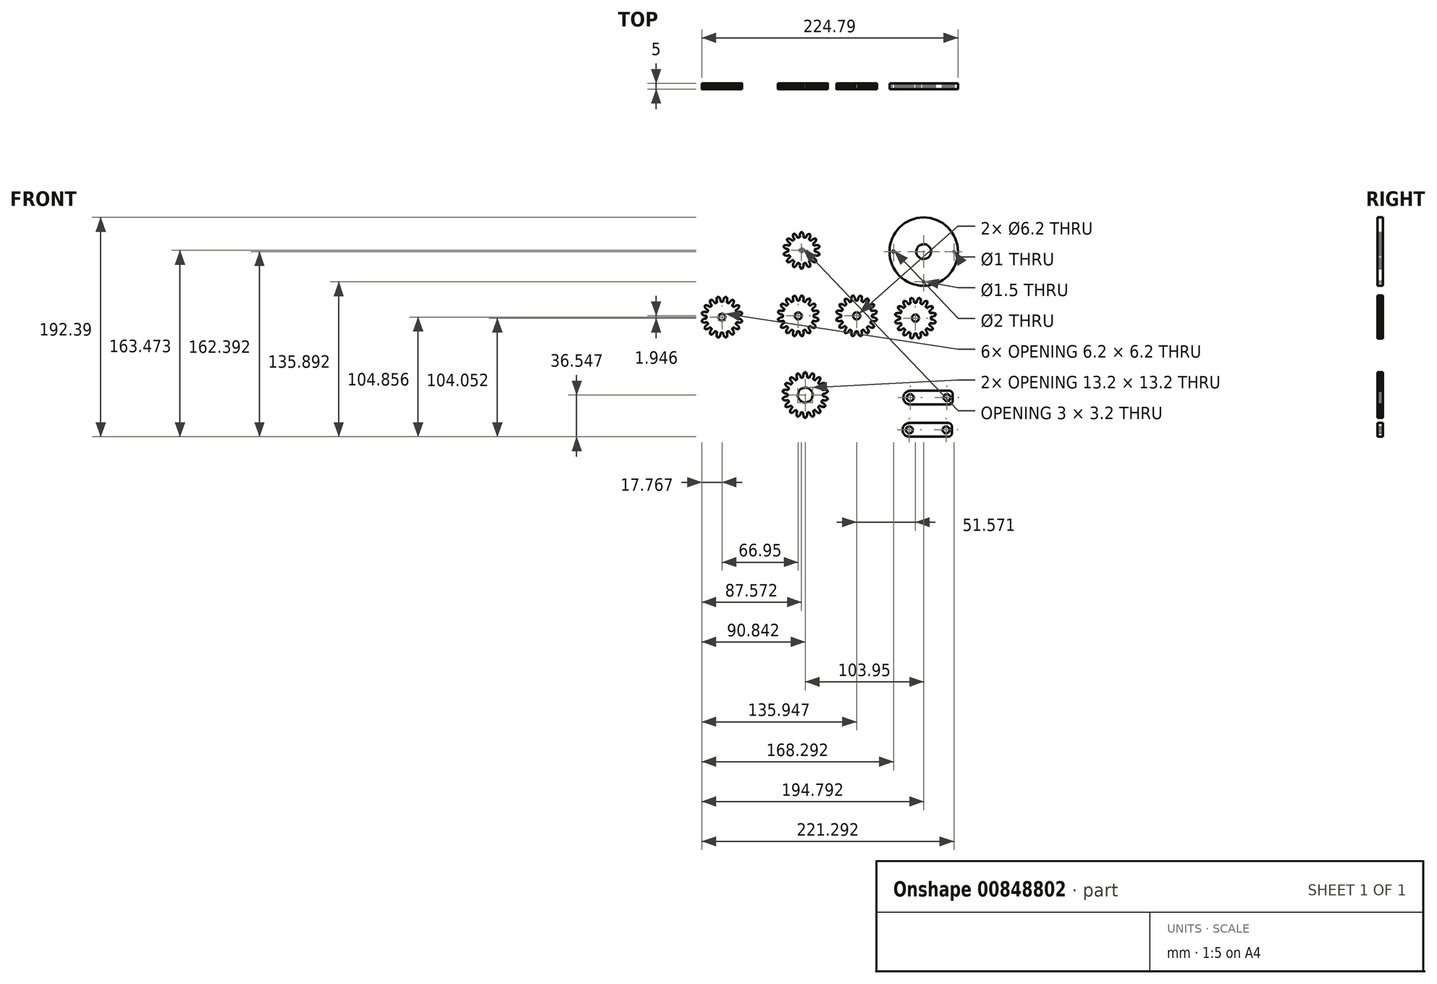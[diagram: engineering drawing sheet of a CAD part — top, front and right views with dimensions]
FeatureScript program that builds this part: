
annotation { "Feature Type Name" : "Feature", "Feature Type Description" : "" }
export const myFeature = defineFeature(function(context is Context, id is Id, definition is map)
    precondition{}
    {
        {
            var Q0;
            Q0=qCreatedBy(makeId("Front.planeOp"),FACE);
            var sketch = newSketch(context, id + "F0", { "sketchPlane" : qUnion([Q0])});
            skArc(sketch, "E0", {"start": v(-65.12, 71.31) * mm, "mid": v(-65.39, 71.53) * mm, "end": v(-65.66, 71.75) * mm});
            skArc(sketch, "E1", {"start": v(-65.12, 71.31) * mm, "mid": v(-64.55, 71.12) * mm, "end": v(-64, 71.37) * mm});
            skLineSegment(sketch, "E2", {"start": v(-61.43, 72.85) * mm, "end": v(-60.46, 73.02) * mm});
            skLineSegment(sketch, "E3", {"start": v(-62.28, 72.6) * mm, "end": v(-61.43, 72.85) * mm});
            skLineSegment(sketch, "E4", {"start": v(-63.02, 72.25) * mm, "end": v(-62.28, 72.6) * mm});
            skLineSegment(sketch, "E5", {"start": v(-63.17, 72.16) * mm, "end": v(-63.02, 72.25) * mm});
            skLineSegment(sketch, "E6", {"start": v(-63.29, 72.07) * mm, "end": v(-63.17, 72.16) * mm});
            skLineSegment(sketch, "E7", {"start": v(-63.37, 72) * mm, "end": v(-63.29, 72.07) * mm});
            skLineSegment(sketch, "E8", {"start": v(-63.59, 71.8) * mm, "end": v(-63.37, 72) * mm});
            skLineSegment(sketch, "E9", {"start": v(-64, 71.37) * mm, "end": v(-63.59, 71.8) * mm});
            skArc(sketch, "E10", {"start": v(-59.66, 72) * mm, "mid": v(-60.05, 72.52) * mm, "end": v(-60.46, 73.02) * mm});
            skLineSegment(sketch, "E11", {"start": v(-60.03, 71.1) * mm, "end": v(-59.66, 72) * mm});
            skLineSegment(sketch, "E12", {"start": v(-60.46, 70.33) * mm, "end": v(-60.03, 71.1) * mm});
            skLineSegment(sketch, "E13", {"start": v(-60.97, 69.68) * mm, "end": v(-60.46, 70.33) * mm});
            skLineSegment(sketch, "E14", {"start": v(-61.1, 69.56) * mm, "end": v(-60.97, 69.68) * mm});
            skLineSegment(sketch, "E15", {"start": v(-61.2, 69.46) * mm, "end": v(-61.1, 69.56) * mm});
            skLineSegment(sketch, "E16", {"start": v(-61.3, 69.4) * mm, "end": v(-61.2, 69.46) * mm});
            skLineSegment(sketch, "E17", {"start": v(-62.05, 68.93) * mm, "end": v(-61.55, 69.23) * mm});
            skArc(sketch, "E18", {"start": v(-62.05, 68.93) * mm, "mid": v(-62.41, 68.45) * mm, "end": v(-62.35, 67.84) * mm});
            skArc(sketch, "E19", {"start": v(-62.05, 67.22) * mm, "mid": v(-62.2, 67.53) * mm, "end": v(-62.35, 67.84) * mm});
            skArc(sketch, "E20", {"start": v(-62.05, 67.22) * mm, "mid": v(-61.62, 66.8) * mm, "end": v(-61.01, 66.78) * mm});
            skLineSegment(sketch, "E21", {"start": v(-58.06, 67) * mm, "end": v(-57.12, 66.73) * mm});
            skLineSegment(sketch, "E22", {"start": v(-58.93, 67.15) * mm, "end": v(-58.06, 67) * mm});
            skLineSegment(sketch, "E23", {"start": v(-59.76, 67.15) * mm, "end": v(-58.93, 67.15) * mm});
            skLineSegment(sketch, "E24", {"start": v(-60.07, 67.1) * mm, "end": v(-59.93, 67.13) * mm});
            skLineSegment(sketch, "E25", {"start": v(-60.18, 67.08) * mm, "end": v(-60.07, 67.1) * mm});
            skLineSegment(sketch, "E26", {"start": v(-60.46, 66.98) * mm, "end": v(-60.18, 67.08) * mm});
            skLineSegment(sketch, "E27", {"start": v(-61.01, 66.78) * mm, "end": v(-60.46, 66.98) * mm});
            skArc(sketch, "E28", {"start": v(-56.83, 65.47) * mm, "mid": v(-56.96, 66.1) * mm, "end": v(-57.12, 66.73) * mm});
            skLineSegment(sketch, "E29", {"start": v(-57.56, 64.81) * mm, "end": v(-56.83, 65.47) * mm});
            skLineSegment(sketch, "E30", {"start": v(-58.28, 64.3) * mm, "end": v(-57.56, 64.81) * mm});
            skLineSegment(sketch, "E31", {"start": v(-59.02, 63.94) * mm, "end": v(-58.28, 64.3) * mm});
            skLineSegment(sketch, "E32", {"start": v(-59.19, 63.89) * mm, "end": v(-59.02, 63.94) * mm});
            skLineSegment(sketch, "E33", {"start": v(-59.33, 63.85) * mm, "end": v(-59.19, 63.89) * mm});
            skLineSegment(sketch, "E34", {"start": v(-59.43, 63.83) * mm, "end": v(-59.33, 63.85) * mm});
            skLineSegment(sketch, "E35", {"start": v(-59.73, 63.8) * mm, "end": v(-59.43, 63.83) * mm});
            skLineSegment(sketch, "E36", {"start": v(-60.32, 63.74) * mm, "end": v(-59.73, 63.8) * mm});
            skArc(sketch, "E37", {"start": v(-60.32, 63.74) * mm, "mid": v(-60.86, 63.46) * mm, "end": v(-61.06, 62.9) * mm});
            skArc(sketch, "E38", {"start": v(-61.06, 62.2) * mm, "mid": v(-61.06, 62.54) * mm, "end": v(-61.06, 62.9) * mm});
            skArc(sketch, "E39", {"start": v(-61.06, 62.2) * mm, "mid": v(-60.86, 61.63) * mm, "end": v(-60.32, 61.35) * mm});
            skLineSegment(sketch, "E40", {"start": v(-57.56, 60.27) * mm, "end": v(-56.83, 59.61) * mm});
            skLineSegment(sketch, "E41", {"start": v(-58.28, 60.78) * mm, "end": v(-57.56, 60.27) * mm});
            skLineSegment(sketch, "E42", {"start": v(-59.02, 61.14) * mm, "end": v(-58.28, 60.78) * mm});
            skLineSegment(sketch, "E43", {"start": v(-59.19, 61.2) * mm, "end": v(-59.02, 61.14) * mm});
            skLineSegment(sketch, "E44", {"start": v(-59.33, 61.24) * mm, "end": v(-59.19, 61.2) * mm});
            skLineSegment(sketch, "E45", {"start": v(-59.43, 61.26) * mm, "end": v(-59.33, 61.24) * mm});
            skLineSegment(sketch, "E46", {"start": v(-59.73, 61.3) * mm, "end": v(-59.43, 61.26) * mm});
            skLineSegment(sketch, "E47", {"start": v(-60.32, 61.35) * mm, "end": v(-59.73, 61.3) * mm});
            skArc(sketch, "E48", {"start": v(-57.12, 58.36) * mm, "mid": v(-56.96, 58.98) * mm, "end": v(-56.83, 59.61) * mm});
            skLineSegment(sketch, "E49", {"start": v(-58.06, 58.08) * mm, "end": v(-57.12, 58.36) * mm});
            skLineSegment(sketch, "E50", {"start": v(-58.93, 57.94) * mm, "end": v(-58.06, 58.08) * mm});
            skLineSegment(sketch, "E51", {"start": v(-59.76, 57.93) * mm, "end": v(-58.93, 57.94) * mm});
            skLineSegment(sketch, "E52", {"start": v(-59.93, 57.95) * mm, "end": v(-59.76, 57.93) * mm});
            skLineSegment(sketch, "E53", {"start": v(-60.07, 57.98) * mm, "end": v(-59.93, 57.95) * mm});
            skLineSegment(sketch, "E54", {"start": v(-60.18, 58) * mm, "end": v(-60.07, 57.98) * mm});
            skLineSegment(sketch, "E55", {"start": v(-60.46, 58.1) * mm, "end": v(-60.18, 58) * mm});
            skLineSegment(sketch, "E56", {"start": v(-61.01, 58.3) * mm, "end": v(-60.46, 58.1) * mm});
            skArc(sketch, "E57", {"start": v(-61.01, 58.3) * mm, "mid": v(-61.62, 58.3) * mm, "end": v(-62.05, 57.87) * mm});
            skArc(sketch, "E58", {"start": v(-62.35, 57.24) * mm, "mid": v(-62.2, 57.55) * mm, "end": v(-62.05, 57.87) * mm});
            skArc(sketch, "E59", {"start": v(-62.35, 57.24) * mm, "mid": v(-62.41, 56.64) * mm, "end": v(-62.05, 56.16) * mm});
            skLineSegment(sketch, "E60", {"start": v(-60.03, 54) * mm, "end": v(-59.66, 53.08) * mm});
            skLineSegment(sketch, "E61", {"start": v(-60.46, 54.76) * mm, "end": v(-60.03, 54) * mm});
            skLineSegment(sketch, "E62", {"start": v(-60.97, 55.4) * mm, "end": v(-60.46, 54.76) * mm});
            skLineSegment(sketch, "E63", {"start": v(-61.1, 55.53) * mm, "end": v(-60.97, 55.4) * mm});
            skLineSegment(sketch, "E64", {"start": v(-61.2, 55.63) * mm, "end": v(-61.1, 55.53) * mm});
            skLineSegment(sketch, "E65", {"start": v(-61.3, 55.7) * mm, "end": v(-61.2, 55.63) * mm});
            skLineSegment(sketch, "E66", {"start": v(-61.55, 55.85) * mm, "end": v(-61.3, 55.7) * mm});
            skLineSegment(sketch, "E67", {"start": v(-62.05, 56.16) * mm, "end": v(-61.55, 55.85) * mm});
            skArc(sketch, "E68", {"start": v(-60.46, 52.07) * mm, "mid": v(-60.05, 52.57) * mm, "end": v(-59.66, 53.08) * mm});
            skLineSegment(sketch, "E69", {"start": v(-61.43, 52.23) * mm, "end": v(-60.46, 52.07) * mm});
            skLineSegment(sketch, "E70", {"start": v(-62.28, 52.48) * mm, "end": v(-61.43, 52.23) * mm});
            skLineSegment(sketch, "E71", {"start": v(-63.02, 52.84) * mm, "end": v(-62.28, 52.48) * mm});
            skLineSegment(sketch, "E72", {"start": v(-63.17, 52.93) * mm, "end": v(-63.02, 52.84) * mm});
            skLineSegment(sketch, "E73", {"start": v(-63.29, 53.01) * mm, "end": v(-63.17, 52.93) * mm});
            skLineSegment(sketch, "E74", {"start": v(-63.37, 53.08) * mm, "end": v(-63.29, 53.01) * mm});
            skLineSegment(sketch, "E75", {"start": v(-63.59, 53.3) * mm, "end": v(-63.37, 53.08) * mm});
            skLineSegment(sketch, "E76", {"start": v(-64, 53.72) * mm, "end": v(-63.59, 53.3) * mm});
            skArc(sketch, "E77", {"start": v(-64, 53.72) * mm, "mid": v(-64.55, 53.97) * mm, "end": v(-65.12, 53.77) * mm});
            skArc(sketch, "E78", {"start": v(-65.66, 53.34) * mm, "mid": v(-65.39, 53.55) * mm, "end": v(-65.12, 53.77) * mm});
            skArc(sketch, "E79", {"start": v(-65.66, 53.34) * mm, "mid": v(-65.98, 52.82) * mm, "end": v(-65.86, 52.23) * mm});
            skLineSegment(sketch, "E80", {"start": v(-64.98, 49.4) * mm, "end": v(-65.04, 48.42) * mm});
            skLineSegment(sketch, "E81", {"start": v(-65.04, 50.28) * mm, "end": v(-64.98, 49.4) * mm});
            skLineSegment(sketch, "E82", {"start": v(-65.22, 51.09) * mm, "end": v(-65.04, 50.28) * mm});
            skLineSegment(sketch, "E83", {"start": v(-65.27, 51.25) * mm, "end": v(-65.22, 51.09) * mm});
            skLineSegment(sketch, "E84", {"start": v(-65.33, 51.39) * mm, "end": v(-65.27, 51.25) * mm});
            skLineSegment(sketch, "E85", {"start": v(-65.38, 51.48) * mm, "end": v(-65.33, 51.39) * mm});
            skLineSegment(sketch, "E86", {"start": v(-65.54, 51.74) * mm, "end": v(-65.38, 51.48) * mm});
            skLineSegment(sketch, "E87", {"start": v(-65.86, 52.23) * mm, "end": v(-65.54, 51.74) * mm});
            skArc(sketch, "E88", {"start": v(-66.2, 47.86) * mm, "mid": v(-65.62, 48.13) * mm, "end": v(-65.04, 48.42) * mm});
            skLineSegment(sketch, "E89", {"start": v(-67, 48.43) * mm, "end": v(-66.2, 47.86) * mm});
            skLineSegment(sketch, "E90", {"start": v(-67.66, 49.02) * mm, "end": v(-67, 48.43) * mm});
            skLineSegment(sketch, "E91", {"start": v(-68.18, 49.66) * mm, "end": v(-67.66, 49.02) * mm});
            skLineSegment(sketch, "E92", {"start": v(-87.56, 64.81) * mm, "end": v(-88.29, 65.47) * mm});
            skLineSegment(sketch, "E93", {"start": v(-86.83, 64.3) * mm, "end": v(-87.56, 64.81) * mm});
            skLineSegment(sketch, "E94", {"start": v(-86.1, 63.94) * mm, "end": v(-86.83, 64.3) * mm});
            skLineSegment(sketch, "E95", {"start": v(-85.93, 63.89) * mm, "end": v(-86.1, 63.94) * mm});
            skLineSegment(sketch, "E96", {"start": v(-85.79, 63.85) * mm, "end": v(-85.93, 63.89) * mm});
            skLineSegment(sketch, "E97", {"start": v(-85.68, 63.83) * mm, "end": v(-85.79, 63.85) * mm});
            skLineSegment(sketch, "E98", {"start": v(-85.38, 63.8) * mm, "end": v(-85.68, 63.83) * mm});
            skLineSegment(sketch, "E99", {"start": v(-84.8, 63.74) * mm, "end": v(-85.38, 63.8) * mm});
            skArc(sketch, "E100", {"start": v(-88, 66.73) * mm, "mid": v(-88.16, 66.1) * mm, "end": v(-88.29, 65.47) * mm});
            skLineSegment(sketch, "E101", {"start": v(-87.06, 67) * mm, "end": v(-88, 66.73) * mm});
            skLineSegment(sketch, "E102", {"start": v(-86.19, 67.15) * mm, "end": v(-87.06, 67) * mm});
            skLineSegment(sketch, "E103", {"start": v(-85.36, 67.15) * mm, "end": v(-86.19, 67.15) * mm});
            skLineSegment(sketch, "E104", {"start": v(-85.2, 67.13) * mm, "end": v(-85.36, 67.15) * mm});
            skLineSegment(sketch, "E105", {"start": v(-85.04, 67.1) * mm, "end": v(-85.2, 67.13) * mm});
            skLineSegment(sketch, "E106", {"start": v(-84.94, 67.08) * mm, "end": v(-85.04, 67.1) * mm});
            skLineSegment(sketch, "E107", {"start": v(-84.66, 66.98) * mm, "end": v(-84.94, 67.08) * mm});
            skLineSegment(sketch, "E108", {"start": v(-84.1, 66.78) * mm, "end": v(-84.66, 66.98) * mm});
            skArc(sketch, "E109", {"start": v(-84.1, 66.78) * mm, "mid": v(-83.5, 66.8) * mm, "end": v(-83.07, 67.22) * mm});
            skArc(sketch, "E110", {"start": v(-82.76, 67.84) * mm, "mid": v(-82.92, 67.53) * mm, "end": v(-83.07, 67.22) * mm});
            skArc(sketch, "E111", {"start": v(-82.76, 67.84) * mm, "mid": v(-82.7, 68.45) * mm, "end": v(-83.07, 68.93) * mm});
            skLineSegment(sketch, "E112", {"start": v(-85.09, 71.1) * mm, "end": v(-85.46, 72) * mm});
            skLineSegment(sketch, "E113", {"start": v(-84.65, 70.33) * mm, "end": v(-85.09, 71.1) * mm});
            skLineSegment(sketch, "E114", {"start": v(-84.14, 69.68) * mm, "end": v(-84.65, 70.33) * mm});
            skLineSegment(sketch, "E115", {"start": v(-84.02, 69.56) * mm, "end": v(-84.14, 69.68) * mm});
            skLineSegment(sketch, "E116", {"start": v(-83.91, 69.46) * mm, "end": v(-84.02, 69.56) * mm});
            skLineSegment(sketch, "E117", {"start": v(-83.83, 69.4) * mm, "end": v(-83.91, 69.46) * mm});
            skLineSegment(sketch, "E118", {"start": v(-83.57, 69.23) * mm, "end": v(-83.83, 69.4) * mm});
            skLineSegment(sketch, "E119", {"start": v(-83.07, 68.93) * mm, "end": v(-83.57, 69.23) * mm});
            skArc(sketch, "E120", {"start": v(-84.66, 73.02) * mm, "mid": v(-85.07, 72.52) * mm, "end": v(-85.46, 72) * mm});
            skLineSegment(sketch, "E121", {"start": v(-83.68, 72.85) * mm, "end": v(-84.66, 73.02) * mm});
            skLineSegment(sketch, "E122", {"start": v(-82.84, 72.6) * mm, "end": v(-83.68, 72.85) * mm});
            skLineSegment(sketch, "E123", {"start": v(-82.1, 72.25) * mm, "end": v(-82.84, 72.6) * mm});
            skLineSegment(sketch, "E124", {"start": v(-81.95, 72.16) * mm, "end": v(-82.1, 72.25) * mm});
            skLineSegment(sketch, "E125", {"start": v(-81.83, 72.07) * mm, "end": v(-81.95, 72.16) * mm});
            skLineSegment(sketch, "E126", {"start": v(-81.74, 72) * mm, "end": v(-81.83, 72.07) * mm});
            skLineSegment(sketch, "E127", {"start": v(-81.53, 71.8) * mm, "end": v(-81.74, 72) * mm});
            skLineSegment(sketch, "E128", {"start": v(-81.12, 71.37) * mm, "end": v(-81.53, 71.8) * mm});
            skArc(sketch, "E129", {"start": v(-81.12, 71.37) * mm, "mid": v(-80.57, 71.12) * mm, "end": v(-80, 71.31) * mm});
            skArc(sketch, "E130", {"start": v(-79.45, 71.75) * mm, "mid": v(-79.73, 71.53) * mm, "end": v(-80, 71.31) * mm});
            skArc(sketch, "E131", {"start": v(-79.45, 71.75) * mm, "mid": v(-79.14, 72.26) * mm, "end": v(-79.26, 72.86) * mm});
            skLineSegment(sketch, "E132", {"start": v(-80.13, 75.68) * mm, "end": v(-80.08, 76.67) * mm});
            skLineSegment(sketch, "E133", {"start": v(-80.08, 74.8) * mm, "end": v(-80.13, 75.68) * mm});
            skLineSegment(sketch, "E134", {"start": v(-79.9, 74) * mm, "end": v(-80.08, 74.8) * mm});
            skLineSegment(sketch, "E135", {"start": v(-79.84, 73.84) * mm, "end": v(-79.9, 74) * mm});
            skLineSegment(sketch, "E136", {"start": v(-79.79, 73.7) * mm, "end": v(-79.84, 73.84) * mm});
            skLineSegment(sketch, "E137", {"start": v(-79.74, 73.6) * mm, "end": v(-79.79, 73.7) * mm});
            skLineSegment(sketch, "E138", {"start": v(-79.58, 73.35) * mm, "end": v(-79.74, 73.6) * mm});
            skLineSegment(sketch, "E139", {"start": v(-79.26, 72.86) * mm, "end": v(-79.58, 73.35) * mm});
            skArc(sketch, "E140", {"start": v(-78.91, 77.23) * mm, "mid": v(-79.5, 76.96) * mm, "end": v(-80.08, 76.67) * mm});
            skLineSegment(sketch, "E141", {"start": v(-78.1, 76.66) * mm, "end": v(-78.91, 77.23) * mm});
            skLineSegment(sketch, "E142", {"start": v(-77.46, 76.07) * mm, "end": v(-78.1, 76.66) * mm});
            skLineSegment(sketch, "E143", {"start": v(-76.94, 75.43) * mm, "end": v(-77.46, 76.07) * mm});
            skLineSegment(sketch, "E144", {"start": v(-76.85, 75.28) * mm, "end": v(-76.94, 75.43) * mm});
            skLineSegment(sketch, "E145", {"start": v(-76.77, 75.15) * mm, "end": v(-76.85, 75.28) * mm});
            skLineSegment(sketch, "E146", {"start": v(-76.73, 75.05) * mm, "end": v(-76.77, 75.15) * mm});
            skLineSegment(sketch, "E147", {"start": v(-76.63, 74.77) * mm, "end": v(-76.73, 75.05) * mm});
            skLineSegment(sketch, "E148", {"start": v(-76.44, 74.2) * mm, "end": v(-76.63, 74.77) * mm});
            skArc(sketch, "E149", {"start": v(-76.44, 74.2) * mm, "mid": v(-76.06, 73.75) * mm, "end": v(-75.46, 73.67) * mm});
            skArc(sketch, "E150", {"start": v(-74.78, 73.83) * mm, "mid": v(-75.12, 73.75) * mm, "end": v(-75.46, 73.67) * mm});
            skArc(sketch, "E151", {"start": v(-74.78, 73.83) * mm, "mid": v(-74.27, 74.15) * mm, "end": v(-74.12, 74.74) * mm});
            skLineSegment(sketch, "E152", {"start": v(-73.68, 77.67) * mm, "end": v(-73.2, 78.53) * mm});
            skLineSegment(sketch, "E153", {"start": v(-74.01, 76.85) * mm, "end": v(-73.68, 77.67) * mm});
            skLineSegment(sketch, "E154", {"start": v(-74.2, 76.05) * mm, "end": v(-74.01, 76.85) * mm});
            skLineSegment(sketch, "E155", {"start": v(-74.22, 75.88) * mm, "end": v(-74.2, 76.05) * mm});
            skLineSegment(sketch, "E156", {"start": v(-74.23, 75.73) * mm, "end": v(-74.22, 75.88) * mm});
            skLineSegment(sketch, "E157", {"start": v(-74.23, 75.62) * mm, "end": v(-74.23, 75.73) * mm});
            skLineSegment(sketch, "E158", {"start": v(-74.2, 75.32) * mm, "end": v(-74.23, 75.62) * mm});
            skLineSegment(sketch, "E159", {"start": v(-74.12, 74.74) * mm, "end": v(-74.2, 75.32) * mm});
            skArc(sketch, "E160", {"start": v(-71.91, 78.53) * mm, "mid": v(-72.56, 78.54) * mm, "end": v(-73.2, 78.53) * mm});
            skLineSegment(sketch, "E161", {"start": v(-71.43, 77.67) * mm, "end": v(-71.91, 78.53) * mm});
            skLineSegment(sketch, "E162", {"start": v(-71.1, 76.85) * mm, "end": v(-71.43, 77.67) * mm});
            skLineSegment(sketch, "E163", {"start": v(-70.91, 76.05) * mm, "end": v(-71.1, 76.85) * mm});
            skArc(sketch, "E164", {"start": v(-84.05, 62.9) * mm, "mid": v(-84.26, 63.46) * mm, "end": v(-84.8, 63.74) * mm});
            skArc(sketch, "E165", {"start": v(-84.05, 62.9) * mm, "mid": v(-84.06, 62.54) * mm, "end": v(-84.05, 62.2) * mm});
            skArc(sketch, "E166", {"start": v(-84.8, 61.35) * mm, "mid": v(-84.26, 61.63) * mm, "end": v(-84.05, 62.2) * mm});
            skLineSegment(sketch, "E167", {"start": v(-84.8, 61.35) * mm, "end": v(-85.38, 61.3) * mm});
            skLineSegment(sketch, "E168", {"start": v(-85.38, 61.3) * mm, "end": v(-85.68, 61.26) * mm});
            skLineSegment(sketch, "E169", {"start": v(-85.68, 61.26) * mm, "end": v(-85.79, 61.24) * mm});
            skLineSegment(sketch, "E170", {"start": v(-85.79, 61.24) * mm, "end": v(-85.93, 61.2) * mm});
            skLineSegment(sketch, "E171", {"start": v(-85.93, 61.2) * mm, "end": v(-86.1, 61.14) * mm});
            skLineSegment(sketch, "E172", {"start": v(-86.83, 60.78) * mm, "end": v(-87.56, 60.27) * mm});
            skLineSegment(sketch, "E173", {"start": v(-87.56, 60.27) * mm, "end": v(-88.29, 59.61) * mm});
            skArc(sketch, "E174", {"start": v(-88.29, 59.61) * mm, "mid": v(-88.16, 58.98) * mm, "end": v(-88, 58.36) * mm});
            skLineSegment(sketch, "E175", {"start": v(-84.1, 58.3) * mm, "end": v(-84.66, 58.1) * mm});
            skLineSegment(sketch, "E176", {"start": v(-84.66, 58.1) * mm, "end": v(-84.94, 58) * mm});
            skLineSegment(sketch, "E177", {"start": v(-84.94, 58) * mm, "end": v(-85.04, 57.98) * mm});
            skLineSegment(sketch, "E178", {"start": v(-85.04, 57.98) * mm, "end": v(-85.2, 57.95) * mm});
            skLineSegment(sketch, "E179", {"start": v(-85.2, 57.95) * mm, "end": v(-85.36, 57.93) * mm});
            skLineSegment(sketch, "E180", {"start": v(-85.36, 57.93) * mm, "end": v(-86.19, 57.94) * mm});
            skLineSegment(sketch, "E181", {"start": v(-86.19, 57.94) * mm, "end": v(-87.06, 58.08) * mm});
            skLineSegment(sketch, "E182", {"start": v(-87.06, 58.08) * mm, "end": v(-88, 58.36) * mm});
            skArc(sketch, "E183", {"start": v(-83.07, 57.87) * mm, "mid": v(-83.5, 58.3) * mm, "end": v(-84.1, 58.3) * mm});
            skArc(sketch, "E184", {"start": v(-83.07, 57.87) * mm, "mid": v(-82.92, 57.55) * mm, "end": v(-82.76, 57.24) * mm});
            skArc(sketch, "E185", {"start": v(-83.07, 56.16) * mm, "mid": v(-82.7, 56.64) * mm, "end": v(-82.76, 57.24) * mm});
            skLineSegment(sketch, "E186", {"start": v(-83.07, 56.16) * mm, "end": v(-83.57, 55.85) * mm});
            skLineSegment(sketch, "E187", {"start": v(-83.57, 55.85) * mm, "end": v(-83.83, 55.7) * mm});
            skLineSegment(sketch, "E188", {"start": v(-83.83, 55.7) * mm, "end": v(-83.91, 55.63) * mm});
            skLineSegment(sketch, "E189", {"start": v(-83.91, 55.63) * mm, "end": v(-84.02, 55.53) * mm});
            skLineSegment(sketch, "E190", {"start": v(-84.02, 55.53) * mm, "end": v(-84.14, 55.4) * mm});
            skLineSegment(sketch, "E191", {"start": v(-84.14, 55.4) * mm, "end": v(-84.65, 54.76) * mm});
            skLineSegment(sketch, "E192", {"start": v(-84.65, 54.76) * mm, "end": v(-85.09, 54) * mm});
            skLineSegment(sketch, "E193", {"start": v(-85.09, 54) * mm, "end": v(-85.46, 53.08) * mm});
            skArc(sketch, "E194", {"start": v(-85.46, 53.08) * mm, "mid": v(-85.07, 52.57) * mm, "end": v(-84.66, 52.07) * mm});
            skLineSegment(sketch, "E195", {"start": v(-81.12, 53.72) * mm, "end": v(-81.53, 53.3) * mm});
            skLineSegment(sketch, "E196", {"start": v(-81.53, 53.3) * mm, "end": v(-81.74, 53.08) * mm});
            skLineSegment(sketch, "E197", {"start": v(-81.74, 53.08) * mm, "end": v(-81.83, 53.01) * mm});
            skLineSegment(sketch, "E198", {"start": v(-81.83, 53.01) * mm, "end": v(-81.95, 52.93) * mm});
            skLineSegment(sketch, "E199", {"start": v(-81.95, 52.93) * mm, "end": v(-82.1, 52.84) * mm});
            skLineSegment(sketch, "E200", {"start": v(-82.1, 52.84) * mm, "end": v(-82.84, 52.48) * mm});
            skLineSegment(sketch, "E201", {"start": v(-82.84, 52.48) * mm, "end": v(-83.68, 52.23) * mm});
            skLineSegment(sketch, "E202", {"start": v(-83.68, 52.23) * mm, "end": v(-84.66, 52.07) * mm});
            skArc(sketch, "E203", {"start": v(-80, 53.77) * mm, "mid": v(-80.57, 53.97) * mm, "end": v(-81.12, 53.72) * mm});
            skArc(sketch, "E204", {"start": v(-80, 53.77) * mm, "mid": v(-79.73, 53.55) * mm, "end": v(-79.45, 53.34) * mm});
            skArc(sketch, "E205", {"start": v(-79.26, 52.23) * mm, "mid": v(-79.14, 52.82) * mm, "end": v(-79.45, 53.34) * mm});
            skLineSegment(sketch, "E206", {"start": v(-79.26, 52.23) * mm, "end": v(-79.58, 51.74) * mm});
            skLineSegment(sketch, "E207", {"start": v(-79.58, 51.74) * mm, "end": v(-79.74, 51.48) * mm});
            skLineSegment(sketch, "E208", {"start": v(-79.74, 51.48) * mm, "end": v(-79.79, 51.39) * mm});
            skLineSegment(sketch, "E209", {"start": v(-79.79, 51.39) * mm, "end": v(-79.84, 51.25) * mm});
            skLineSegment(sketch, "E210", {"start": v(-79.84, 51.25) * mm, "end": v(-79.9, 51.09) * mm});
            skLineSegment(sketch, "E211", {"start": v(-79.9, 51.09) * mm, "end": v(-80.08, 50.28) * mm});
            skLineSegment(sketch, "E212", {"start": v(-80.08, 50.28) * mm, "end": v(-80.13, 49.4) * mm});
            skLineSegment(sketch, "E213", {"start": v(-80.13, 49.4) * mm, "end": v(-80.08, 48.42) * mm});
            skArc(sketch, "E214", {"start": v(-80.08, 48.42) * mm, "mid": v(-79.5, 48.13) * mm, "end": v(-78.91, 47.86) * mm});
            skLineSegment(sketch, "E215", {"start": v(-76.44, 50.88) * mm, "end": v(-76.63, 50.32) * mm});
            skLineSegment(sketch, "E216", {"start": v(-76.63, 50.32) * mm, "end": v(-76.73, 50.03) * mm});
            skLineSegment(sketch, "E217", {"start": v(-76.73, 50.03) * mm, "end": v(-76.77, 49.94) * mm});
            skLineSegment(sketch, "E218", {"start": v(-76.77, 49.94) * mm, "end": v(-76.85, 49.8) * mm});
            skLineSegment(sketch, "E219", {"start": v(-76.85, 49.8) * mm, "end": v(-76.94, 49.66) * mm});
            skLineSegment(sketch, "E220", {"start": v(-76.94, 49.66) * mm, "end": v(-77.46, 49.02) * mm});
            skLineSegment(sketch, "E221", {"start": v(-77.46, 49.02) * mm, "end": v(-78.1, 48.43) * mm});
            skLineSegment(sketch, "E222", {"start": v(-78.1, 48.43) * mm, "end": v(-78.91, 47.86) * mm});
            skArc(sketch, "E223", {"start": v(-75.46, 51.41) * mm, "mid": v(-76.06, 51.34) * mm, "end": v(-76.44, 50.88) * mm});
            skArc(sketch, "E224", {"start": v(-75.46, 51.41) * mm, "mid": v(-75.12, 51.33) * mm, "end": v(-74.78, 51.26) * mm});
            skArc(sketch, "E225", {"start": v(-74.12, 50.35) * mm, "mid": v(-74.27, 50.93) * mm, "end": v(-74.78, 51.26) * mm});
            skLineSegment(sketch, "E226", {"start": v(-74.12, 50.35) * mm, "end": v(-74.2, 49.76) * mm});
            skLineSegment(sketch, "E227", {"start": v(-74.2, 49.76) * mm, "end": v(-74.23, 49.46) * mm});
            skLineSegment(sketch, "E228", {"start": v(-74.23, 49.46) * mm, "end": v(-74.23, 49.36) * mm});
            skLineSegment(sketch, "E229", {"start": v(-74.23, 49.36) * mm, "end": v(-74.22, 49.2) * mm});
            skLineSegment(sketch, "E230", {"start": v(-74.22, 49.2) * mm, "end": v(-74.2, 49.04) * mm});
            skLineSegment(sketch, "E231", {"start": v(-74.2, 49.04) * mm, "end": v(-74.01, 48.23) * mm});
            skLineSegment(sketch, "E232", {"start": v(-74.01, 48.23) * mm, "end": v(-73.68, 47.42) * mm});
            skLineSegment(sketch, "E233", {"start": v(-73.68, 47.42) * mm, "end": v(-73.2, 46.56) * mm});
            skArc(sketch, "E234", {"start": v(-73.2, 46.56) * mm, "mid": v(-72.56, 46.54) * mm, "end": v(-71.91, 46.56) * mm});
            skLineSegment(sketch, "E235", {"start": v(-71, 50.35) * mm, "end": v(-70.92, 49.76) * mm});
            skLineSegment(sketch, "E236", {"start": v(-70.92, 49.76) * mm, "end": v(-70.89, 49.46) * mm});
            skLineSegment(sketch, "E237", {"start": v(-70.89, 49.46) * mm, "end": v(-70.89, 49.36) * mm});
            skLineSegment(sketch, "E238", {"start": v(-70.89, 49.36) * mm, "end": v(-70.9, 49.2) * mm});
            skLineSegment(sketch, "E239", {"start": v(-70.9, 49.2) * mm, "end": v(-70.91, 49.04) * mm});
            skLineSegment(sketch, "E240", {"start": v(-70.91, 49.04) * mm, "end": v(-71.1, 48.23) * mm});
            skLineSegment(sketch, "E241", {"start": v(-71.1, 48.23) * mm, "end": v(-71.43, 47.42) * mm});
            skLineSegment(sketch, "E242", {"start": v(-71.43, 47.42) * mm, "end": v(-71.91, 46.56) * mm});
            skArc(sketch, "E243", {"start": v(-70.34, 51.26) * mm, "mid": v(-70.85, 50.93) * mm, "end": v(-71, 50.35) * mm});
            skArc(sketch, "E244", {"start": v(-70.34, 51.26) * mm, "mid": v(-70, 51.33) * mm, "end": v(-69.66, 51.41) * mm});
            skArc(sketch, "E245", {"start": v(-68.67, 50.88) * mm, "mid": v(-69.06, 51.34) * mm, "end": v(-69.66, 51.41) * mm});
            skLineSegment(sketch, "E246", {"start": v(-68.67, 50.88) * mm, "end": v(-68.49, 50.32) * mm});
            skLineSegment(sketch, "E247", {"start": v(-68.49, 50.32) * mm, "end": v(-68.39, 50.03) * mm});
            skLineSegment(sketch, "E248", {"start": v(-68.39, 50.03) * mm, "end": v(-68.34, 49.94) * mm});
            skLineSegment(sketch, "E249", {"start": v(-68.34, 49.94) * mm, "end": v(-68.27, 49.8) * mm});
            skLineSegment(sketch, "E250", {"start": v(-68.27, 49.8) * mm, "end": v(-68.18, 49.66) * mm});
            skLineSegment(sketch, "E251", {"start": v(-70.88, -82.6) * mm, "end": v(-70.54, -83.46) * mm});
            skLineSegment(sketch, "E252", {"start": v(-70.54, -83.46) * mm, "end": v(-70.07, -84.37) * mm});
            skArc(sketch, "E253", {"start": v(-70.07, -84.37) * mm, "mid": v(-69.39, -84.38) * mm, "end": v(-68.7, -84.37) * mm});
            skLineSegment(sketch, "E254", {"start": v(-67.72, -80.58) * mm, "end": v(-67.67, -81.15) * mm});
            skLineSegment(sketch, "E255", {"start": v(-67.67, -81.15) * mm, "end": v(-67.66, -81.33) * mm});
            skLineSegment(sketch, "E256", {"start": v(-67.66, -81.33) * mm, "end": v(-67.67, -81.53) * mm});
            skLineSegment(sketch, "E257", {"start": v(-67.67, -81.53) * mm, "end": v(-67.7, -81.76) * mm});
            skLineSegment(sketch, "E258", {"start": v(-67.7, -81.76) * mm, "end": v(-67.75, -82.02) * mm});
            skLineSegment(sketch, "E259", {"start": v(-67.75, -82.02) * mm, "end": v(-67.81, -82.3) * mm});
            skLineSegment(sketch, "E260", {"start": v(-67.81, -82.3) * mm, "end": v(-67.9, -82.6) * mm});
            skLineSegment(sketch, "E261", {"start": v(-67.9, -82.6) * mm, "end": v(-68.23, -83.46) * mm});
            skLineSegment(sketch, "E262", {"start": v(-68.23, -83.46) * mm, "end": v(-68.7, -84.37) * mm});
            skArc(sketch, "E263", {"start": v(-67.05, -79.7) * mm, "mid": v(-67.56, -80) * mm, "end": v(-67.72, -80.58) * mm});
            skArc(sketch, "E264", {"start": v(-67.05, -79.7) * mm, "mid": v(-66.7, -79.65) * mm, "end": v(-66.35, -79.58) * mm});
            skArc(sketch, "E265", {"start": v(-65.41, -80.18) * mm, "mid": v(-65.76, -79.7) * mm, "end": v(-66.35, -79.58) * mm});
            skLineSegment(sketch, "E266", {"start": v(-65.41, -80.18) * mm, "end": v(-65.27, -80.73) * mm});
            skLineSegment(sketch, "E267", {"start": v(-65.27, -80.73) * mm, "end": v(-65.21, -80.9) * mm});
            skLineSegment(sketch, "E268", {"start": v(-65.21, -80.9) * mm, "end": v(-65.14, -81.08) * mm});
            skLineSegment(sketch, "E269", {"start": v(-65.14, -81.08) * mm, "end": v(-65.03, -81.3) * mm});
            skLineSegment(sketch, "E270", {"start": v(-65.03, -81.3) * mm, "end": v(-64.9, -81.52) * mm});
            skLineSegment(sketch, "E271", {"start": v(-64.9, -81.52) * mm, "end": v(-64.74, -81.76) * mm});
            skLineSegment(sketch, "E272", {"start": v(-64.74, -81.76) * mm, "end": v(-64.56, -82) * mm});
            skLineSegment(sketch, "E273", {"start": v(-64.56, -82) * mm, "end": v(-63.95, -82.7) * mm});
            skLineSegment(sketch, "E274", {"start": v(-63.95, -82.7) * mm, "end": v(-63.2, -83.4) * mm});
            skArc(sketch, "E275", {"start": v(-63.2, -83.4) * mm, "mid": v(-62.55, -83.18) * mm, "end": v(-61.91, -82.93) * mm});
            skLineSegment(sketch, "E276", {"start": v(-62.28, -79.04) * mm, "end": v(-62.04, -79.55) * mm});
            skLineSegment(sketch, "E277", {"start": v(-62.04, -79.55) * mm, "end": v(-61.97, -79.72) * mm});
            skLineSegment(sketch, "E278", {"start": v(-61.97, -79.72) * mm, "end": v(-61.91, -79.91) * mm});
            skLineSegment(sketch, "E279", {"start": v(-61.91, -79.91) * mm, "end": v(-61.86, -80.14) * mm});
            skLineSegment(sketch, "E280", {"start": v(-61.86, -80.14) * mm, "end": v(-61.81, -80.4) * mm});
            skLineSegment(sketch, "E281", {"start": v(-61.81, -80.4) * mm, "end": v(-61.78, -80.68) * mm});
            skLineSegment(sketch, "E282", {"start": v(-61.78, -80.68) * mm, "end": v(-61.76, -80.99) * mm});
            skLineSegment(sketch, "E283", {"start": v(-61.76, -80.99) * mm, "end": v(-61.78, -81.91) * mm});
            skLineSegment(sketch, "E284", {"start": v(-61.78, -81.91) * mm, "end": v(-61.91, -82.93) * mm});
            skArc(sketch, "E285", {"start": v(-61.95, -77.98) * mm, "mid": v(-62.33, -78.44) * mm, "end": v(-62.28, -79.04) * mm});
            skArc(sketch, "E286", {"start": v(-61.95, -77.98) * mm, "mid": v(-61.64, -77.8) * mm, "end": v(-61.33, -77.63) * mm});
            skArc(sketch, "E287", {"start": v(-60.25, -77.86) * mm, "mid": v(-60.74, -77.53) * mm, "end": v(-61.33, -77.63) * mm});
            skLineSegment(sketch, "E288", {"start": v(-60.25, -77.86) * mm, "end": v(-59.93, -78.33) * mm});
            skLineSegment(sketch, "E289", {"start": v(-59.93, -78.33) * mm, "end": v(-59.82, -78.48) * mm});
            skLineSegment(sketch, "E290", {"start": v(-59.82, -78.48) * mm, "end": v(-59.68, -78.62) * mm});
            skLineSegment(sketch, "E291", {"start": v(-59.68, -78.62) * mm, "end": v(-59.5, -78.78) * mm});
            skLineSegment(sketch, "E292", {"start": v(-59.5, -78.78) * mm, "end": v(-59.3, -78.95) * mm});
            skLineSegment(sketch, "E293", {"start": v(-59.3, -78.95) * mm, "end": v(-59.08, -79.12) * mm});
            skLineSegment(sketch, "E294", {"start": v(-59.08, -79.12) * mm, "end": v(-58.82, -79.29) * mm});
            skLineSegment(sketch, "E295", {"start": v(-58.82, -79.29) * mm, "end": v(-58.01, -79.74) * mm});
            skLineSegment(sketch, "E296", {"start": v(-58.01, -79.74) * mm, "end": v(-57.06, -80.13) * mm});
            skArc(sketch, "E297", {"start": v(18, 12.91) * mm, "mid": v(17.74, 12.67) * mm, "end": v(17.5, 12.41) * mm});
            skLineSegment(sketch, "E298", {"start": v(25.94, 18.5) * mm, "end": v(25.87, 18.69) * mm});
            skLineSegment(sketch, "E299", {"start": v(12.9, -1.47) * mm, "end": v(12.76, -1.5) * mm});
            skArc(sketch, "E300", {"start": v(-78.53, -50.9) * mm, "mid": v(-78.03, -51.24) * mm, "end": v(-77.44, -51.14) * mm});
            skLineSegment(sketch, "E301", {"start": v(-51.73, -65.83) * mm, "end": v(-51.47, -65.95) * mm});
            skLineSegment(sketch, "E302", {"start": v(28.52, -11.7) * mm, "end": v(28.55, -11.93) * mm});
            skLineSegment(sketch, "E303", {"start": v(42.34, 1.86) * mm, "end": v(42.48, 1.83) * mm});
            skLineSegment(sketch, "E304", {"start": v(-65.27, -48.04) * mm, "end": v(-65.21, -47.87) * mm});
            skArc(sketch, "E305", {"start": v(16.38, 12.35) * mm, "mid": v(16.95, 12.16) * mm, "end": v(17.5, 12.41) * mm});
            skLineSegment(sketch, "E306", {"start": v(25.87, 18.69) * mm, "end": v(25.79, 18.9) * mm});
            skLineSegment(sketch, "E307", {"start": v(12.76, -1.5) * mm, "end": v(12.57, -1.52) * mm});
            skLineSegment(sketch, "E308", {"start": v(-78.53, -50.9) * mm, "end": v(-78.85, -50.43) * mm});
            skLineSegment(sketch, "E309", {"start": v(-51.47, -65.95) * mm, "end": v(-51.2, -66.08) * mm});
            skLineSegment(sketch, "E310", {"start": v(28.55, -11.93) * mm, "end": v(28.58, -12.07) * mm});
            skLineSegment(sketch, "E311", {"start": v(42.48, 1.83) * mm, "end": v(42.66, 1.78) * mm});
            skLineSegment(sketch, "E312", {"start": v(-65.21, -47.87) * mm, "end": v(-65.14, -47.68) * mm});
            skLineSegment(sketch, "E313", {"start": v(16.38, 12.35) * mm, "end": v(15.93, 12.73) * mm});
            skLineSegment(sketch, "E314", {"start": v(25.79, 18.9) * mm, "end": v(25.68, 19.12) * mm});
            skLineSegment(sketch, "E315", {"start": v(12.57, -1.52) * mm, "end": v(12.36, -1.53) * mm});
            skLineSegment(sketch, "E316", {"start": v(-78.85, -50.43) * mm, "end": v(-78.96, -50.29) * mm});
            skLineSegment(sketch, "E317", {"start": v(-51.2, -66.08) * mm, "end": v(-50.4, -66.56) * mm});
            skLineSegment(sketch, "E318", {"start": v(28.58, -12.07) * mm, "end": v(28.63, -12.25) * mm});
            skLineSegment(sketch, "E319", {"start": v(42.66, 1.78) * mm, "end": v(42.85, 1.7) * mm});
            skLineSegment(sketch, "E320", {"start": v(-65.14, -47.68) * mm, "end": v(-65.03, -47.47) * mm});
            skLineSegment(sketch, "E321", {"start": v(15.93, 12.73) * mm, "end": v(15.76, 12.87) * mm});
            skLineSegment(sketch, "E322", {"start": v(25.68, 19.12) * mm, "end": v(25.56, 19.35) * mm});
            skLineSegment(sketch, "E323", {"start": v(12.36, -1.53) * mm, "end": v(12.14, -1.53) * mm});
            skLineSegment(sketch, "E324", {"start": v(-78.96, -50.29) * mm, "end": v(-79.1, -50.14) * mm});
            skLineSegment(sketch, "E325", {"start": v(-50.4, -66.56) * mm, "end": v(-49.58, -67.18) * mm});
            skLineSegment(sketch, "E326", {"start": v(28.63, -12.25) * mm, "end": v(28.7, -12.45) * mm});
            skLineSegment(sketch, "E327", {"start": v(42.85, 1.7) * mm, "end": v(43.07, 1.62) * mm});
            skLineSegment(sketch, "E328", {"start": v(-65.03, -47.47) * mm, "end": v(-64.9, -47.25) * mm});
            skLineSegment(sketch, "E329", {"start": v(15.76, 12.87) * mm, "end": v(15.63, 12.95) * mm});
            skLineSegment(sketch, "E330", {"start": v(25.56, 19.35) * mm, "end": v(25.07, 20.12) * mm});
            skLineSegment(sketch, "E331", {"start": v(12.14, -1.53) * mm, "end": v(11.89, -1.52) * mm});
            skLineSegment(sketch, "E332", {"start": v(-79.1, -50.14) * mm, "end": v(-79.27, -49.98) * mm});
            skArc(sketch, "E333", {"start": v(-53.9, -64.74) * mm, "mid": v(-53.68, -65.3) * mm, "end": v(-53.15, -65.56) * mm});
            skLineSegment(sketch, "E334", {"start": v(28.7, -12.45) * mm, "end": v(28.79, -12.66) * mm});
            skLineSegment(sketch, "E335", {"start": v(43.07, 1.62) * mm, "end": v(43.29, 1.51) * mm});
            skLineSegment(sketch, "E336", {"start": v(-64.9, -47.25) * mm, "end": v(-64.74, -47) * mm});
            skLineSegment(sketch, "E337", {"start": v(15.63, 12.95) * mm, "end": v(15.47, 13.04) * mm});
            skLineSegment(sketch, "E338", {"start": v(25.07, 20.12) * mm, "end": v(24.43, 20.9) * mm});
            skLineSegment(sketch, "E339", {"start": v(11.89, -1.52) * mm, "end": v(11.63, -1.5) * mm});
            skLineSegment(sketch, "E340", {"start": v(-79.27, -49.98) * mm, "end": v(-79.47, -49.82) * mm});
            skArc(sketch, "E341", {"start": v(-53.9, -64.74) * mm, "mid": v(-53.89, -64.38) * mm, "end": v(-53.9, -64.03) * mm});
            skLineSegment(sketch, "E342", {"start": v(28.79, -12.66) * mm, "end": v(28.9, -12.88) * mm});
            skLineSegment(sketch, "E343", {"start": v(43.29, 1.51) * mm, "end": v(43.52, 1.4) * mm});
            skLineSegment(sketch, "E344", {"start": v(15.47, 13.04) * mm, "end": v(15.28, 13.13) * mm});
            skArc(sketch, "E345", {"start": v(24.43, 20.9) * mm, "mid": v(23.78, 20.78) * mm, "end": v(23.13, 20.63) * mm});
            skLineSegment(sketch, "E346", {"start": v(11.63, -1.5) * mm, "end": v(10.74, -1.33) * mm});
            skLineSegment(sketch, "E347", {"start": v(-79.47, -49.82) * mm, "end": v(-79.7, -49.65) * mm});
            skArc(sketch, "E348", {"start": v(-53.15, -63.2) * mm, "mid": v(-53.68, -63.47) * mm, "end": v(-53.9, -64.03) * mm});
            skLineSegment(sketch, "E349", {"start": v(28.9, -12.88) * mm, "end": v(29.02, -13.11) * mm});
            skLineSegment(sketch, "E350", {"start": v(43.52, 1.4) * mm, "end": v(44.28, 0.9) * mm});
            skLineSegment(sketch, "E351", {"start": v(-64.56, -46.76) * mm, "end": v(-63.95, -46.06) * mm});
            skLineSegment(sketch, "E352", {"start": v(15.28, 13.13) * mm, "end": v(15.07, 13.22) * mm});
            skLineSegment(sketch, "E353", {"start": v(22.93, 16.73) * mm, "end": v(22.76, 17.29) * mm});
            skLineSegment(sketch, "E354", {"start": v(10.74, -1.33) * mm, "end": v(9.78, -1.04) * mm});
            skLineSegment(sketch, "E355", {"start": v(-79.7, -49.65) * mm, "end": v(-79.95, -49.48) * mm});
            skLineSegment(sketch, "E356", {"start": v(-53.15, -63.2) * mm, "end": v(-52.58, -63.17) * mm});
            skLineSegment(sketch, "E357", {"start": v(29.02, -13.11) * mm, "end": v(29.5, -13.87) * mm});
            skLineSegment(sketch, "E358", {"start": v(44.28, 0.9) * mm, "end": v(45.06, 0.26) * mm});
            skLineSegment(sketch, "E359", {"start": v(-63.95, -46.06) * mm, "end": v(-63.2, -45.37) * mm});
            skLineSegment(sketch, "E360", {"start": v(15.07, 13.22) * mm, "end": v(14.84, 13.3) * mm});
            skLineSegment(sketch, "E361", {"start": v(22.76, 17.29) * mm, "end": v(22.7, 17.5) * mm});
            skArc(sketch, "E362", {"start": v(14.68, -1.72) * mm, "mid": v(14.28, -1.27) * mm, "end": v(13.67, -1.23) * mm});
            skLineSegment(sketch, "E363", {"start": v(-79.95, -49.48) * mm, "end": v(-80.76, -49.03) * mm});
            skLineSegment(sketch, "E364", {"start": v(-52.58, -63.17) * mm, "end": v(-52.4, -63.14) * mm});
            skLineSegment(sketch, "E365", {"start": v(29.5, -13.87) * mm, "end": v(30.14, -14.65) * mm});
            skArc(sketch, "E366", {"start": v(40.78, 2.77) * mm, "mid": v(41, 2.2) * mm, "end": v(41.53, 1.94) * mm});
            skArc(sketch, "E367", {"start": v(-66.35, -49.18) * mm, "mid": v(-65.76, -49.08) * mm, "end": v(-65.41, -48.6) * mm});
            skLineSegment(sketch, "E368", {"start": v(14.84, 13.3) * mm, "end": v(14.59, 13.38) * mm});
            skLineSegment(sketch, "E369", {"start": v(22.7, 17.5) * mm, "end": v(22.67, 17.65) * mm});
            skArc(sketch, "E370", {"start": v(14.68, -1.72) * mm, "mid": v(14.82, -2.04) * mm, "end": v(14.95, -2.37) * mm});
            skLineSegment(sketch, "E371", {"start": v(-80.76, -49.03) * mm, "end": v(-81.72, -48.63) * mm});
            skLineSegment(sketch, "E372", {"start": v(-52.4, -63.14) * mm, "end": v(-52.2, -63.1) * mm});
            skArc(sketch, "E373", {"start": v(30.14, -14.65) * mm, "mid": v(30.8, -14.53) * mm, "end": v(31.45, -14.4) * mm});
            skArc(sketch, "E374", {"start": v(40.78, 2.77) * mm, "mid": v(40.79, 3.12) * mm, "end": v(40.78, 3.47) * mm});
            skArc(sketch, "E375", {"start": v(-66.35, -49.18) * mm, "mid": v(-66.7, -49.12) * mm, "end": v(-67.05, -49.06) * mm});
            skLineSegment(sketch, "E376", {"start": v(14.59, 13.38) * mm, "end": v(13.7, 13.57) * mm});
            skLineSegment(sketch, "E377", {"start": v(22.67, 17.65) * mm, "end": v(22.65, 17.84) * mm});
            skArc(sketch, "E378", {"start": v(14.58, -3.43) * mm, "mid": v(14.98, -2.97) * mm, "end": v(14.95, -2.37) * mm});
            skArc(sketch, "E379", {"start": v(-81.72, -48.63) * mm, "mid": v(-82.24, -49.06) * mm, "end": v(-82.76, -49.5) * mm});
            skLineSegment(sketch, "E380", {"start": v(-52.2, -63.1) * mm, "end": v(-51.98, -63.03) * mm});
            skLineSegment(sketch, "E381", {"start": v(31.64, -10.5) * mm, "end": v(31.82, -11.05) * mm});
            skArc(sketch, "E382", {"start": v(41.53, 4.3) * mm, "mid": v(41, 4.04) * mm, "end": v(40.78, 3.47) * mm});
            skArc(sketch, "E383", {"start": v(-72.56, 63.94) * mm, "mid": v(-73.26, 63.76) * mm, "end": v(-73.77, 63.24) * mm});
            skLineSegment(sketch, "E384", {"start": v(13.7, 13.57) * mm, "end": v(12.7, 13.67) * mm});
            skLineSegment(sketch, "E385", {"start": v(22.65, 17.84) * mm, "end": v(22.64, 18.04) * mm});
            skLineSegment(sketch, "E386", {"start": v(14.58, -3.43) * mm, "end": v(14.07, -3.7) * mm});
            skLineSegment(sketch, "E387", {"start": v(-81.08, -53.04) * mm, "end": v(-81.48, -52.64) * mm});
            skLineSegment(sketch, "E388", {"start": v(-51.98, -63.03) * mm, "end": v(-51.73, -62.93) * mm});
            skLineSegment(sketch, "E389", {"start": v(31.82, -11.05) * mm, "end": v(31.88, -11.26) * mm});
            skLineSegment(sketch, "E390", {"start": v(41.53, 4.3) * mm, "end": v(42.11, 4.36) * mm});
            skArc(sketch, "E391", {"start": v(12.7, 13.67) * mm, "mid": v(12.32, 13.12) * mm, "end": v(11.96, 12.56) * mm});
            skLineSegment(sketch, "E392", {"start": v(22.64, 18.04) * mm, "end": v(22.64, 18.27) * mm});
            skLineSegment(sketch, "E393", {"start": v(14.07, -3.7) * mm, "end": v(13.87, -3.8) * mm});
            skLineSegment(sketch, "E394", {"start": v(-81.48, -52.64) * mm, "end": v(-81.6, -52.51) * mm});
            skLineSegment(sketch, "E395", {"start": v(-51.73, -62.93) * mm, "end": v(-51.47, -62.82) * mm});
            skLineSegment(sketch, "E396", {"start": v(13.87, -3.8) * mm, "end": v(13.75, -3.89) * mm});
            skLineSegment(sketch, "E397", {"start": v(-81.6, -52.51) * mm, "end": v(-81.73, -52.35) * mm});
            skLineSegment(sketch, "E398", {"start": v(-51.47, -62.82) * mm, "end": v(-51.2, -62.69) * mm});
            skArc(sketch, "E399", {"start": v(-72.56, 60.94) * mm, "mid": v(-71.76, 61.16) * mm, "end": v(-71.17, 61.74) * mm});
            skLineSegment(sketch, "E400", {"start": v(13.75, -3.89) * mm, "end": v(13.6, -4) * mm});
            skLineSegment(sketch, "E401", {"start": v(-81.73, -52.35) * mm, "end": v(-81.85, -52.15) * mm});
            skLineSegment(sketch, "E402", {"start": v(-51.2, -62.69) * mm, "end": v(-50.4, -62.2) * mm});
            skLineSegment(sketch, "E403", {"start": v(31.93, -11.6) * mm, "end": v(31.94, -11.8) * mm});
            skLineSegment(sketch, "E404", {"start": v(42.48, 4.41) * mm, "end": v(42.66, 4.47) * mm});
            skLineSegment(sketch, "E405", {"start": v(-72.56, 63.94) * mm, "end": v(-72.56, 64.14) * mm});
            skLineSegment(sketch, "E406", {"start": v(13.6, -4) * mm, "end": v(13.45, -4.14) * mm});
            skLineSegment(sketch, "E407", {"start": v(-81.85, -52.15) * mm, "end": v(-81.98, -51.93) * mm});
            skLineSegment(sketch, "E408", {"start": v(-50.4, -62.2) * mm, "end": v(-49.58, -61.58) * mm});
            skLineSegment(sketch, "E409", {"start": v(31.94, -11.8) * mm, "end": v(31.94, -12.03) * mm});
            skLineSegment(sketch, "E410", {"start": v(42.66, 4.47) * mm, "end": v(42.85, 4.54) * mm});
            skLineSegment(sketch, "E411", {"start": v(-73.77, 63.24) * mm, "end": v(-73.94, 63.34) * mm});
            skLineSegment(sketch, "E412", {"start": v(13.45, -4.14) * mm, "end": v(13.28, -4.3) * mm});
            skLineSegment(sketch, "E413", {"start": v(-81.98, -51.93) * mm, "end": v(-82.1, -51.67) * mm});
            skArc(sketch, "E414", {"start": v(-49.58, -61.58) * mm, "mid": v(-49.7, -60.91) * mm, "end": v(-49.82, -60.24) * mm});
            skLineSegment(sketch, "E415", {"start": v(31.94, -12.03) * mm, "end": v(31.93, -12.28) * mm});
            skLineSegment(sketch, "E416", {"start": v(42.85, 4.54) * mm, "end": v(43.07, 4.62) * mm});
            skLineSegment(sketch, "E417", {"start": v(-73.77, 61.84) * mm, "end": v(-73.94, 61.74) * mm});
            skLineSegment(sketch, "E418", {"start": v(13.28, -4.3) * mm, "end": v(13.12, -4.49) * mm});
            skLineSegment(sketch, "E419", {"start": v(-82.1, -51.67) * mm, "end": v(-82.23, -51.4) * mm});
            skLineSegment(sketch, "E420", {"start": v(-53.72, -59.93) * mm, "end": v(-53.17, -59.78) * mm});
            skLineSegment(sketch, "E421", {"start": v(31.93, -12.28) * mm, "end": v(31.9, -12.54) * mm});
            skLineSegment(sketch, "E422", {"start": v(43.07, 4.62) * mm, "end": v(43.29, 4.73) * mm});
            skLineSegment(sketch, "E423", {"start": v(-72.56, 61.14) * mm, "end": v(-72.56, 60.94) * mm});
            skLineSegment(sketch, "E424", {"start": v(13.12, -4.49) * mm, "end": v(12.95, -4.69) * mm});
            skLineSegment(sketch, "E425", {"start": v(-82.23, -51.4) * mm, "end": v(-82.53, -50.51) * mm});
            skLineSegment(sketch, "E426", {"start": v(-53.17, -59.78) * mm, "end": v(-53, -59.74) * mm});
            skLineSegment(sketch, "E427", {"start": v(31.9, -12.54) * mm, "end": v(31.74, -13.43) * mm});
            skLineSegment(sketch, "E428", {"start": v(43.29, 4.73) * mm, "end": v(43.52, 4.85) * mm});
            skLineSegment(sketch, "E429", {"start": v(-71.35, 61.84) * mm, "end": v(-71.17, 61.74) * mm});
            skLineSegment(sketch, "E430", {"start": v(12.95, -4.69) * mm, "end": v(12.44, -5.43) * mm});
            skLineSegment(sketch, "E431", {"start": v(-82.53, -50.51) * mm, "end": v(-82.76, -49.5) * mm});
            skLineSegment(sketch, "E432", {"start": v(-53, -59.74) * mm, "end": v(-52.8, -59.72) * mm});
            skLineSegment(sketch, "E433", {"start": v(-71.35, 63.24) * mm, "end": v(-71.17, 63.34) * mm});
            skLineSegment(sketch, "E434", {"start": v(12.44, -5.43) * mm, "end": v(11.96, -6.32) * mm});
            skArc(sketch, "E435", {"start": v(-81.03, -54.15) * mm, "mid": v(-80.83, -53.59) * mm, "end": v(-81.08, -53.04) * mm});
            skLineSegment(sketch, "E436", {"start": v(-52.8, -59.72) * mm, "end": v(-52.56, -59.7) * mm});
            skArc(sketch, "E437", {"start": v(11.96, -6.32) * mm, "mid": v(12.32, -6.88) * mm, "end": v(12.7, -7.42) * mm});
            skArc(sketch, "E438", {"start": v(-81.03, -54.15) * mm, "mid": v(-81.26, -54.42) * mm, "end": v(-81.49, -54.7) * mm});
            skLineSegment(sketch, "E439", {"start": v(-52.56, -59.7) * mm, "end": v(-52.3, -59.7) * mm});
            skLineSegment(sketch, "E440", {"start": v(16.38, -6.11) * mm, "end": v(15.93, -6.49) * mm});
            skArc(sketch, "E441", {"start": v(-82.59, -54.84) * mm, "mid": v(-82, -54.99) * mm, "end": v(-81.49, -54.7) * mm});
            skLineSegment(sketch, "E442", {"start": v(-52.3, -59.7) * mm, "end": v(-52.02, -59.72) * mm});
            skArc(sketch, "E443", {"start": v(33.83, -9.58) * mm, "mid": v(33.38, -9.19) * mm, "end": v(32.78, -9.21) * mm});
            skLineSegment(sketch, "E444", {"start": v(40.9, 7.48) * mm, "end": v(41.45, 7.65) * mm});
            skLineSegment(sketch, "E445", {"start": v(15.93, -6.49) * mm, "end": v(15.76, -6.63) * mm});
            skLineSegment(sketch, "E446", {"start": v(-82.59, -54.84) * mm, "end": v(-83.05, -54.5) * mm});
            skLineSegment(sketch, "E447", {"start": v(-52.02, -59.72) * mm, "end": v(-51.71, -59.76) * mm});
            skLineSegment(sketch, "E448", {"start": v(33.83, -9.58) * mm, "end": v(34.1, -10.1) * mm});
            skLineSegment(sketch, "E449", {"start": v(41.45, 7.65) * mm, "end": v(41.67, 7.72) * mm});
            skLineSegment(sketch, "E450", {"start": v(-65.22, 74) * mm, "end": v(-65.04, 74.8) * mm});
            skLineSegment(sketch, "E451", {"start": v(-65.04, 74.8) * mm, "end": v(-64.98, 75.68) * mm});
            skLineSegment(sketch, "E452", {"start": v(-64.98, 75.68) * mm, "end": v(-65.04, 76.67) * mm});
            skArc(sketch, "E453", {"start": v(-65.04, 76.67) * mm, "mid": v(-65.62, 76.96) * mm, "end": v(-66.2, 77.23) * mm});
            skLineSegment(sketch, "E454", {"start": v(-68.67, 74.2) * mm, "end": v(-68.49, 74.77) * mm});
            skLineSegment(sketch, "E455", {"start": v(-68.49, 74.77) * mm, "end": v(-68.39, 75.05) * mm});
            skLineSegment(sketch, "E456", {"start": v(-68.18, 75.43) * mm, "end": v(-67.66, 76.07) * mm});
            skLineSegment(sketch, "E457", {"start": v(-68.27, 75.28) * mm, "end": v(-68.18, 75.43) * mm});
            skLineSegment(sketch, "E458", {"start": v(-68.34, 75.15) * mm, "end": v(-68.27, 75.28) * mm});
            skLineSegment(sketch, "E459", {"start": v(-68.39, 75.05) * mm, "end": v(-68.34, 75.15) * mm});
            skLineSegment(sketch, "E460", {"start": v(36.9, -8.23) * mm, "end": v(37.04, -8.41) * mm});
            skLineSegment(sketch, "E461", {"start": v(40, 9.67) * mm, "end": v(40.5, 9.94) * mm});
            skLineSegment(sketch, "E462", {"start": v(-65.27, 73.84) * mm, "end": v(-65.22, 74) * mm});
            skLineSegment(sketch, "E463", {"start": v(36.52, -7.79) * mm, "end": v(36.9, -8.23) * mm});
            skArc(sketch, "E464", {"start": v(40, 9.67) * mm, "mid": v(39.6, 9.21) * mm, "end": v(39.62, 8.61) * mm});
            skLineSegment(sketch, "E465", {"start": v(-65.33, 73.7) * mm, "end": v(-65.27, 73.84) * mm});
            skArc(sketch, "E466", {"start": v(17.5, -6.17) * mm, "mid": v(17.74, -6.42) * mm, "end": v(18, -6.67) * mm});
            skLineSegment(sketch, "E467", {"start": v(-84.25, -57.72) * mm, "end": v(-84.77, -57.49) * mm});
            skLineSegment(sketch, "E468", {"start": v(-53.5, -57.15) * mm, "end": v(-53.3, -56.98) * mm});
            skArc(sketch, "E469", {"start": v(36.73, -12.2) * mm, "mid": v(37.29, -11.84) * mm, "end": v(37.83, -11.47) * mm});
            skArc(sketch, "E470", {"start": v(39.9, 7.96) * mm, "mid": v(39.76, 8.29) * mm, "end": v(39.62, 8.61) * mm});
            skLineSegment(sketch, "E471", {"start": v(-65.38, 73.6) * mm, "end": v(-65.33, 73.7) * mm});
            skArc(sketch, "E472", {"start": v(17.5, -6.17) * mm, "mid": v(16.95, -5.92) * mm, "end": v(16.38, -6.11) * mm});
            skArc(sketch, "E473", {"start": v(-86.36, -53.8) * mm, "mid": v(-86.7, -54.38) * mm, "end": v(-87.04, -54.98) * mm});
            skLineSegment(sketch, "E474", {"start": v(-53.68, -57.3) * mm, "end": v(-53.5, -57.15) * mm});
            skLineSegment(sketch, "E475", {"start": v(35.84, -11.73) * mm, "end": v(36.73, -12.2) * mm});
            skArc(sketch, "E476", {"start": v(39.9, 7.96) * mm, "mid": v(40.3, 7.52) * mm, "end": v(40.9, 7.48) * mm});
            skLineSegment(sketch, "E477", {"start": v(-65.54, 73.35) * mm, "end": v(-65.38, 73.6) * mm});
            skLineSegment(sketch, "E478", {"start": v(13.7, -7.33) * mm, "end": v(12.7, -7.42) * mm});
            skLineSegment(sketch, "E479", {"start": v(-85.33, -53.85) * mm, "end": v(-86.36, -53.8) * mm});
            skLineSegment(sketch, "E480", {"start": v(-53.85, -57.4) * mm, "end": v(-53.68, -57.3) * mm});
            skLineSegment(sketch, "E481", {"start": v(35.1, -11.21) * mm, "end": v(35.84, -11.73) * mm});
            skLineSegment(sketch, "E482", {"start": v(43.84, 7.58) * mm, "end": v(44.8, 7.28) * mm});
            skLineSegment(sketch, "E483", {"start": v(-65.86, 72.86) * mm, "end": v(-65.54, 73.35) * mm});
            skLineSegment(sketch, "E484", {"start": v(14.59, -7.13) * mm, "end": v(13.7, -7.33) * mm});
            skLineSegment(sketch, "E485", {"start": v(-84.41, -54) * mm, "end": v(-85.33, -53.85) * mm});
            skLineSegment(sketch, "E486", {"start": v(-54, -57.49) * mm, "end": v(-53.85, -57.4) * mm});
            skLineSegment(sketch, "E487", {"start": v(34.9, -11.05) * mm, "end": v(35.1, -11.21) * mm});
            skLineSegment(sketch, "E488", {"start": v(42.95, 7.74) * mm, "end": v(43.84, 7.58) * mm});
            skArc(sketch, "E489", {"start": v(-65.86, 72.86) * mm, "mid": v(-65.98, 72.26) * mm, "end": v(-65.66, 71.75) * mm});
            skLineSegment(sketch, "E490", {"start": v(14.84, -7.06) * mm, "end": v(14.59, -7.13) * mm});
            skLineSegment(sketch, "E491", {"start": v(-84.12, -54.06) * mm, "end": v(-84.41, -54) * mm});
            skLineSegment(sketch, "E492", {"start": v(-54.53, -57.72) * mm, "end": v(-54, -57.49) * mm});
            skLineSegment(sketch, "E493", {"start": v(34.71, -10.88) * mm, "end": v(34.9, -11.05) * mm});
            skLineSegment(sketch, "E494", {"start": v(42.69, 7.76) * mm, "end": v(42.95, 7.74) * mm});
            skLineSegment(sketch, "E495", {"start": v(15.07, -6.97) * mm, "end": v(14.84, -7.06) * mm});
            skLineSegment(sketch, "E496", {"start": v(-83.84, -54.14) * mm, "end": v(-84.12, -54.06) * mm});
            skArc(sketch, "E497", {"start": v(-54.53, -57.72) * mm, "mid": v(-54.94, -58.15) * mm, "end": v(-54.95, -58.75) * mm});
            skLineSegment(sketch, "E498", {"start": v(34.55, -10.72) * mm, "end": v(34.71, -10.88) * mm});
            skLineSegment(sketch, "E499", {"start": v(42.44, 7.77) * mm, "end": v(42.69, 7.76) * mm});
            skLineSegment(sketch, "E500", {"start": v(15.28, -6.89) * mm, "end": v(15.07, -6.97) * mm});
            skLineSegment(sketch, "E501", {"start": v(-83.6, -54.23) * mm, "end": v(-83.84, -54.14) * mm});
            skArc(sketch, "E502", {"start": v(-54.7, -59.42) * mm, "mid": v(-54.82, -59.08) * mm, "end": v(-54.95, -58.75) * mm});
            skLineSegment(sketch, "E503", {"start": v(34.41, -10.56) * mm, "end": v(34.55, -10.72) * mm});
            skLineSegment(sketch, "E504", {"start": v(42.21, 7.77) * mm, "end": v(42.44, 7.77) * mm});
            skLineSegment(sketch, "E505", {"start": v(15.47, -6.8) * mm, "end": v(15.28, -6.89) * mm});
            skLineSegment(sketch, "E506", {"start": v(-83.38, -54.32) * mm, "end": v(-83.6, -54.23) * mm});
            skArc(sketch, "E507", {"start": v(-54.7, -59.42) * mm, "mid": v(-54.32, -59.87) * mm, "end": v(-53.72, -59.93) * mm});
            skLineSegment(sketch, "E508", {"start": v(34.3, -10.42) * mm, "end": v(34.41, -10.56) * mm});
            skLineSegment(sketch, "E509", {"start": v(42, 7.76) * mm, "end": v(42.21, 7.77) * mm});
            skLineSegment(sketch, "E510", {"start": v(15.63, -6.7) * mm, "end": v(15.47, -6.8) * mm});
            skLineSegment(sketch, "E511", {"start": v(-83.2, -54.41) * mm, "end": v(-83.38, -54.32) * mm});
            skLineSegment(sketch, "E512", {"start": v(-50.8, -59.93) * mm, "end": v(-49.82, -60.24) * mm});
            skLineSegment(sketch, "E513", {"start": v(34.21, -10.3) * mm, "end": v(34.3, -10.42) * mm});
            skLineSegment(sketch, "E514", {"start": v(41.82, 7.74) * mm, "end": v(42, 7.76) * mm});
            skLineSegment(sketch, "E515", {"start": v(15.76, -6.63) * mm, "end": v(15.63, -6.7) * mm});
            skLineSegment(sketch, "E516", {"start": v(-83.05, -54.5) * mm, "end": v(-83.2, -54.41) * mm});
            skLineSegment(sketch, "E517", {"start": v(-51.71, -59.76) * mm, "end": v(-50.8, -59.93) * mm});
            skLineSegment(sketch, "E518", {"start": v(34.1, -10.1) * mm, "end": v(34.21, -10.3) * mm});
            skLineSegment(sketch, "E519", {"start": v(41.67, 7.72) * mm, "end": v(41.82, 7.74) * mm});
            skArc(sketch, "E520", {"start": v(18, 12.91) * mm, "mid": v(18.25, 13.46) * mm, "end": v(18.06, 14.03) * mm});
            skLineSegment(sketch, "E521", {"start": v(26, 18.31) * mm, "end": v(25.94, 18.5) * mm});
            skLineSegment(sketch, "E522", {"start": v(13.12, -1.4) * mm, "end": v(12.9, -1.47) * mm});
            skArc(sketch, "E523", {"start": v(-76.83, -50.79) * mm, "mid": v(-77.14, -50.96) * mm, "end": v(-77.44, -51.14) * mm});
            skLineSegment(sketch, "E524", {"start": v(-51.98, -65.74) * mm, "end": v(-51.73, -65.83) * mm});
            skLineSegment(sketch, "E525", {"start": v(28.47, -11.12) * mm, "end": v(28.52, -11.7) * mm});
            skLineSegment(sketch, "E526", {"start": v(42.11, 1.89) * mm, "end": v(42.34, 1.86) * mm});
            skLineSegment(sketch, "E527", {"start": v(-65.41, -48.6) * mm, "end": v(-65.27, -48.04) * mm});
            skLineSegment(sketch, "E528", {"start": v(16.84, 16.7) * mm, "end": v(16.74, 17.7) * mm});
            skLineSegment(sketch, "E529", {"start": v(26.03, 18.17) * mm, "end": v(26, 18.31) * mm});
            skLineSegment(sketch, "E530", {"start": v(13.67, -1.23) * mm, "end": v(13.12, -1.4) * mm});
            skArc(sketch, "E531", {"start": v(-76.83, -50.79) * mm, "mid": v(-76.45, -50.33) * mm, "end": v(-76.5, -49.73) * mm});
            skLineSegment(sketch, "E532", {"start": v(-52.2, -65.67) * mm, "end": v(-51.98, -65.74) * mm});
            skArc(sketch, "E533", {"start": v(28.47, -11.12) * mm, "mid": v(28.2, -10.58) * mm, "end": v(27.64, -10.37) * mm});
            skLineSegment(sketch, "E534", {"start": v(41.53, 1.94) * mm, "end": v(42.11, 1.89) * mm});
            skArc(sketch, "E535", {"start": v(-61.91, -45.83) * mm, "mid": v(-62.55, -45.59) * mm, "end": v(-63.2, -45.37) * mm});
            skLineSegment(sketch, "E536", {"start": v(17.03, 15.82) * mm, "end": v(16.84, 16.7) * mm});
            skLineSegment(sketch, "E537", {"start": v(26.05, 17.94) * mm, "end": v(26.03, 18.17) * mm});
            skArc(sketch, "E538", {"start": v(9.52, 0.26) * mm, "mid": v(9.63, -0.39) * mm, "end": v(9.78, -1.04) * mm});
            skLineSegment(sketch, "E539", {"start": v(-77, -46.86) * mm, "end": v(-76.86, -45.83) * mm});
            skLineSegment(sketch, "E540", {"start": v(-52.4, -65.63) * mm, "end": v(-52.2, -65.67) * mm});
            skArc(sketch, "E541", {"start": v(26.93, -10.37) * mm, "mid": v(27.29, -10.38) * mm, "end": v(27.64, -10.37) * mm});
            skArc(sketch, "E542", {"start": v(44.8, -1.04) * mm, "mid": v(44.94, -0.39) * mm, "end": v(45.06, 0.26) * mm});
            skLineSegment(sketch, "E543", {"start": v(-61.78, -46.86) * mm, "end": v(-61.91, -45.83) * mm});
            skLineSegment(sketch, "E544", {"start": v(17.1, 15.57) * mm, "end": v(17.03, 15.82) * mm});
            skLineSegment(sketch, "E545", {"start": v(26.1, 17.37) * mm, "end": v(26.05, 17.94) * mm});
            skLineSegment(sketch, "E546", {"start": v(10.3, 0.9) * mm, "end": v(9.52, 0.26) * mm});
            skLineSegment(sketch, "E547", {"start": v(-77.01, -47.78) * mm, "end": v(-77, -46.86) * mm});
            skLineSegment(sketch, "E548", {"start": v(-52.58, -65.6) * mm, "end": v(-52.4, -65.63) * mm});
            skArc(sketch, "E549", {"start": v(26.93, -10.37) * mm, "mid": v(26.37, -10.58) * mm, "end": v(26.1, -11.12) * mm});
            skLineSegment(sketch, "E550", {"start": v(43.84, -1.33) * mm, "end": v(44.8, -1.04) * mm});
            skLineSegment(sketch, "E551", {"start": v(-61.76, -47.78) * mm, "end": v(-61.78, -46.86) * mm});
            skLineSegment(sketch, "E552", {"start": v(17.2, 15.34) * mm, "end": v(17.1, 15.57) * mm});
            skArc(sketch, "E553", {"start": v(26.1, 17.37) * mm, "mid": v(26.37, 16.83) * mm, "end": v(26.93, 16.62) * mm});
            skLineSegment(sketch, "E554", {"start": v(-77, -48.09) * mm, "end": v(-77.01, -47.78) * mm});
            skLineSegment(sketch, "E555", {"start": v(-53.15, -65.56) * mm, "end": v(-52.58, -65.6) * mm});
            skLineSegment(sketch, "E556", {"start": v(25.07, -13.87) * mm, "end": v(24.43, -14.65) * mm});
            skLineSegment(sketch, "E557", {"start": v(42.95, -1.5) * mm, "end": v(43.84, -1.33) * mm});
            skLineSegment(sketch, "E558", {"start": v(-61.78, -48.09) * mm, "end": v(-61.76, -47.78) * mm});
            skLineSegment(sketch, "E559", {"start": v(-76.96, -48.37) * mm, "end": v(-77, -48.09) * mm});
            skArc(sketch, "E560", {"start": v(-49.82, -68.52) * mm, "mid": v(-49.7, -67.86) * mm, "end": v(-49.58, -67.18) * mm});
            skLineSegment(sketch, "E561", {"start": v(17.28, 15.13) * mm, "end": v(17.2, 15.34) * mm});
            skArc(sketch, "E562", {"start": v(27.64, 16.62) * mm, "mid": v(27.29, 16.62) * mm, "end": v(26.93, 16.62) * mm});
            skLineSegment(sketch, "E563", {"start": v(25.56, -13.11) * mm, "end": v(25.07, -13.87) * mm});
            skLineSegment(sketch, "E564", {"start": v(42.69, -1.52) * mm, "end": v(42.95, -1.5) * mm});
            skLineSegment(sketch, "E565", {"start": v(-61.81, -48.37) * mm, "end": v(-61.78, -48.09) * mm});
            skLineSegment(sketch, "E566", {"start": v(-76.92, -48.63) * mm, "end": v(-76.96, -48.37) * mm});
            skLineSegment(sketch, "E567", {"start": v(-50.8, -68.83) * mm, "end": v(-49.82, -68.52) * mm});
            skLineSegment(sketch, "E568", {"start": v(17.37, 14.94) * mm, "end": v(17.28, 15.13) * mm});
            skArc(sketch, "E569", {"start": v(27.64, 16.62) * mm, "mid": v(28.2, 16.83) * mm, "end": v(28.47, 17.37) * mm});
            skLineSegment(sketch, "E570", {"start": v(25.68, -12.88) * mm, "end": v(25.56, -13.11) * mm});
            skLineSegment(sketch, "E571", {"start": v(42.44, -1.53) * mm, "end": v(42.69, -1.52) * mm});
            skLineSegment(sketch, "E572", {"start": v(-61.86, -48.63) * mm, "end": v(-61.81, -48.37) * mm});
            skLineSegment(sketch, "E573", {"start": v(-76.87, -48.86) * mm, "end": v(-76.92, -48.63) * mm});
            skLineSegment(sketch, "E574", {"start": v(-51.71, -69.01) * mm, "end": v(-50.8, -68.83) * mm});
            skLineSegment(sketch, "E575", {"start": v(17.46, 14.78) * mm, "end": v(17.37, 14.94) * mm});
            skLineSegment(sketch, "E576", {"start": v(29.5, 20.12) * mm, "end": v(30.14, 20.9) * mm});
            skLineSegment(sketch, "E577", {"start": v(25.79, -12.66) * mm, "end": v(25.68, -12.88) * mm});
            skLineSegment(sketch, "E578", {"start": v(42.21, -1.53) * mm, "end": v(42.44, -1.53) * mm});
            skLineSegment(sketch, "E579", {"start": v(-61.91, -48.86) * mm, "end": v(-61.86, -48.63) * mm});
            skLineSegment(sketch, "E580", {"start": v(-76.8, -49.05) * mm, "end": v(-76.87, -48.86) * mm});
            skLineSegment(sketch, "E581", {"start": v(-52.02, -69.04) * mm, "end": v(-51.71, -69.01) * mm});
            skLineSegment(sketch, "E582", {"start": v(17.54, 14.65) * mm, "end": v(17.46, 14.78) * mm});
            skLineSegment(sketch, "E583", {"start": v(29.02, 19.35) * mm, "end": v(29.5, 20.12) * mm});
            skLineSegment(sketch, "E584", {"start": v(25.87, -12.45) * mm, "end": v(25.79, -12.66) * mm});
            skLineSegment(sketch, "E585", {"start": v(42, -1.52) * mm, "end": v(42.21, -1.53) * mm});
            skLineSegment(sketch, "E586", {"start": v(-61.97, -49.05) * mm, "end": v(-61.91, -48.86) * mm});
            skLineSegment(sketch, "E587", {"start": v(-76.74, -49.21) * mm, "end": v(-76.8, -49.05) * mm});
            skLineSegment(sketch, "E588", {"start": v(-52.3, -69.06) * mm, "end": v(-52.02, -69.04) * mm});
            skLineSegment(sketch, "E589", {"start": v(17.68, 14.48) * mm, "end": v(17.54, 14.65) * mm});
            skLineSegment(sketch, "E590", {"start": v(28.9, 19.12) * mm, "end": v(29.02, 19.35) * mm});
            skLineSegment(sketch, "E591", {"start": v(25.94, -12.25) * mm, "end": v(25.87, -12.45) * mm});
            skLineSegment(sketch, "E592", {"start": v(41.82, -1.5) * mm, "end": v(42, -1.52) * mm});
            skLineSegment(sketch, "E593", {"start": v(-62.04, -49.21) * mm, "end": v(-61.97, -49.05) * mm});
            skLineSegment(sketch, "E594", {"start": v(-76.5, -49.73) * mm, "end": v(-76.74, -49.21) * mm});
            skLineSegment(sketch, "E595", {"start": v(-52.56, -69.06) * mm, "end": v(-52.3, -69.06) * mm});
            skLineSegment(sketch, "E596", {"start": v(18.06, 14.03) * mm, "end": v(17.68, 14.48) * mm});
            skLineSegment(sketch, "E597", {"start": v(28.79, 18.9) * mm, "end": v(28.9, 19.12) * mm});
            skLineSegment(sketch, "E598", {"start": v(26, -12.07) * mm, "end": v(25.94, -12.25) * mm});
            skLineSegment(sketch, "E599", {"start": v(41.67, -1.47) * mm, "end": v(41.82, -1.5) * mm});
            skLineSegment(sketch, "E600", {"start": v(-87.3, -65.95) * mm, "end": v(-87.58, -66.08) * mm});
            skLineSegment(sketch, "E601", {"start": v(-62.28, -49.73) * mm, "end": v(-62.04, -49.21) * mm});
            skArc(sketch, "E602", {"start": v(-75.59, -45.37) * mm, "mid": v(-76.23, -45.59) * mm, "end": v(-76.86, -45.83) * mm});
            skLineSegment(sketch, "E603", {"start": v(-52.8, -69.05) * mm, "end": v(-52.56, -69.06) * mm});
            skArc(sketch, "E604", {"start": v(17.85, 18.45) * mm, "mid": v(17.29, 18.09) * mm, "end": v(16.74, 17.7) * mm});
            skLineSegment(sketch, "E605", {"start": v(28.7, 18.69) * mm, "end": v(28.79, 18.9) * mm});
            skLineSegment(sketch, "E606", {"start": v(26.03, -11.93) * mm, "end": v(26, -12.07) * mm});
            skLineSegment(sketch, "E607", {"start": v(41.45, -1.4) * mm, "end": v(41.67, -1.47) * mm});
            skLineSegment(sketch, "E608", {"start": v(-87.04, -65.83) * mm, "end": v(-87.3, -65.95) * mm});
            skArc(sketch, "E609", {"start": v(-62.28, -49.73) * mm, "mid": v(-62.33, -50.32) * mm, "end": v(-61.95, -50.79) * mm});
            skLineSegment(sketch, "E610", {"start": v(-74.83, -46.06) * mm, "end": v(-75.59, -45.37) * mm});
            skLineSegment(sketch, "E611", {"start": v(-53, -69.03) * mm, "end": v(-52.8, -69.05) * mm});
            skLineSegment(sketch, "E612", {"start": v(18.74, 17.97) * mm, "end": v(17.85, 18.45) * mm});
            skLineSegment(sketch, "E613", {"start": v(28.63, 18.5) * mm, "end": v(28.7, 18.69) * mm});
            skLineSegment(sketch, "E614", {"start": v(26.05, -11.7) * mm, "end": v(26.03, -11.93) * mm});
            skLineSegment(sketch, "E615", {"start": v(40.9, -1.23) * mm, "end": v(41.45, -1.4) * mm});
            skLineSegment(sketch, "E616", {"start": v(-86.8, -65.74) * mm, "end": v(-87.04, -65.83) * mm});
            skArc(sketch, "E617", {"start": v(-61.33, -51.14) * mm, "mid": v(-61.64, -50.96) * mm, "end": v(-61.95, -50.79) * mm});
            skLineSegment(sketch, "E618", {"start": v(-53.17, -68.99) * mm, "end": v(-53, -69.03) * mm});
            skLineSegment(sketch, "E619", {"start": v(19.48, 17.46) * mm, "end": v(18.74, 17.97) * mm});
            skLineSegment(sketch, "E620", {"start": v(28.58, 18.31) * mm, "end": v(28.63, 18.5) * mm});
            skLineSegment(sketch, "E621", {"start": v(26.1, -11.12) * mm, "end": v(26.05, -11.7) * mm});
            skArc(sketch, "E622", {"start": v(40.9, -1.23) * mm, "mid": v(40.3, -1.27) * mm, "end": v(39.9, -1.72) * mm});
            skLineSegment(sketch, "E623", {"start": v(-86.57, -65.67) * mm, "end": v(-86.8, -65.74) * mm});
            skArc(sketch, "E624", {"start": v(-61.33, -51.14) * mm, "mid": v(-60.74, -51.24) * mm, "end": v(-60.25, -50.9) * mm});
            skLineSegment(sketch, "E625", {"start": v(-74.04, -47) * mm, "end": v(-74.22, -46.76) * mm});
            skLineSegment(sketch, "E626", {"start": v(-53.72, -68.83) * mm, "end": v(-53.17, -68.99) * mm});
            skLineSegment(sketch, "E627", {"start": v(19.68, 17.3) * mm, "end": v(19.48, 17.46) * mm});
            skLineSegment(sketch, "E628", {"start": v(28.55, 18.17) * mm, "end": v(28.58, 18.31) * mm});
            skArc(sketch, "E629", {"start": v(23.13, -14.4) * mm, "mid": v(23.78, -14.53) * mm, "end": v(24.43, -14.65) * mm});
            skArc(sketch, "E630", {"start": v(39.62, -2.37) * mm, "mid": v(39.76, -2.04) * mm, "end": v(39.9, -1.72) * mm});
            skLineSegment(sketch, "E631", {"start": v(-86.38, -65.63) * mm, "end": v(-86.57, -65.67) * mm});
            skLineSegment(sketch, "E632", {"start": v(-58.01, -49.03) * mm, "end": v(-57.06, -48.63) * mm});
            skLineSegment(sketch, "E633", {"start": v(-73.88, -47.25) * mm, "end": v(-74.04, -47) * mm});
            skArc(sketch, "E634", {"start": v(-53.72, -68.83) * mm, "mid": v(-54.32, -68.9) * mm, "end": v(-54.7, -69.35) * mm});
            skLineSegment(sketch, "E635", {"start": v(19.86, 17.12) * mm, "end": v(19.68, 17.3) * mm});
            skLineSegment(sketch, "E636", {"start": v(28.52, 17.94) * mm, "end": v(28.55, 18.17) * mm});
            skLineSegment(sketch, "E637", {"start": v(22.83, -13.43) * mm, "end": v(23.13, -14.4) * mm});
            skArc(sketch, "E638", {"start": v(39.62, -2.37) * mm, "mid": v(39.6, -2.97) * mm, "end": v(40, -3.43) * mm});
            skLineSegment(sketch, "E639", {"start": v(-86.2, -65.6) * mm, "end": v(-86.38, -65.63) * mm});
            skLineSegment(sketch, "E640", {"start": v(-58.82, -49.48) * mm, "end": v(-58.01, -49.03) * mm});
            skLineSegment(sketch, "E641", {"start": v(-73.75, -47.47) * mm, "end": v(-73.88, -47.25) * mm});
            skArc(sketch, "E642", {"start": v(-54.95, -70.02) * mm, "mid": v(-54.82, -69.68) * mm, "end": v(-54.7, -69.35) * mm});
            skLineSegment(sketch, "E643", {"start": v(20.02, 16.96) * mm, "end": v(19.86, 17.12) * mm});
            skLineSegment(sketch, "E644", {"start": v(28.47, 17.37) * mm, "end": v(28.52, 17.94) * mm});
            skLineSegment(sketch, "E645", {"start": v(22.67, -12.54) * mm, "end": v(22.83, -13.43) * mm});
            skLineSegment(sketch, "E646", {"start": v(42.14, -5.43) * mm, "end": v(42.61, -6.32) * mm});
            skLineSegment(sketch, "E647", {"start": v(-85.63, -65.56) * mm, "end": v(-86.2, -65.6) * mm});
            skLineSegment(sketch, "E648", {"start": v(-59.08, -49.65) * mm, "end": v(-58.82, -49.48) * mm});
            skLineSegment(sketch, "E649", {"start": v(-73.64, -47.68) * mm, "end": v(-73.75, -47.47) * mm});
            skArc(sketch, "E650", {"start": v(-54.95, -70.02) * mm, "mid": v(-54.94, -70.61) * mm, "end": v(-54.53, -71.04) * mm});
            skLineSegment(sketch, "E651", {"start": v(20.16, 16.8) * mm, "end": v(20.02, 16.96) * mm});
            skArc(sketch, "E652", {"start": v(31.45, 20.63) * mm, "mid": v(30.8, 20.78) * mm, "end": v(30.14, 20.9) * mm});
            skLineSegment(sketch, "E653", {"start": v(22.65, -12.28) * mm, "end": v(22.67, -12.54) * mm});
            skLineSegment(sketch, "E654", {"start": v(41.62, -4.69) * mm, "end": v(42.14, -5.43) * mm});
            skArc(sketch, "E655", {"start": v(-85.63, -65.56) * mm, "mid": v(-85.1, -65.3) * mm, "end": v(-84.88, -64.74) * mm});
            skLineSegment(sketch, "E656", {"start": v(-59.3, -49.82) * mm, "end": v(-59.08, -49.65) * mm});
            skLineSegment(sketch, "E657", {"start": v(-73.56, -47.87) * mm, "end": v(-73.64, -47.68) * mm});
            skLineSegment(sketch, "E658", {"start": v(-52.3, -72.92) * mm, "end": v(-51.74, -73.79) * mm});
            skLineSegment(sketch, "E659", {"start": v(20.28, 16.66) * mm, "end": v(20.16, 16.8) * mm});
            skLineSegment(sketch, "E660", {"start": v(31.74, 19.67) * mm, "end": v(31.45, 20.63) * mm});
            skLineSegment(sketch, "E661", {"start": v(22.64, -12.03) * mm, "end": v(22.65, -12.28) * mm});
            skLineSegment(sketch, "E662", {"start": v(41.46, -4.49) * mm, "end": v(41.62, -4.69) * mm});
            skArc(sketch, "E663", {"start": v(-84.88, -64.03) * mm, "mid": v(-84.89, -64.38) * mm, "end": v(-84.88, -64.74) * mm});
            skLineSegment(sketch, "E664", {"start": v(-59.5, -49.98) * mm, "end": v(-59.3, -49.82) * mm});
            skLineSegment(sketch, "E665", {"start": v(-73.5, -48.04) * mm, "end": v(-73.56, -47.87) * mm});
            skLineSegment(sketch, "E666", {"start": v(-52.87, -72.2) * mm, "end": v(-52.3, -72.92) * mm});
            skLineSegment(sketch, "E667", {"start": v(20.36, 16.54) * mm, "end": v(20.28, 16.66) * mm});
            skLineSegment(sketch, "E668", {"start": v(31.9, 18.78) * mm, "end": v(31.74, 19.67) * mm});
            skLineSegment(sketch, "E669", {"start": v(22.64, -11.8) * mm, "end": v(22.64, -12.03) * mm});
            skLineSegment(sketch, "E670", {"start": v(41.3, -4.3) * mm, "end": v(41.46, -4.49) * mm});
            skArc(sketch, "E671", {"start": v(-84.88, -64.03) * mm, "mid": v(-85.1, -63.47) * mm, "end": v(-85.63, -63.2) * mm});
            skLineSegment(sketch, "E672", {"start": v(-59.68, -50.14) * mm, "end": v(-59.5, -49.98) * mm});
            skLineSegment(sketch, "E673", {"start": v(-73.37, -48.6) * mm, "end": v(-73.5, -48.04) * mm});
            skLineSegment(sketch, "E674", {"start": v(-53.09, -71.98) * mm, "end": v(-52.87, -72.2) * mm});
            skLineSegment(sketch, "E675", {"start": v(20.47, 16.34) * mm, "end": v(20.36, 16.54) * mm});
            skLineSegment(sketch, "E676", {"start": v(31.93, 18.52) * mm, "end": v(31.9, 18.78) * mm});
            skLineSegment(sketch, "E677", {"start": v(22.65, -11.6) * mm, "end": v(22.64, -11.8) * mm});
            skLineSegment(sketch, "E678", {"start": v(41.13, -4.14) * mm, "end": v(41.3, -4.3) * mm});
            skLineSegment(sketch, "E679", {"start": v(-88.37, -62.2) * mm, "end": v(-89.2, -61.58) * mm});
            skLineSegment(sketch, "E680", {"start": v(-59.82, -50.29) * mm, "end": v(-59.68, -50.14) * mm});
            skArc(sketch, "E681", {"start": v(-73.37, -48.6) * mm, "mid": v(-73.02, -49.08) * mm, "end": v(-72.43, -49.18) * mm});
            skLineSegment(sketch, "E682", {"start": v(-53.3, -71.78) * mm, "end": v(-53.09, -71.98) * mm});
            skLineSegment(sketch, "E683", {"start": v(20.74, 15.83) * mm, "end": v(20.47, 16.34) * mm});
            skLineSegment(sketch, "E684", {"start": v(31.94, 18.27) * mm, "end": v(31.93, 18.52) * mm});
            skLineSegment(sketch, "E685", {"start": v(22.67, -11.4) * mm, "end": v(22.65, -11.6) * mm});
            skLineSegment(sketch, "E686", {"start": v(40.97, -4) * mm, "end": v(41.13, -4.14) * mm});
            skLineSegment(sketch, "E687", {"start": v(-87.58, -62.69) * mm, "end": v(-88.37, -62.2) * mm});
            skLineSegment(sketch, "E688", {"start": v(-59.93, -50.43) * mm, "end": v(-59.82, -50.29) * mm});
            skArc(sketch, "E689", {"start": v(-71.73, -49.06) * mm, "mid": v(-72.08, -49.12) * mm, "end": v(-72.43, -49.18) * mm});
            skLineSegment(sketch, "E690", {"start": v(-53.5, -71.61) * mm, "end": v(-53.3, -71.78) * mm});
            skArc(sketch, "E691", {"start": v(20.74, 15.83) * mm, "mid": v(21.2, 15.43) * mm, "end": v(21.8, 15.45) * mm});
            skLineSegment(sketch, "E692", {"start": v(31.94, 18.04) * mm, "end": v(31.94, 18.27) * mm});
            skLineSegment(sketch, "E693", {"start": v(22.7, -11.26) * mm, "end": v(22.67, -11.4) * mm});
            skLineSegment(sketch, "E694", {"start": v(40.83, -3.89) * mm, "end": v(40.97, -4) * mm});
            skLineSegment(sketch, "E695", {"start": v(-87.3, -62.82) * mm, "end": v(-87.58, -62.69) * mm});
            skLineSegment(sketch, "E696", {"start": v(-60.25, -50.9) * mm, "end": v(-59.93, -50.43) * mm});
            skArc(sketch, "E697", {"start": v(-71.73, -49.06) * mm, "mid": v(-71.21, -48.76) * mm, "end": v(-71.05, -48.18) * mm});
            skLineSegment(sketch, "E698", {"start": v(-53.68, -71.47) * mm, "end": v(-53.5, -71.61) * mm});
            skArc(sketch, "E699", {"start": v(22.45, 15.72) * mm, "mid": v(22.12, 15.6) * mm, "end": v(21.8, 15.45) * mm});
            skLineSegment(sketch, "E700", {"start": v(31.93, 17.84) * mm, "end": v(31.94, 18.04) * mm});
            skLineSegment(sketch, "E701", {"start": v(22.76, -11.05) * mm, "end": v(22.7, -11.26) * mm});
            skLineSegment(sketch, "E702", {"start": v(40.7, -3.8) * mm, "end": v(40.83, -3.89) * mm});
            skLineSegment(sketch, "E703", {"start": v(-87.04, -62.93) * mm, "end": v(-87.3, -62.82) * mm});
            skArc(sketch, "E704", {"start": v(-56.02, -49.5) * mm, "mid": v(-56.53, -49.06) * mm, "end": v(-57.06, -48.63) * mm});
            skLineSegment(sketch, "E705", {"start": v(-70.54, -45.3) * mm, "end": v(-70.07, -44.4) * mm});
            skLineSegment(sketch, "E706", {"start": v(-53.85, -71.36) * mm, "end": v(-53.68, -71.47) * mm});
            skArc(sketch, "E707", {"start": v(22.45, 15.72) * mm, "mid": v(22.9, 16.13) * mm, "end": v(22.93, 16.73) * mm});
            skLineSegment(sketch, "E708", {"start": v(31.9, 17.65) * mm, "end": v(31.93, 17.84) * mm});
            skLineSegment(sketch, "E709", {"start": v(22.93, -10.5) * mm, "end": v(22.76, -11.05) * mm});
            skLineSegment(sketch, "E710", {"start": v(40.5, -3.7) * mm, "end": v(40.7, -3.8) * mm});
            skLineSegment(sketch, "E711", {"start": v(-86.8, -63.03) * mm, "end": v(-87.04, -62.93) * mm});
            skLineSegment(sketch, "E712", {"start": v(-56.24, -50.51) * mm, "end": v(-56.02, -49.5) * mm});
            skLineSegment(sketch, "E713", {"start": v(-70.88, -46.17) * mm, "end": v(-70.54, -45.3) * mm});
            skLineSegment(sketch, "E714", {"start": v(-54, -71.28) * mm, "end": v(-53.85, -71.36) * mm});
            skLineSegment(sketch, "E715", {"start": v(22.83, 19.67) * mm, "end": v(23.13, 20.63) * mm});
            skLineSegment(sketch, "E716", {"start": v(31.88, 17.5) * mm, "end": v(31.9, 17.65) * mm});
            skLineSegment(sketch, "E717", {"start": v(11.05, 1.4) * mm, "end": v(10.3, 0.9) * mm});
            skArc(sketch, "E718", {"start": v(22.93, -10.5) * mm, "mid": v(22.9, -9.9) * mm, "end": v(22.45, -9.48) * mm});
            skLineSegment(sketch, "E719", {"start": v(40, -3.43) * mm, "end": v(40.5, -3.7) * mm});
            skLineSegment(sketch, "E720", {"start": v(-86.57, -63.1) * mm, "end": v(-86.8, -63.03) * mm});
            skLineSegment(sketch, "E721", {"start": v(-56.54, -51.4) * mm, "end": v(-56.24, -50.51) * mm});
            skLineSegment(sketch, "E722", {"start": v(-70.96, -46.47) * mm, "end": v(-70.88, -46.17) * mm});
            skLineSegment(sketch, "E723", {"start": v(-54.53, -71.04) * mm, "end": v(-54, -71.28) * mm});
            skLineSegment(sketch, "E724", {"start": v(11.29, 1.51) * mm, "end": v(11.05, 1.4) * mm});
            skArc(sketch, "E725", {"start": v(21.8, -9.21) * mm, "mid": v(22.12, -9.35) * mm, "end": v(22.45, -9.48) * mm});
            skArc(sketch, "E726", {"start": v(41.87, -7.42) * mm, "mid": v(42.25, -6.88) * mm, "end": v(42.61, -6.32) * mm});
            skLineSegment(sketch, "E727", {"start": v(-86.38, -63.14) * mm, "end": v(-86.57, -63.1) * mm});
            skLineSegment(sketch, "E728", {"start": v(-56.67, -51.67) * mm, "end": v(-56.54, -51.4) * mm});
            skLineSegment(sketch, "E729", {"start": v(-71.03, -46.74) * mm, "end": v(-70.96, -46.47) * mm});
            skArc(sketch, "E730", {"start": v(-52.42, -74.97) * mm, "mid": v(-52.07, -74.38) * mm, "end": v(-51.74, -73.79) * mm});
            skLineSegment(sketch, "E731", {"start": v(11.5, 1.62) * mm, "end": v(11.29, 1.51) * mm});
            skArc(sketch, "E732", {"start": v(21.8, -9.21) * mm, "mid": v(21.2, -9.19) * mm, "end": v(20.74, -9.58) * mm});
            skLineSegment(sketch, "E733", {"start": v(40.87, -7.33) * mm, "end": v(41.87, -7.42) * mm});
            skLineSegment(sketch, "E734", {"start": v(-86.2, -63.17) * mm, "end": v(-86.38, -63.14) * mm});
            skLineSegment(sketch, "E735", {"start": v(-56.8, -51.93) * mm, "end": v(-56.67, -51.67) * mm});
            skLineSegment(sketch, "E736", {"start": v(-71.07, -47) * mm, "end": v(-71.03, -46.74) * mm});
            skLineSegment(sketch, "E737", {"start": v(-53.45, -74.92) * mm, "end": v(-52.42, -74.97) * mm});
            skLineSegment(sketch, "E738", {"start": v(11.72, 1.7) * mm, "end": v(11.5, 1.62) * mm});
            skLineSegment(sketch, "E739", {"start": v(18.74, -11.73) * mm, "end": v(17.85, -12.2) * mm});
            skLineSegment(sketch, "E740", {"start": v(39.99, -7.13) * mm, "end": v(40.87, -7.33) * mm});
            skLineSegment(sketch, "E741", {"start": v(-85.63, -63.2) * mm, "end": v(-86.2, -63.17) * mm});
            skLineSegment(sketch, "E742", {"start": v(-56.92, -52.15) * mm, "end": v(-56.8, -51.93) * mm});
            skLineSegment(sketch, "E743", {"start": v(11.89, 7.76) * mm, "end": v(11.63, 7.74) * mm});
            skLineSegment(sketch, "E744", {"start": v(-71.1, -47.24) * mm, "end": v(-71.07, -47) * mm});
            skLineSegment(sketch, "E745", {"start": v(-54.36, -74.78) * mm, "end": v(-53.45, -74.92) * mm});
            skLineSegment(sketch, "E746", {"start": v(11.92, 1.78) * mm, "end": v(11.72, 1.7) * mm});
            skLineSegment(sketch, "E747", {"start": v(19.48, -11.21) * mm, "end": v(18.74, -11.73) * mm});
            skLineSegment(sketch, "E748", {"start": v(39.74, -7.06) * mm, "end": v(39.99, -7.13) * mm});
            skArc(sketch, "E749", {"start": v(-88.95, -60.24) * mm, "mid": v(-89.08, -60.91) * mm, "end": v(-89.2, -61.58) * mm});
            skLineSegment(sketch, "E750", {"start": v(-57.05, -52.35) * mm, "end": v(-56.92, -52.15) * mm});
            skLineSegment(sketch, "E751", {"start": v(12.14, 7.77) * mm, "end": v(11.89, 7.76) * mm});
            skLineSegment(sketch, "E752", {"start": v(-71.12, -47.43) * mm, "end": v(-71.1, -47.24) * mm});
            skLineSegment(sketch, "E753", {"start": v(-54.66, -74.7) * mm, "end": v(-54.36, -74.78) * mm});
            skLineSegment(sketch, "E754", {"start": v(12.1, 1.83) * mm, "end": v(11.92, 1.78) * mm});
            skLineSegment(sketch, "E755", {"start": v(19.68, -11.05) * mm, "end": v(19.48, -11.21) * mm});
            skLineSegment(sketch, "E756", {"start": v(39.5, -6.97) * mm, "end": v(39.74, -7.06) * mm});
            skLineSegment(sketch, "E757", {"start": v(-87.97, -59.93) * mm, "end": v(-88.95, -60.24) * mm});
            skLineSegment(sketch, "E758", {"start": v(-57.17, -52.51) * mm, "end": v(-57.05, -52.35) * mm});
            skLineSegment(sketch, "E759", {"start": v(12.36, 7.77) * mm, "end": v(12.14, 7.77) * mm});
            skLineSegment(sketch, "E760", {"start": v(-71.1, -47.62) * mm, "end": v(-71.12, -47.43) * mm});
            skLineSegment(sketch, "E761", {"start": v(-54.93, -74.62) * mm, "end": v(-54.66, -74.7) * mm});
            skLineSegment(sketch, "E762", {"start": v(12.24, 1.86) * mm, "end": v(12.1, 1.83) * mm});
            skLineSegment(sketch, "E763", {"start": v(19.86, -10.88) * mm, "end": v(19.68, -11.05) * mm});
            skLineSegment(sketch, "E764", {"start": v(39.3, -6.89) * mm, "end": v(39.5, -6.97) * mm});
            skLineSegment(sketch, "E765", {"start": v(-87.06, -59.76) * mm, "end": v(-87.97, -59.93) * mm});
            skLineSegment(sketch, "E766", {"start": v(-57.3, -52.64) * mm, "end": v(-57.17, -52.51) * mm});
            skLineSegment(sketch, "E767", {"start": v(12.57, 7.76) * mm, "end": v(12.36, 7.77) * mm});
            skLineSegment(sketch, "E768", {"start": v(-71.05, -48.18) * mm, "end": v(-71.1, -47.62) * mm});
            skLineSegment(sketch, "E769", {"start": v(-55.18, -74.53) * mm, "end": v(-54.93, -74.62) * mm});
            skLineSegment(sketch, "E770", {"start": v(12.47, 1.89) * mm, "end": v(12.24, 1.86) * mm});
            skLineSegment(sketch, "E771", {"start": v(20.02, -10.72) * mm, "end": v(19.86, -10.88) * mm});
            skLineSegment(sketch, "E772", {"start": v(39.1, -6.8) * mm, "end": v(39.3, -6.89) * mm});
            skLineSegment(sketch, "E773", {"start": v(-86.76, -59.72) * mm, "end": v(-87.06, -59.76) * mm});
            skLineSegment(sketch, "E774", {"start": v(12.76, 7.74) * mm, "end": v(12.57, 7.76) * mm});
            skArc(sketch, "E775", {"start": v(-68.7, -44.4) * mm, "mid": v(-69.39, -44.38) * mm, "end": v(-70.07, -44.4) * mm});
            skLineSegment(sketch, "E776", {"start": v(-55.4, -74.44) * mm, "end": v(-55.18, -74.53) * mm});
            skLineSegment(sketch, "E777", {"start": v(-70.96, -82.3) * mm, "end": v(-70.88, -82.6) * mm});
            skLineSegment(sketch, "E778", {"start": v(13.04, 1.94) * mm, "end": v(12.47, 1.89) * mm});
            skLineSegment(sketch, "E779", {"start": v(20.16, -10.56) * mm, "end": v(20.02, -10.72) * mm});
            skLineSegment(sketch, "E780", {"start": v(38.94, -6.7) * mm, "end": v(39.1, -6.8) * mm});
            skLineSegment(sketch, "E781", {"start": v(-86.47, -59.7) * mm, "end": v(-86.76, -59.72) * mm});
            skArc(sketch, "E782", {"start": v(-57.7, -53.04) * mm, "mid": v(-57.94, -53.59) * mm, "end": v(-57.75, -54.15) * mm});
            skLineSegment(sketch, "E783", {"start": v(12.9, 7.72) * mm, "end": v(12.76, 7.74) * mm});
            skLineSegment(sketch, "E784", {"start": v(-68.23, -45.3) * mm, "end": v(-68.7, -44.4) * mm});
            skLineSegment(sketch, "E785", {"start": v(-55.57, -74.35) * mm, "end": v(-55.4, -74.44) * mm});
            skLineSegment(sketch, "E786", {"start": v(-71.03, -82.02) * mm, "end": v(-70.96, -82.3) * mm});
            skArc(sketch, "E787", {"start": v(13.04, 1.94) * mm, "mid": v(13.58, 2.2) * mm, "end": v(13.8, 2.77) * mm});
            skLineSegment(sketch, "E788", {"start": v(20.28, -10.42) * mm, "end": v(20.16, -10.56) * mm});
            skLineSegment(sketch, "E789", {"start": v(38.82, -6.63) * mm, "end": v(38.94, -6.7) * mm});
            skLineSegment(sketch, "E790", {"start": v(-86.21, -59.7) * mm, "end": v(-86.47, -59.7) * mm});
            skArc(sketch, "E791", {"start": v(-57.29, -54.7) * mm, "mid": v(-57.51, -54.42) * mm, "end": v(-57.75, -54.15) * mm});
            skLineSegment(sketch, "E792", {"start": v(13.12, 7.65) * mm, "end": v(12.9, 7.72) * mm});
            skLineSegment(sketch, "E793", {"start": v(-67.9, -46.17) * mm, "end": v(-68.23, -45.3) * mm});
            skLineSegment(sketch, "E794", {"start": v(-55.73, -74.26) * mm, "end": v(-55.57, -74.35) * mm});
            skLineSegment(sketch, "E795", {"start": v(-71.07, -81.76) * mm, "end": v(-71.03, -82.02) * mm});
            skArc(sketch, "E796", {"start": v(13.8, 3.47) * mm, "mid": v(13.79, 3.12) * mm, "end": v(13.8, 2.77) * mm});
            skLineSegment(sketch, "E797", {"start": v(20.36, -10.3) * mm, "end": v(20.28, -10.42) * mm});
            skLineSegment(sketch, "E798", {"start": v(38.64, -6.49) * mm, "end": v(38.82, -6.63) * mm});
            skLineSegment(sketch, "E799", {"start": v(-85.98, -59.72) * mm, "end": v(-86.21, -59.7) * mm});
            skArc(sketch, "E800", {"start": v(-57.29, -54.7) * mm, "mid": v(-56.77, -54.99) * mm, "end": v(-56.19, -54.84) * mm});
            skLineSegment(sketch, "E801", {"start": v(13.67, 7.48) * mm, "end": v(13.12, 7.65) * mm});
            skLineSegment(sketch, "E802", {"start": v(-67.81, -46.47) * mm, "end": v(-67.9, -46.17) * mm});
            skLineSegment(sketch, "E803", {"start": v(-56.19, -73.92) * mm, "end": v(-55.73, -74.26) * mm});
            skLineSegment(sketch, "E804", {"start": v(-71.1, -81.53) * mm, "end": v(-71.07, -81.76) * mm});
            skArc(sketch, "E805", {"start": v(13.8, 3.47) * mm, "mid": v(13.58, 4.04) * mm, "end": v(13.04, 4.3) * mm});
            skLineSegment(sketch, "E806", {"start": v(20.47, -10.1) * mm, "end": v(20.36, -10.3) * mm});
            skLineSegment(sketch, "E807", {"start": v(38.2, -6.11) * mm, "end": v(38.64, -6.49) * mm});
            skLineSegment(sketch, "E808", {"start": v(-85.78, -59.74) * mm, "end": v(-85.98, -59.72) * mm});
            skLineSegment(sketch, "E809", {"start": v(-53.45, -53.85) * mm, "end": v(-52.42, -53.8) * mm});
            skArc(sketch, "E810", {"start": v(13.67, 7.48) * mm, "mid": v(14.28, 7.52) * mm, "end": v(14.68, 7.96) * mm});
            skLineSegment(sketch, "E811", {"start": v(-67.75, -46.74) * mm, "end": v(-67.81, -46.47) * mm});
            skArc(sketch, "E812", {"start": v(-56.19, -73.92) * mm, "mid": v(-56.77, -73.78) * mm, "end": v(-57.29, -74.07) * mm});
            skLineSegment(sketch, "E813", {"start": v(-71.12, -81.33) * mm, "end": v(-71.1, -81.53) * mm});
            skLineSegment(sketch, "E814", {"start": v(10.3, 5.34) * mm, "end": v(9.52, 5.98) * mm});
            skArc(sketch, "E815", {"start": v(38.2, -6.11) * mm, "mid": v(37.63, -5.92) * mm, "end": v(37.08, -6.17) * mm});
            skLineSegment(sketch, "E816", {"start": v(-85.6, -59.78) * mm, "end": v(-85.78, -59.74) * mm});
            skLineSegment(sketch, "E817", {"start": v(-54.36, -54) * mm, "end": v(-53.45, -53.85) * mm});
            skArc(sketch, "E818", {"start": v(14.95, 8.61) * mm, "mid": v(14.82, 8.29) * mm, "end": v(14.68, 7.96) * mm});
            skLineSegment(sketch, "E819", {"start": v(-67.7, -47) * mm, "end": v(-67.75, -46.74) * mm});
            skArc(sketch, "E820", {"start": v(-57.75, -74.62) * mm, "mid": v(-57.51, -74.35) * mm, "end": v(-57.29, -74.07) * mm});
            skLineSegment(sketch, "E821", {"start": v(-71.1, -81.15) * mm, "end": v(-71.12, -81.33) * mm});
            skLineSegment(sketch, "E822", {"start": v(11.05, 4.85) * mm, "end": v(10.3, 5.34) * mm});
            skArc(sketch, "E823", {"start": v(16.74, -11.47) * mm, "mid": v(17.29, -11.84) * mm, "end": v(17.85, -12.2) * mm});
            skLineSegment(sketch, "E824", {"start": v(-85.05, -59.93) * mm, "end": v(-85.6, -59.78) * mm});
            skLineSegment(sketch, "E825", {"start": v(-54.66, -54.06) * mm, "end": v(-54.36, -54) * mm});
            skArc(sketch, "E826", {"start": v(14.95, 8.61) * mm, "mid": v(14.98, 9.21) * mm, "end": v(14.58, 9.67) * mm});
            skLineSegment(sketch, "E827", {"start": v(-67.67, -47.24) * mm, "end": v(-67.7, -47) * mm});
            skArc(sketch, "E828", {"start": v(-57.75, -74.62) * mm, "mid": v(-57.94, -75.18) * mm, "end": v(-57.7, -75.72) * mm});
            skLineSegment(sketch, "E829", {"start": v(-71.05, -80.58) * mm, "end": v(-71.1, -81.15) * mm});
            skLineSegment(sketch, "E830", {"start": v(11.29, 4.73) * mm, "end": v(11.05, 4.85) * mm});
            skLineSegment(sketch, "E831", {"start": v(16.84, -10.46) * mm, "end": v(16.74, -11.47) * mm});
            skArc(sketch, "E832", {"start": v(-85.05, -59.93) * mm, "mid": v(-84.46, -59.87) * mm, "end": v(-84.07, -59.42) * mm});
            skLineSegment(sketch, "E833", {"start": v(-54.93, -54.14) * mm, "end": v(-54.66, -54.06) * mm});
            skLineSegment(sketch, "E834", {"start": v(12.44, 11.67) * mm, "end": v(11.96, 12.56) * mm});
            skLineSegment(sketch, "E835", {"start": v(-67.66, -47.43) * mm, "end": v(-67.67, -47.24) * mm});
            skLineSegment(sketch, "E836", {"start": v(-56.24, -78.25) * mm, "end": v(-56.02, -79.26) * mm});
            skArc(sketch, "E837", {"start": v(-71.05, -80.58) * mm, "mid": v(-71.21, -80) * mm, "end": v(-71.73, -79.7) * mm});
            skLineSegment(sketch, "E838", {"start": v(11.5, 4.62) * mm, "end": v(11.29, 4.73) * mm});
            skLineSegment(sketch, "E839", {"start": v(17.03, -9.58) * mm, "end": v(16.84, -10.46) * mm});
            skArc(sketch, "E840", {"start": v(-83.83, -58.75) * mm, "mid": v(-83.95, -59.08) * mm, "end": v(-84.07, -59.42) * mm});
            skLineSegment(sketch, "E841", {"start": v(-55.18, -54.23) * mm, "end": v(-54.93, -54.14) * mm});
            skLineSegment(sketch, "E842", {"start": v(12.95, 10.93) * mm, "end": v(12.44, 11.67) * mm});
            skLineSegment(sketch, "E843", {"start": v(-67.67, -47.62) * mm, "end": v(-67.66, -47.43) * mm});
            skLineSegment(sketch, "E844", {"start": v(-56.54, -77.38) * mm, "end": v(-56.24, -78.25) * mm});
            skArc(sketch, "E845", {"start": v(-72.43, -79.58) * mm, "mid": v(-72.08, -79.65) * mm, "end": v(-71.73, -79.7) * mm});
            skLineSegment(sketch, "E846", {"start": v(11.72, 4.54) * mm, "end": v(11.5, 4.62) * mm});
            skArc(sketch, "E847", {"start": v(45.06, 5.98) * mm, "mid": v(44.94, 6.63) * mm, "end": v(44.8, 7.28) * mm});
            skArc(sketch, "E848", {"start": v(32.13, -9.48) * mm, "mid": v(32.45, -9.35) * mm, "end": v(32.78, -9.21) * mm});
            skLineSegment(sketch, "E849", {"start": v(17.1, -9.33) * mm, "end": v(17.03, -9.58) * mm});
            skArc(sketch, "E850", {"start": v(-83.83, -58.75) * mm, "mid": v(-83.83, -58.15) * mm, "end": v(-84.25, -57.72) * mm});
            skLineSegment(sketch, "E851", {"start": v(-55.4, -54.32) * mm, "end": v(-55.18, -54.23) * mm});
            skLineSegment(sketch, "E852", {"start": v(13.12, 10.73) * mm, "end": v(12.95, 10.93) * mm});
            skLineSegment(sketch, "E853", {"start": v(-67.72, -48.18) * mm, "end": v(-67.67, -47.62) * mm});
            skLineSegment(sketch, "E854", {"start": v(-56.67, -77.1) * mm, "end": v(-56.54, -77.38) * mm});
            skArc(sketch, "E855", {"start": v(-72.43, -79.58) * mm, "mid": v(-73.02, -79.7) * mm, "end": v(-73.37, -80.18) * mm});
            skLineSegment(sketch, "E856", {"start": v(11.92, 4.47) * mm, "end": v(11.72, 4.54) * mm});
            skLineSegment(sketch, "E857", {"start": v(44.28, 5.34) * mm, "end": v(45.06, 5.98) * mm});
            skArc(sketch, "E858", {"start": v(32.13, -9.48) * mm, "mid": v(31.68, -9.9) * mm, "end": v(31.64, -10.5) * mm});
            skLineSegment(sketch, "E859", {"start": v(17.2, -9.1) * mm, "end": v(17.1, -9.33) * mm});
            skLineSegment(sketch, "E860", {"start": v(-86.48, -55.85) * mm, "end": v(-87.04, -54.98) * mm});
            skLineSegment(sketch, "E861", {"start": v(-55.57, -54.41) * mm, "end": v(-55.4, -54.32) * mm});
            skLineSegment(sketch, "E862", {"start": v(13.28, 10.55) * mm, "end": v(13.12, 10.73) * mm});
            skArc(sketch, "E863", {"start": v(-67.72, -48.18) * mm, "mid": v(-67.56, -48.76) * mm, "end": v(-67.05, -49.06) * mm});
            skLineSegment(sketch, "E864", {"start": v(-56.8, -76.84) * mm, "end": v(-56.67, -77.1) * mm});
            skLineSegment(sketch, "E865", {"start": v(-74.83, -82.7) * mm, "end": v(-75.59, -83.4) * mm});
            skLineSegment(sketch, "E866", {"start": v(12.1, 4.41) * mm, "end": v(11.92, 4.47) * mm});
            skLineSegment(sketch, "E867", {"start": v(43.52, 4.85) * mm, "end": v(44.28, 5.34) * mm});
            skLineSegment(sketch, "E868", {"start": v(31.74, -13.43) * mm, "end": v(31.45, -14.4) * mm});
            skLineSegment(sketch, "E869", {"start": v(17.28, -8.89) * mm, "end": v(17.2, -9.1) * mm});
            skLineSegment(sketch, "E870", {"start": v(-85.9, -56.57) * mm, "end": v(-86.48, -55.85) * mm});
            skLineSegment(sketch, "E871", {"start": v(-55.73, -54.5) * mm, "end": v(-55.57, -54.41) * mm});
            skLineSegment(sketch, "E872", {"start": v(13.45, 10.38) * mm, "end": v(13.28, 10.55) * mm});
            skLineSegment(sketch, "E873", {"start": v(-56.92, -76.61) * mm, "end": v(-56.8, -76.84) * mm});
            skLineSegment(sketch, "E874", {"start": v(-74.22, -82) * mm, "end": v(-74.83, -82.7) * mm});
            skLineSegment(sketch, "E875", {"start": v(12.24, 4.38) * mm, "end": v(12.1, 4.41) * mm});
            skLineSegment(sketch, "E876", {"start": v(17.37, -8.7) * mm, "end": v(17.28, -8.89) * mm});
            skLineSegment(sketch, "E877", {"start": v(-85.7, -56.79) * mm, "end": v(-85.9, -56.57) * mm});
            skLineSegment(sketch, "E878", {"start": v(-56.19, -54.84) * mm, "end": v(-55.73, -54.5) * mm});
            skLineSegment(sketch, "E879", {"start": v(13.6, 10.24) * mm, "end": v(13.45, 10.38) * mm});
            skLineSegment(sketch, "E880", {"start": v(-57.05, -76.42) * mm, "end": v(-56.92, -76.61) * mm});
            skLineSegment(sketch, "E881", {"start": v(-74.04, -81.76) * mm, "end": v(-74.22, -82) * mm});
            skLineSegment(sketch, "E882", {"start": v(12.47, 4.36) * mm, "end": v(12.24, 4.38) * mm});
            skLineSegment(sketch, "E883", {"start": v(17.46, -8.54) * mm, "end": v(17.37, -8.7) * mm});
            skLineSegment(sketch, "E884", {"start": v(-85.48, -56.98) * mm, "end": v(-85.7, -56.79) * mm});
            skArc(sketch, "E885", {"start": v(-51.74, -54.98) * mm, "mid": v(-52.07, -54.38) * mm, "end": v(-52.42, -53.8) * mm});
            skLineSegment(sketch, "E886", {"start": v(13.75, 10.13) * mm, "end": v(13.6, 10.24) * mm});
            skLineSegment(sketch, "E887", {"start": v(-57.17, -76.26) * mm, "end": v(-57.05, -76.42) * mm});
            skLineSegment(sketch, "E888", {"start": v(-73.88, -81.52) * mm, "end": v(-74.04, -81.76) * mm});
            skLineSegment(sketch, "E889", {"start": v(13.04, 4.3) * mm, "end": v(12.47, 4.36) * mm});
            skLineSegment(sketch, "E890", {"start": v(17.54, -8.41) * mm, "end": v(17.46, -8.54) * mm});
            skLineSegment(sketch, "E891", {"start": v(-85.28, -57.15) * mm, "end": v(-85.48, -56.98) * mm});
            skLineSegment(sketch, "E892", {"start": v(13.87, 10.04) * mm, "end": v(13.75, 10.13) * mm});
            skLineSegment(sketch, "E893", {"start": v(-57.3, -76.12) * mm, "end": v(-57.17, -76.26) * mm});
            skLineSegment(sketch, "E894", {"start": v(-73.75, -81.3) * mm, "end": v(-73.88, -81.52) * mm});
            skArc(sketch, "E895", {"start": v(9.78, 7.28) * mm, "mid": v(9.63, 6.63) * mm, "end": v(9.52, 5.98) * mm});
            skLineSegment(sketch, "E896", {"start": v(17.68, -8.23) * mm, "end": v(17.54, -8.41) * mm});
            skLineSegment(sketch, "E897", {"start": v(-85.1, -57.3) * mm, "end": v(-85.28, -57.15) * mm});
            skLineSegment(sketch, "E898", {"start": v(-52.87, -56.57) * mm, "end": v(-52.3, -55.85) * mm});
            skLineSegment(sketch, "E899", {"start": v(14.07, 9.94) * mm, "end": v(13.87, 10.04) * mm});
            skLineSegment(sketch, "E900", {"start": v(-57.7, -75.72) * mm, "end": v(-57.3, -76.12) * mm});
            skLineSegment(sketch, "E901", {"start": v(-73.64, -81.08) * mm, "end": v(-73.75, -81.3) * mm});
            skLineSegment(sketch, "E902", {"start": v(10.74, 7.58) * mm, "end": v(9.78, 7.28) * mm});
            skLineSegment(sketch, "E903", {"start": v(18.06, -7.79) * mm, "end": v(17.68, -8.23) * mm});
            skLineSegment(sketch, "E904", {"start": v(-84.93, -57.4) * mm, "end": v(-85.1, -57.3) * mm});
            skLineSegment(sketch, "E905", {"start": v(-53.09, -56.79) * mm, "end": v(-52.87, -56.57) * mm});
            skLineSegment(sketch, "E906", {"start": v(14.58, 9.67) * mm, "end": v(14.07, 9.94) * mm});
            skArc(sketch, "E907", {"start": v(-57.06, -80.13) * mm, "mid": v(-56.53, -79.7) * mm, "end": v(-56.02, -79.26) * mm});
            skLineSegment(sketch, "E908", {"start": v(-73.56, -80.9) * mm, "end": v(-73.64, -81.08) * mm});
            skLineSegment(sketch, "E909", {"start": v(11.63, 7.74) * mm, "end": v(10.74, 7.58) * mm});
            skArc(sketch, "E910", {"start": v(18.06, -7.79) * mm, "mid": v(18.25, -7.22) * mm, "end": v(18, -6.67) * mm});
            skLineSegment(sketch, "E911", {"start": v(-84.77, -57.49) * mm, "end": v(-84.93, -57.4) * mm});
            skLineSegment(sketch, "E912", {"start": v(-53.3, -56.98) * mm, "end": v(-53.09, -56.79) * mm});
            skLineSegment(sketch, "E913", {"start": v(22.67, 18.78) * mm, "end": v(22.83, 19.67) * mm});
            skLineSegment(sketch, "E914", {"start": v(31.82, 17.29) * mm, "end": v(31.88, 17.5) * mm});
            skLineSegment(sketch, "E915", {"start": v(22.65, 18.52) * mm, "end": v(22.67, 18.78) * mm});
            skLineSegment(sketch, "E916", {"start": v(31.64, 16.73) * mm, "end": v(31.82, 17.29) * mm});
            skLineSegment(sketch, "E917", {"start": v(22.64, 18.27) * mm, "end": v(22.65, 18.52) * mm});
            skArc(sketch, "E918", {"start": v(31.64, 16.73) * mm, "mid": v(31.68, 16.13) * mm, "end": v(32.13, 15.72) * mm});
            skLineSegment(sketch, "E919", {"start": v(-73.5, -80.73) * mm, "end": v(-73.56, -80.9) * mm});
            skLineSegment(sketch, "E920", {"start": v(-73.37, -80.18) * mm, "end": v(-73.5, -80.73) * mm});
            skArc(sketch, "E921", {"start": v(-76.86, -82.93) * mm, "mid": v(-76.23, -83.18) * mm, "end": v(-75.59, -83.4) * mm});
            skLineSegment(sketch, "E922", {"start": v(-77, -81.91) * mm, "end": v(-76.86, -82.93) * mm});
            skLineSegment(sketch, "E923", {"start": v(-77.01, -80.99) * mm, "end": v(-77, -81.91) * mm});
            skLineSegment(sketch, "E924", {"start": v(-77, -80.68) * mm, "end": v(-77.01, -80.99) * mm});
            skLineSegment(sketch, "E925", {"start": v(-70.9, 75.88) * mm, "end": v(-70.91, 76.05) * mm});
            skLineSegment(sketch, "E926", {"start": v(-76.96, -80.4) * mm, "end": v(-77, -80.68) * mm});
            skLineSegment(sketch, "E927", {"start": v(-70.89, 75.73) * mm, "end": v(-70.9, 75.88) * mm});
            skLineSegment(sketch, "E928", {"start": v(-76.92, -80.14) * mm, "end": v(-76.96, -80.4) * mm});
            skLineSegment(sketch, "E929", {"start": v(-70.89, 75.62) * mm, "end": v(-70.89, 75.73) * mm});
            skLineSegment(sketch, "E930", {"start": v(-76.87, -79.91) * mm, "end": v(-76.92, -80.14) * mm});
            skLineSegment(sketch, "E931", {"start": v(-70.92, 75.32) * mm, "end": v(-70.89, 75.62) * mm});
            skLineSegment(sketch, "E932", {"start": v(-76.8, -79.72) * mm, "end": v(-76.87, -79.91) * mm});
            skLineSegment(sketch, "E933", {"start": v(-71, 74.74) * mm, "end": v(-70.92, 75.32) * mm});
            skArc(sketch, "E934", {"start": v(-71, 74.74) * mm, "mid": v(-70.85, 74.15) * mm, "end": v(-70.34, 73.83) * mm});
            skArc(sketch, "E935", {"start": v(-69.66, 73.67) * mm, "mid": v(-70, 73.75) * mm, "end": v(-70.34, 73.83) * mm});
            skArc(sketch, "E936", {"start": v(-69.66, 73.67) * mm, "mid": v(-69.06, 73.75) * mm, "end": v(-68.67, 74.2) * mm});
            skLineSegment(sketch, "E937", {"start": v(-67, 76.66) * mm, "end": v(-66.2, 77.23) * mm});
            skLineSegment(sketch, "E938", {"start": v(-67.66, 76.07) * mm, "end": v(-67, 76.66) * mm});
            skLineSegment(sketch, "E939", {"start": v(37.04, -8.41) * mm, "end": v(37.12, -8.54) * mm});
            skLineSegment(sketch, "E940", {"start": v(40.5, 9.94) * mm, "end": v(40.7, 10.04) * mm});
            skArc(sketch, "E941", {"start": v(-82.76, -79.26) * mm, "mid": v(-82.24, -79.7) * mm, "end": v(-81.72, -80.13) * mm});
            skLineSegment(sketch, "E942", {"start": v(37.12, -8.54) * mm, "end": v(37.2, -8.7) * mm});
            skLineSegment(sketch, "E943", {"start": v(40.7, 10.04) * mm, "end": v(40.83, 10.13) * mm});
            skLineSegment(sketch, "E944", {"start": v(-78.53, -77.86) * mm, "end": v(-78.85, -78.33) * mm});
            skLineSegment(sketch, "E945", {"start": v(37.2, -8.7) * mm, "end": v(37.3, -8.89) * mm});
            skLineSegment(sketch, "E946", {"start": v(40.83, 10.13) * mm, "end": v(40.97, 10.24) * mm});
            skLineSegment(sketch, "E947", {"start": v(-78.85, -78.33) * mm, "end": v(-78.96, -78.48) * mm});
            skLineSegment(sketch, "E948", {"start": v(37.3, -8.89) * mm, "end": v(37.38, -9.1) * mm});
            skLineSegment(sketch, "E949", {"start": v(40.97, 10.24) * mm, "end": v(41.13, 10.38) * mm});
            skLineSegment(sketch, "E950", {"start": v(-78.96, -78.48) * mm, "end": v(-79.1, -78.62) * mm});
            skLineSegment(sketch, "E951", {"start": v(37.38, -9.1) * mm, "end": v(37.47, -9.33) * mm});
            skLineSegment(sketch, "E952", {"start": v(41.13, 10.38) * mm, "end": v(41.3, 10.55) * mm});
            skLineSegment(sketch, "E953", {"start": v(-79.1, -78.62) * mm, "end": v(-79.27, -78.78) * mm});
            skLineSegment(sketch, "E954", {"start": v(37.47, -9.33) * mm, "end": v(37.54, -9.58) * mm});
            skLineSegment(sketch, "E955", {"start": v(41.3, 10.55) * mm, "end": v(41.46, 10.73) * mm});
            skLineSegment(sketch, "E956", {"start": v(-79.27, -78.78) * mm, "end": v(-79.47, -78.95) * mm});
            skLineSegment(sketch, "E957", {"start": v(37.54, -9.58) * mm, "end": v(37.74, -10.46) * mm});
            skLineSegment(sketch, "E958", {"start": v(41.46, 10.73) * mm, "end": v(41.62, 10.93) * mm});
            skLineSegment(sketch, "E959", {"start": v(-79.47, -78.95) * mm, "end": v(-79.7, -79.12) * mm});
            skLineSegment(sketch, "E960", {"start": v(37.74, -10.46) * mm, "end": v(37.83, -11.47) * mm});
            skLineSegment(sketch, "E961", {"start": v(41.62, 10.93) * mm, "end": v(42.14, 11.67) * mm});
            skLineSegment(sketch, "E962", {"start": v(-79.7, -79.12) * mm, "end": v(-79.95, -79.29) * mm});
            skArc(sketch, "E963", {"start": v(36.58, -6.67) * mm, "mid": v(36.33, -7.22) * mm, "end": v(36.52, -7.79) * mm});
            skLineSegment(sketch, "E964", {"start": v(42.14, 11.67) * mm, "end": v(42.61, 12.56) * mm});
            skLineSegment(sketch, "E965", {"start": v(-79.95, -79.29) * mm, "end": v(-80.76, -79.74) * mm});
            skArc(sketch, "E966", {"start": v(36.58, -6.67) * mm, "mid": v(36.83, -6.42) * mm, "end": v(37.08, -6.17) * mm});
            skArc(sketch, "E967", {"start": v(42.61, 12.56) * mm, "mid": v(42.25, 13.12) * mm, "end": v(41.87, 13.67) * mm});
            skLineSegment(sketch, "E968", {"start": v(-80.76, -79.74) * mm, "end": v(-81.72, -80.13) * mm});
            skLineSegment(sketch, "E969", {"start": v(38.2, 12.35) * mm, "end": v(38.64, 12.73) * mm});
            skArc(sketch, "E970", {"start": v(-77.44, -77.63) * mm, "mid": v(-78.03, -77.53) * mm, "end": v(-78.53, -77.86) * mm});
            skLineSegment(sketch, "E971", {"start": v(38.64, 12.73) * mm, "end": v(38.82, 12.87) * mm});
            skArc(sketch, "E972", {"start": v(-77.44, -77.63) * mm, "mid": v(-77.14, -77.8) * mm, "end": v(-76.83, -77.98) * mm});
            skLineSegment(sketch, "E973", {"start": v(38.82, 12.87) * mm, "end": v(38.94, 12.95) * mm});
            skArc(sketch, "E974", {"start": v(-76.5, -79.04) * mm, "mid": v(-76.45, -78.44) * mm, "end": v(-76.83, -77.98) * mm});
            skLineSegment(sketch, "E975", {"start": v(38.94, 12.95) * mm, "end": v(39.1, 13.04) * mm});
            skLineSegment(sketch, "E976", {"start": v(-76.5, -79.04) * mm, "end": v(-76.74, -79.55) * mm});
            skLineSegment(sketch, "E977", {"start": v(39.1, 13.04) * mm, "end": v(39.3, 13.13) * mm});
            skLineSegment(sketch, "E978", {"start": v(-76.74, -79.55) * mm, "end": v(-76.8, -79.72) * mm});
            skLineSegment(sketch, "E979", {"start": v(39.3, 13.13) * mm, "end": v(39.5, 13.22) * mm});
            skLineSegment(sketch, "E980", {"start": v(39.5, 13.22) * mm, "end": v(39.74, 13.3) * mm});
            skLineSegment(sketch, "E981", {"start": v(39.74, 13.3) * mm, "end": v(39.99, 13.38) * mm});
            skLineSegment(sketch, "E982", {"start": v(39.99, 13.38) * mm, "end": v(40.87, 13.57) * mm});
            skLineSegment(sketch, "E983", {"start": v(40.87, 13.57) * mm, "end": v(41.87, 13.67) * mm});
            skArc(sketch, "E984", {"start": v(37.08, 12.41) * mm, "mid": v(37.63, 12.16) * mm, "end": v(38.2, 12.35) * mm});
            skArc(sketch, "E985", {"start": v(37.08, 12.41) * mm, "mid": v(36.83, 12.67) * mm, "end": v(36.58, 12.91) * mm});
            skArc(sketch, "E986", {"start": v(36.52, 14.03) * mm, "mid": v(36.33, 13.46) * mm, "end": v(36.58, 12.91) * mm});
            skLineSegment(sketch, "E987", {"start": v(36.52, 14.03) * mm, "end": v(36.9, 14.48) * mm});
            skLineSegment(sketch, "E988", {"start": v(36.9, 14.48) * mm, "end": v(37.04, 14.65) * mm});
            skLineSegment(sketch, "E989", {"start": v(37.04, 14.65) * mm, "end": v(37.12, 14.78) * mm});
            skLineSegment(sketch, "E990", {"start": v(37.12, 14.78) * mm, "end": v(37.2, 14.94) * mm});
            skLineSegment(sketch, "E991", {"start": v(37.2, 14.94) * mm, "end": v(37.3, 15.13) * mm});
            skLineSegment(sketch, "E992", {"start": v(37.3, 15.13) * mm, "end": v(37.38, 15.34) * mm});
            skLineSegment(sketch, "E993", {"start": v(37.38, 15.34) * mm, "end": v(37.47, 15.57) * mm});
            skLineSegment(sketch, "E994", {"start": v(37.47, 15.57) * mm, "end": v(37.54, 15.82) * mm});
            skLineSegment(sketch, "E995", {"start": v(37.54, 15.82) * mm, "end": v(37.74, 16.7) * mm});
            skLineSegment(sketch, "E996", {"start": v(37.74, 16.7) * mm, "end": v(37.83, 17.7) * mm});
            skArc(sketch, "E997", {"start": v(37.83, 17.7) * mm, "mid": v(37.29, 18.09) * mm, "end": v(36.73, 18.45) * mm});
            skLineSegment(sketch, "E998", {"start": v(33.83, 15.83) * mm, "end": v(34.1, 16.34) * mm});
            skLineSegment(sketch, "E999", {"start": v(34.1, 16.34) * mm, "end": v(34.21, 16.54) * mm});
            skLineSegment(sketch, "E1000", {"start": v(34.21, 16.54) * mm, "end": v(34.3, 16.66) * mm});
            skLineSegment(sketch, "E1001", {"start": v(34.3, 16.66) * mm, "end": v(34.41, 16.8) * mm});
            skLineSegment(sketch, "E1002", {"start": v(34.41, 16.8) * mm, "end": v(34.55, 16.96) * mm});
            skLineSegment(sketch, "E1003", {"start": v(34.55, 16.96) * mm, "end": v(34.71, 17.12) * mm});
            skLineSegment(sketch, "E1004", {"start": v(34.71, 17.12) * mm, "end": v(34.9, 17.3) * mm});
            skLineSegment(sketch, "E1005", {"start": v(34.9, 17.3) * mm, "end": v(35.1, 17.46) * mm});
            skLineSegment(sketch, "E1006", {"start": v(35.1, 17.46) * mm, "end": v(35.84, 17.97) * mm});
            skLineSegment(sketch, "E1007", {"start": v(35.84, 17.97) * mm, "end": v(36.73, 18.45) * mm});
            skArc(sketch, "E1008", {"start": v(32.78, 15.45) * mm, "mid": v(33.38, 15.43) * mm, "end": v(33.83, 15.83) * mm});
            skArc(sketch, "E1009", {"start": v(32.78, 15.45) * mm, "mid": v(32.45, 15.6) * mm, "end": v(32.13, 15.72) * mm});
            skCircle(sketch, "E1010", {"center": v(27.29, 3.12) * mm, "radius": 3.1 * mm});
            skLineSegment(sketch, "E1011", {"start": v(-87.58, -66.08) * mm, "end": v(-88.37, -66.56) * mm});
            skArc(sketch, "E1012", {"start": v(-71.35, 61.84) * mm, "mid": v(-71.16, 62.54) * mm, "end": v(-71.35, 63.24) * mm});
            skLineSegment(sketch, "E1013", {"start": v(-88.37, -66.56) * mm, "end": v(-89.2, -67.18) * mm});
            skArc(sketch, "E1014", {"start": v(-73.77, 61.84) * mm, "mid": v(-73.26, 61.33) * mm, "end": v(-72.56, 61.14) * mm});
            skArc(sketch, "E1015", {"start": v(-89.2, -67.18) * mm, "mid": v(-89.08, -67.86) * mm, "end": v(-88.95, -68.52) * mm});
            skArc(sketch, "E1016", {"start": v(-71.17, 63.34) * mm, "mid": v(-71.76, 63.93) * mm, "end": v(-72.56, 64.14) * mm});
            skLineSegment(sketch, "E1017", {"start": v(-85.05, -68.83) * mm, "end": v(-85.6, -68.99) * mm});
            skArc(sketch, "E1018", {"start": v(-73.94, 63.34) * mm, "mid": v(-74.16, 62.54) * mm, "end": v(-73.94, 61.74) * mm});
            skLineSegment(sketch, "E1019", {"start": v(-85.6, -68.99) * mm, "end": v(-85.78, -69.03) * mm});
            skLineSegment(sketch, "E1020", {"start": v(-85.78, -69.03) * mm, "end": v(-85.98, -69.05) * mm});
            skLineSegment(sketch, "E1021", {"start": v(-85.98, -69.05) * mm, "end": v(-86.21, -69.06) * mm});
            skLineSegment(sketch, "E1022", {"start": v(-86.21, -69.06) * mm, "end": v(-86.47, -69.06) * mm});
            skLineSegment(sketch, "E1023", {"start": v(-86.47, -69.06) * mm, "end": v(-86.76, -69.04) * mm});
            skLineSegment(sketch, "E1024", {"start": v(-86.76, -69.04) * mm, "end": v(-87.06, -69.01) * mm});
            skLineSegment(sketch, "E1025", {"start": v(-87.06, -69.01) * mm, "end": v(-87.97, -68.83) * mm});
            skLineSegment(sketch, "E1026", {"start": v(-87.97, -68.83) * mm, "end": v(-88.95, -68.52) * mm});
            skArc(sketch, "E1027", {"start": v(-84.07, -69.35) * mm, "mid": v(-84.46, -68.9) * mm, "end": v(-85.05, -68.83) * mm});
            skArc(sketch, "E1028", {"start": v(-84.07, -69.35) * mm, "mid": v(-83.95, -69.68) * mm, "end": v(-83.83, -70.02) * mm});
            skArc(sketch, "E1029", {"start": v(-84.25, -71.04) * mm, "mid": v(-83.83, -70.61) * mm, "end": v(-83.83, -70.02) * mm});
            skArc(sketch, "E1030", {"start": v(-66.09, -58.67) * mm, "mid": v(-67.68, -58) * mm, "end": v(-69.39, -57.78) * mm});
            skLineSegment(sketch, "E1031", {"start": v(-84.25, -71.04) * mm, "end": v(-84.77, -71.28) * mm});
            skArc(sketch, "E1032", {"start": v(-69.39, -57.98) * mm, "mid": v(-71.04, -58.2) * mm, "end": v(-72.59, -58.84) * mm});
            skLineSegment(sketch, "E1033", {"start": v(-84.77, -71.28) * mm, "end": v(-84.93, -71.36) * mm});
            skLineSegment(sketch, "E1034", {"start": v(-69.39, -57.98) * mm, "end": v(-69.39, -57.78) * mm});
            skLineSegment(sketch, "E1035", {"start": v(-84.93, -71.36) * mm, "end": v(-85.1, -71.47) * mm});
            skLineSegment(sketch, "E1036", {"start": v(-72.59, -58.84) * mm, "end": v(-72.69, -58.67) * mm});
            skLineSegment(sketch, "E1037", {"start": v(-85.1, -71.47) * mm, "end": v(-85.28, -71.61) * mm});
            skLineSegment(sketch, "E1038", {"start": v(-74.93, -61.18) * mm, "end": v(-75.1, -61.08) * mm});
            skLineSegment(sketch, "E1039", {"start": v(-85.28, -71.61) * mm, "end": v(-85.48, -71.78) * mm});
            skLineSegment(sketch, "E1040", {"start": v(-75.79, -64.38) * mm, "end": v(-75.99, -64.38) * mm});
            skLineSegment(sketch, "E1041", {"start": v(-85.48, -71.78) * mm, "end": v(-85.7, -71.98) * mm});
            skLineSegment(sketch, "E1042", {"start": v(-74.93, -67.58) * mm, "end": v(-75.1, -67.68) * mm});
            skLineSegment(sketch, "E1043", {"start": v(-85.7, -71.98) * mm, "end": v(-85.9, -72.2) * mm});
            skLineSegment(sketch, "E1044", {"start": v(-72.59, -69.93) * mm, "end": v(-72.69, -70.1) * mm});
            skLineSegment(sketch, "E1045", {"start": v(-85.9, -72.2) * mm, "end": v(-86.48, -72.92) * mm});
            skLineSegment(sketch, "E1046", {"start": v(-69.39, -70.78) * mm, "end": v(-69.39, -70.98) * mm});
            skLineSegment(sketch, "E1047", {"start": v(-86.48, -72.92) * mm, "end": v(-87.04, -73.79) * mm});
            skLineSegment(sketch, "E1048", {"start": v(-66.19, -69.93) * mm, "end": v(-66.09, -70.1) * mm});
            skArc(sketch, "E1049", {"start": v(-87.04, -73.79) * mm, "mid": v(-86.7, -74.38) * mm, "end": v(-86.36, -74.97) * mm});
            skLineSegment(sketch, "E1050", {"start": v(-63.85, -67.58) * mm, "end": v(-63.67, -67.68) * mm});
            skLineSegment(sketch, "E1051", {"start": v(-82.59, -73.92) * mm, "end": v(-83.05, -74.26) * mm});
            skLineSegment(sketch, "E1052", {"start": v(-62.99, -64.38) * mm, "end": v(-62.79, -64.38) * mm});
            skLineSegment(sketch, "E1053", {"start": v(-83.05, -74.26) * mm, "end": v(-83.2, -74.35) * mm});
            skLineSegment(sketch, "E1054", {"start": v(-63.85, -61.18) * mm, "end": v(-63.67, -61.08) * mm});
            skLineSegment(sketch, "E1055", {"start": v(-83.2, -74.35) * mm, "end": v(-83.38, -74.44) * mm});
            skLineSegment(sketch, "E1056", {"start": v(-66.19, -58.84) * mm, "end": v(-66.09, -58.67) * mm});
            skLineSegment(sketch, "E1057", {"start": v(-83.38, -74.44) * mm, "end": v(-83.6, -74.53) * mm});
            skArc(sketch, "E1058", {"start": v(-63.85, -61.18) * mm, "mid": v(-64.86, -59.86) * mm, "end": v(-66.19, -58.84) * mm});
            skLineSegment(sketch, "E1059", {"start": v(-83.6, -74.53) * mm, "end": v(-83.84, -74.62) * mm});
            skArc(sketch, "E1060", {"start": v(-62.79, -64.38) * mm, "mid": v(-63.01, -62.68) * mm, "end": v(-63.67, -61.08) * mm});
            skLineSegment(sketch, "E1061", {"start": v(-83.84, -74.62) * mm, "end": v(-84.12, -74.7) * mm});
            skArc(sketch, "E1062", {"start": v(-63.85, -67.58) * mm, "mid": v(-63.2, -66.04) * mm, "end": v(-62.99, -64.38) * mm});
            skLineSegment(sketch, "E1063", {"start": v(-84.12, -74.7) * mm, "end": v(-84.41, -74.78) * mm});
            skArc(sketch, "E1064", {"start": v(-66.09, -70.1) * mm, "mid": v(-64.72, -69.05) * mm, "end": v(-63.67, -67.68) * mm});
            skLineSegment(sketch, "E1065", {"start": v(-84.41, -74.78) * mm, "end": v(-85.33, -74.92) * mm});
            skArc(sketch, "E1066", {"start": v(-69.39, -70.78) * mm, "mid": v(-67.73, -70.57) * mm, "end": v(-66.19, -69.93) * mm});
            skLineSegment(sketch, "E1067", {"start": v(-85.33, -74.92) * mm, "end": v(-86.36, -74.97) * mm});
            skArc(sketch, "E1068", {"start": v(-72.69, -70.1) * mm, "mid": v(-71.1, -70.76) * mm, "end": v(-69.39, -70.98) * mm});
            skArc(sketch, "E1069", {"start": v(-81.49, -74.07) * mm, "mid": v(-82, -73.78) * mm, "end": v(-82.59, -73.92) * mm});
            skArc(sketch, "E1070", {"start": v(-75.99, -64.38) * mm, "mid": v(-75.76, -66.1) * mm, "end": v(-75.1, -67.68) * mm});
            skArc(sketch, "E1071", {"start": v(-81.49, -74.07) * mm, "mid": v(-81.26, -74.35) * mm, "end": v(-81.03, -74.62) * mm});
            skArc(sketch, "E1072", {"start": v(-72.69, -58.67) * mm, "mid": v(-74.05, -59.72) * mm, "end": v(-75.1, -61.08) * mm});
            skArc(sketch, "E1073", {"start": v(-81.08, -75.72) * mm, "mid": v(-80.83, -75.18) * mm, "end": v(-81.03, -74.62) * mm});
            skArc(sketch, "E1074", {"start": v(-74.93, -61.18) * mm, "mid": v(-75.57, -62.73) * mm, "end": v(-75.79, -64.38) * mm});
            skLineSegment(sketch, "E1075", {"start": v(-81.08, -75.72) * mm, "end": v(-81.48, -76.12) * mm});
            skArc(sketch, "E1076", {"start": v(-74.93, -67.58) * mm, "mid": v(-73.91, -68.9) * mm, "end": v(-72.59, -69.93) * mm});
            skLineSegment(sketch, "E1077", {"start": v(-81.48, -76.12) * mm, "end": v(-81.6, -76.26) * mm});
            skLineSegment(sketch, "E1078", {"start": v(-74.22, -46.76) * mm, "end": v(-74.83, -46.06) * mm});
            skLineSegment(sketch, "E1079", {"start": v(-81.6, -76.26) * mm, "end": v(-81.73, -76.42) * mm});
            skLineSegment(sketch, "E1080", {"start": v(-81.73, -76.42) * mm, "end": v(-81.85, -76.61) * mm});
            skLineSegment(sketch, "E1081", {"start": v(-81.85, -76.61) * mm, "end": v(-81.98, -76.84) * mm});
            skLineSegment(sketch, "E1082", {"start": v(-81.98, -76.84) * mm, "end": v(-82.1, -77.1) * mm});
            skLineSegment(sketch, "E1083", {"start": v(-82.1, -77.1) * mm, "end": v(-82.23, -77.38) * mm});
            skLineSegment(sketch, "E1084", {"start": v(-82.23, -77.38) * mm, "end": v(-82.53, -78.25) * mm});
            skLineSegment(sketch, "E1085", {"start": v(-82.53, -78.25) * mm, "end": v(-82.76, -79.26) * mm});
            skLineSegment(sketch, "E1086", {"start": v(31.88, -11.26) * mm, "end": v(31.9, -11.4) * mm});
            skLineSegment(sketch, "E1087", {"start": v(42.11, 4.36) * mm, "end": v(42.34, 4.38) * mm});
            skLineSegment(sketch, "E1088", {"start": v(31.9, -11.4) * mm, "end": v(31.93, -11.6) * mm});
            skLineSegment(sketch, "E1089", {"start": v(42.34, 4.38) * mm, "end": v(42.48, 4.41) * mm});
            skLineSegment(sketch, "E1090", {"start": v(-61.3, 69.4) * mm, "end": v(-61.55, 69.23) * mm});
            skLineSegment(sketch, "E1091", {"start": v(-59.93, 67.13) * mm, "end": v(-59.76, 67.15) * mm});
            skLineSegment(sketch, "E1092", {"start": v(-86.1, 61.14) * mm, "end": v(-86.83, 60.78) * mm});
            skLineSegment(sketch, "E1093", {"start": v(-51.74, -54.98) * mm, "end": v(-52.3, -55.85) * mm});
            skLineSegment(sketch, "E1094", {"start": v(-64.56, -46.76) * mm, "end": v(-64.74, -47) * mm});
            skLineSegment(sketch, "E1095", {"start": v(-85.26, 16.62) * mm, "end": v(-85.34, 16.74) * mm});
            skLineSegment(sketch, "E1096", {"start": v(-85.12, 16.44) * mm, "end": v(-85.26, 16.62) * mm});
            skLineSegment(sketch, "E1097", {"start": v(-84.75, 16) * mm, "end": v(-85.12, 16.44) * mm});
            skArc(sketch, "E1098", {"start": v(-84.95, 20.4) * mm, "mid": v(-85.51, 20.05) * mm, "end": v(-86.06, 19.67) * mm});
            skLineSegment(sketch, "E1099", {"start": v(-84.06, 19.94) * mm, "end": v(-84.95, 20.4) * mm});
            skLineSegment(sketch, "E1100", {"start": v(-83.32, 19.42) * mm, "end": v(-84.06, 19.94) * mm});
            skLineSegment(sketch, "E1101", {"start": v(-83.12, 19.25) * mm, "end": v(-83.32, 19.42) * mm});
            skLineSegment(sketch, "E1102", {"start": v(-82.94, 19.09) * mm, "end": v(-83.12, 19.25) * mm});
            skLineSegment(sketch, "E1103", {"start": v(-82.78, 18.92) * mm, "end": v(-82.94, 19.09) * mm});
            skLineSegment(sketch, "E1104", {"start": v(-82.64, 18.77) * mm, "end": v(-82.78, 18.92) * mm});
            skLineSegment(sketch, "E1105", {"start": v(-82.52, 18.63) * mm, "end": v(-82.64, 18.77) * mm});
            skLineSegment(sketch, "E1106", {"start": v(-82.44, 18.5) * mm, "end": v(-82.52, 18.63) * mm});
            skLineSegment(sketch, "E1107", {"start": v(-82.33, 18.3) * mm, "end": v(-82.44, 18.5) * mm});
            skLineSegment(sketch, "E1108", {"start": v(-82.06, 17.79) * mm, "end": v(-82.33, 18.3) * mm});
            skArc(sketch, "E1109", {"start": v(-82.06, 17.79) * mm, "mid": v(-81.6, 17.4) * mm, "end": v(-81, 17.42) * mm});
            skArc(sketch, "E1110", {"start": v(-80.35, 17.69) * mm, "mid": v(-80.68, 17.56) * mm, "end": v(-81, 17.42) * mm});
            skArc(sketch, "E1111", {"start": v(-80.35, 17.69) * mm, "mid": v(-79.9, 18.1) * mm, "end": v(-79.87, 18.7) * mm});
            skLineSegment(sketch, "E1112", {"start": v(-79.97, 21.63) * mm, "end": v(-79.67, 22.6) * mm});
            skLineSegment(sketch, "E1113", {"start": v(-80.13, 20.74) * mm, "end": v(-79.97, 21.63) * mm});
            skLineSegment(sketch, "E1114", {"start": v(-80.15, 20.48) * mm, "end": v(-80.13, 20.74) * mm});
            skLineSegment(sketch, "E1115", {"start": v(-80.16, 20.24) * mm, "end": v(-80.15, 20.48) * mm});
            skLineSegment(sketch, "E1116", {"start": v(-80.16, 20) * mm, "end": v(-80.16, 20.24) * mm});
            skLineSegment(sketch, "E1117", {"start": v(-80.15, 19.8) * mm, "end": v(-80.16, 20) * mm});
            skLineSegment(sketch, "E1118", {"start": v(-80.13, 19.62) * mm, "end": v(-80.15, 19.8) * mm});
            skLineSegment(sketch, "E1119", {"start": v(-80.1, 19.47) * mm, "end": v(-80.13, 19.62) * mm});
            skLineSegment(sketch, "E1120", {"start": v(-80.04, 19.25) * mm, "end": v(-80.1, 19.47) * mm});
            skLineSegment(sketch, "E1121", {"start": v(-79.87, 18.7) * mm, "end": v(-80.04, 19.25) * mm});
            skArc(sketch, "E1122", {"start": v(-78.37, 22.86) * mm, "mid": v(-79.02, 22.74) * mm, "end": v(-79.67, 22.6) * mm});
            skLineSegment(sketch, "E1123", {"start": v(-77.73, 22.08) * mm, "end": v(-78.37, 22.86) * mm});
            skLineSegment(sketch, "E1124", {"start": v(-77.24, 21.32) * mm, "end": v(-77.73, 22.08) * mm});
            skLineSegment(sketch, "E1125", {"start": v(-77.12, 21.09) * mm, "end": v(-77.24, 21.32) * mm});
            skLineSegment(sketch, "E1126", {"start": v(-77.01, 20.86) * mm, "end": v(-77.12, 21.09) * mm});
            skLineSegment(sketch, "E1127", {"start": v(-76.93, 20.65) * mm, "end": v(-77.01, 20.86) * mm});
            skLineSegment(sketch, "E1128", {"start": v(-76.86, 20.45) * mm, "end": v(-76.93, 20.65) * mm});
            skLineSegment(sketch, "E1129", {"start": v(-76.8, 20.28) * mm, "end": v(-76.86, 20.45) * mm});
            skLineSegment(sketch, "E1130", {"start": v(-76.77, 20.13) * mm, "end": v(-76.8, 20.28) * mm});
            skLineSegment(sketch, "E1131", {"start": v(-76.75, 19.9) * mm, "end": v(-76.77, 20.13) * mm});
            skLineSegment(sketch, "E1132", {"start": v(-76.7, 19.33) * mm, "end": v(-76.75, 19.9) * mm});
            skArc(sketch, "E1133", {"start": v(-76.7, 19.33) * mm, "mid": v(-76.43, 18.79) * mm, "end": v(-75.87, 18.58) * mm});
            skArc(sketch, "E1134", {"start": v(-75.16, 18.58) * mm, "mid": v(-75.51, 18.58) * mm, "end": v(-75.87, 18.58) * mm});
            skArc(sketch, "E1135", {"start": v(-75.16, 18.58) * mm, "mid": v(-74.6, 18.79) * mm, "end": v(-74.33, 19.33) * mm});
            skLineSegment(sketch, "E1136", {"start": v(-73.3, 22.08) * mm, "end": v(-72.66, 22.86) * mm});
            skLineSegment(sketch, "E1137", {"start": v(-73.78, 21.32) * mm, "end": v(-73.3, 22.08) * mm});
            skLineSegment(sketch, "E1138", {"start": v(-73.9, 21.09) * mm, "end": v(-73.78, 21.32) * mm});
            skLineSegment(sketch, "E1139", {"start": v(-74.01, 20.86) * mm, "end": v(-73.9, 21.09) * mm});
            skLineSegment(sketch, "E1140", {"start": v(-74.1, 20.65) * mm, "end": v(-74.01, 20.86) * mm});
            skLineSegment(sketch, "E1141", {"start": v(-74.17, 20.45) * mm, "end": v(-74.1, 20.65) * mm});
            skLineSegment(sketch, "E1142", {"start": v(-74.22, 20.28) * mm, "end": v(-74.17, 20.45) * mm});
            skLineSegment(sketch, "E1143", {"start": v(-74.25, 20.13) * mm, "end": v(-74.22, 20.28) * mm});
            skLineSegment(sketch, "E1144", {"start": v(-74.28, 19.9) * mm, "end": v(-74.25, 20.13) * mm});
            skLineSegment(sketch, "E1145", {"start": v(-74.33, 19.33) * mm, "end": v(-74.28, 19.9) * mm});
            skArc(sketch, "E1146", {"start": v(-71.35, 22.6) * mm, "mid": v(-72, 22.74) * mm, "end": v(-72.66, 22.86) * mm});
            skLineSegment(sketch, "E1147", {"start": v(-71.06, 21.63) * mm, "end": v(-71.35, 22.6) * mm});
            skLineSegment(sketch, "E1148", {"start": v(-70.9, 20.74) * mm, "end": v(-71.06, 21.63) * mm});
            skLineSegment(sketch, "E1149", {"start": v(-70.87, 20.48) * mm, "end": v(-70.9, 20.74) * mm});
            skLineSegment(sketch, "E1150", {"start": v(-70.86, 20.24) * mm, "end": v(-70.87, 20.48) * mm});
            skLineSegment(sketch, "E1151", {"start": v(-70.86, 20) * mm, "end": v(-70.86, 20.24) * mm});
            skLineSegment(sketch, "E1152", {"start": v(-70.87, 19.8) * mm, "end": v(-70.86, 20) * mm});
            skLineSegment(sketch, "E1153", {"start": v(-70.9, 19.62) * mm, "end": v(-70.87, 19.8) * mm});
            skLineSegment(sketch, "E1154", {"start": v(-70.92, 19.47) * mm, "end": v(-70.9, 19.62) * mm});
            skLineSegment(sketch, "E1155", {"start": v(-58.96, 0.63) * mm, "end": v(-58, 0.92) * mm});
            skArc(sketch, "E1156", {"start": v(-58, 0.92) * mm, "mid": v(-57.86, 1.57) * mm, "end": v(-57.74, 2.23) * mm});
            skLineSegment(sketch, "E1157", {"start": v(-61.27, 3.9) * mm, "end": v(-60.7, 3.85) * mm});
            skLineSegment(sketch, "E1158", {"start": v(-60.7, 3.85) * mm, "end": v(-60.46, 3.82) * mm});
            skLineSegment(sketch, "E1159", {"start": v(-60.46, 3.82) * mm, "end": v(-60.32, 3.8) * mm});
            skLineSegment(sketch, "E1160", {"start": v(-60.32, 3.8) * mm, "end": v(-60.14, 3.74) * mm});
            skLineSegment(sketch, "E1161", {"start": v(-60.14, 3.74) * mm, "end": v(-59.95, 3.67) * mm});
            skLineSegment(sketch, "E1162", {"start": v(-59.95, 3.67) * mm, "end": v(-59.73, 3.58) * mm});
            skLineSegment(sketch, "E1163", {"start": v(-59.73, 3.58) * mm, "end": v(-59.51, 3.48) * mm});
            skLineSegment(sketch, "E1164", {"start": v(-59.51, 3.48) * mm, "end": v(-59.28, 3.36) * mm});
            skLineSegment(sketch, "E1165", {"start": v(-59.28, 3.36) * mm, "end": v(-58.52, 2.87) * mm});
            skLineSegment(sketch, "E1166", {"start": v(-58.52, 2.87) * mm, "end": v(-57.74, 2.23) * mm});
            skArc(sketch, "E1167", {"start": v(-62.02, 4.73) * mm, "mid": v(-61.8, 4.16) * mm, "end": v(-61.27, 3.9) * mm});
            skArc(sketch, "E1168", {"start": v(-62.02, 4.73) * mm, "mid": v(-62.01, 5.08) * mm, "end": v(-62.02, 5.44) * mm});
            skArc(sketch, "E1169", {"start": v(-61.27, 6.27) * mm, "mid": v(-61.8, 6) * mm, "end": v(-62.02, 5.44) * mm});
            skLineSegment(sketch, "E1170", {"start": v(-61.27, 6.27) * mm, "end": v(-60.7, 6.32) * mm});
            skLineSegment(sketch, "E1171", {"start": v(-60.7, 6.32) * mm, "end": v(-60.46, 6.34) * mm});
            skLineSegment(sketch, "E1172", {"start": v(-60.46, 6.34) * mm, "end": v(-60.32, 6.38) * mm});
            skLineSegment(sketch, "E1173", {"start": v(-60.32, 6.38) * mm, "end": v(-60.14, 6.43) * mm});
            skLineSegment(sketch, "E1174", {"start": v(-60.14, 6.43) * mm, "end": v(-59.95, 6.5) * mm});
            skLineSegment(sketch, "E1175", {"start": v(-59.95, 6.5) * mm, "end": v(-59.73, 6.59) * mm});
            skLineSegment(sketch, "E1176", {"start": v(-59.73, 6.59) * mm, "end": v(-59.51, 6.7) * mm});
            skLineSegment(sketch, "E1177", {"start": v(-59.51, 6.7) * mm, "end": v(-59.28, 6.81) * mm});
            skLineSegment(sketch, "E1178", {"start": v(-59.28, 6.81) * mm, "end": v(-58.52, 7.3) * mm});
            skLineSegment(sketch, "E1179", {"start": v(-58.52, 7.3) * mm, "end": v(-57.74, 7.94) * mm});
            skArc(sketch, "E1180", {"start": v(-57.74, 7.94) * mm, "mid": v(-57.86, 8.6) * mm, "end": v(-58, 9.25) * mm});
            skLineSegment(sketch, "E1181", {"start": v(-61.9, 9.44) * mm, "end": v(-61.35, 9.61) * mm});
            skLineSegment(sketch, "E1182", {"start": v(-61.35, 9.61) * mm, "end": v(-61.13, 9.68) * mm});
            skLineSegment(sketch, "E1183", {"start": v(-61.13, 9.68) * mm, "end": v(-60.98, 9.7) * mm});
            skLineSegment(sketch, "E1184", {"start": v(-60.98, 9.7) * mm, "end": v(-60.8, 9.72) * mm});
            skLineSegment(sketch, "E1185", {"start": v(-60.8, 9.72) * mm, "end": v(-60.59, 9.73) * mm});
            skLineSegment(sketch, "E1186", {"start": v(-60.59, 9.73) * mm, "end": v(-60.36, 9.73) * mm});
            skLineSegment(sketch, "E1187", {"start": v(-60.36, 9.73) * mm, "end": v(-60.11, 9.72) * mm});
            skLineSegment(sketch, "E1188", {"start": v(-60.11, 9.72) * mm, "end": v(-59.85, 9.7) * mm});
            skLineSegment(sketch, "E1189", {"start": v(-59.85, 9.7) * mm, "end": v(-58.96, 9.54) * mm});
            skLineSegment(sketch, "E1190", {"start": v(-58.96, 9.54) * mm, "end": v(-58, 9.25) * mm});
            skArc(sketch, "E1191", {"start": v(-62.9, 9.92) * mm, "mid": v(-62.5, 9.48) * mm, "end": v(-61.9, 9.44) * mm});
            skArc(sketch, "E1192", {"start": v(-62.9, 9.92) * mm, "mid": v(-63.04, 10.25) * mm, "end": v(-63.18, 10.57) * mm});
            skArc(sketch, "E1193", {"start": v(-62.8, 11.63) * mm, "mid": v(-63.2, 11.18) * mm, "end": v(-63.18, 10.57) * mm});
            skLineSegment(sketch, "E1194", {"start": v(-62.8, 11.63) * mm, "end": v(-62.3, 11.9) * mm});
            skLineSegment(sketch, "E1195", {"start": v(-62.3, 11.9) * mm, "end": v(-62.1, 12) * mm});
            skLineSegment(sketch, "E1196", {"start": v(-62.1, 12) * mm, "end": v(-61.97, 12.1) * mm});
            skLineSegment(sketch, "E1197", {"start": v(-61.97, 12.1) * mm, "end": v(-61.83, 12.2) * mm});
            skLineSegment(sketch, "E1198", {"start": v(-61.83, 12.2) * mm, "end": v(-61.67, 12.35) * mm});
            skLineSegment(sketch, "E1199", {"start": v(-61.67, 12.35) * mm, "end": v(-61.5, 12.5) * mm});
            skLineSegment(sketch, "E1200", {"start": v(-61.5, 12.5) * mm, "end": v(-61.34, 12.7) * mm});
            skLineSegment(sketch, "E1201", {"start": v(-61.34, 12.7) * mm, "end": v(-61.18, 12.9) * mm});
            skLineSegment(sketch, "E1202", {"start": v(-61.18, 12.9) * mm, "end": v(-60.66, 13.64) * mm});
            skLineSegment(sketch, "E1203", {"start": v(-60.66, 13.64) * mm, "end": v(-60.19, 14.52) * mm});
            skArc(sketch, "E1204", {"start": v(-60.19, 14.52) * mm, "mid": v(-60.55, 15.08) * mm, "end": v(-60.93, 15.63) * mm});
            skLineSegment(sketch, "E1205", {"start": v(-64.6, 14.32) * mm, "end": v(-64.16, 14.7) * mm});
            skLineSegment(sketch, "E1206", {"start": v(-64.16, 14.7) * mm, "end": v(-63.98, 14.83) * mm});
            skLineSegment(sketch, "E1207", {"start": v(-63.98, 14.83) * mm, "end": v(-63.86, 14.91) * mm});
            skLineSegment(sketch, "E1208", {"start": v(-63.86, 14.91) * mm, "end": v(-63.7, 15) * mm});
            skLineSegment(sketch, "E1209", {"start": v(-63.7, 15) * mm, "end": v(-63.5, 15.1) * mm});
            skLineSegment(sketch, "E1210", {"start": v(-63.5, 15.1) * mm, "end": v(-63.3, 15.18) * mm});
            skLineSegment(sketch, "E1211", {"start": v(-63.3, 15.18) * mm, "end": v(-63.06, 15.26) * mm});
            skLineSegment(sketch, "E1212", {"start": v(-63.06, 15.26) * mm, "end": v(-62.81, 15.34) * mm});
            skLineSegment(sketch, "E1213", {"start": v(-62.81, 15.34) * mm, "end": v(-61.93, 15.53) * mm});
            skLineSegment(sketch, "E1214", {"start": v(-61.93, 15.53) * mm, "end": v(-60.93, 15.63) * mm});
            skArc(sketch, "E1215", {"start": v(-65.72, 14.38) * mm, "mid": v(-65.17, 14.12) * mm, "end": v(-64.6, 14.32) * mm});
            skArc(sketch, "E1216", {"start": v(-65.72, 14.38) * mm, "mid": v(-65.97, 14.63) * mm, "end": v(-66.22, 14.88) * mm});
            skArc(sketch, "E1217", {"start": v(-66.28, 16) * mm, "mid": v(-66.47, 15.42) * mm, "end": v(-66.22, 14.88) * mm});
            skLineSegment(sketch, "E1218", {"start": v(-66.28, 16) * mm, "end": v(-65.9, 16.44) * mm});
            skLineSegment(sketch, "E1219", {"start": v(-65.9, 16.44) * mm, "end": v(-65.76, 16.62) * mm});
            skLineSegment(sketch, "E1220", {"start": v(-65.76, 16.62) * mm, "end": v(-65.68, 16.74) * mm});
            skLineSegment(sketch, "E1221", {"start": v(-65.68, 16.74) * mm, "end": v(-65.6, 16.9) * mm});
            skLineSegment(sketch, "E1222", {"start": v(-65.6, 16.9) * mm, "end": v(-65.5, 17.1) * mm});
            skLineSegment(sketch, "E1223", {"start": v(-65.5, 17.1) * mm, "end": v(-65.42, 17.3) * mm});
            skLineSegment(sketch, "E1224", {"start": v(-65.42, 17.3) * mm, "end": v(-65.33, 17.53) * mm});
            skLineSegment(sketch, "E1225", {"start": v(-65.33, 17.53) * mm, "end": v(-65.26, 17.78) * mm});
            skLineSegment(sketch, "E1226", {"start": v(-65.26, 17.78) * mm, "end": v(-65.06, 18.67) * mm});
            skLineSegment(sketch, "E1227", {"start": v(-65.06, 18.67) * mm, "end": v(-64.97, 19.67) * mm});
            skArc(sketch, "E1228", {"start": v(-64.97, 19.67) * mm, "mid": v(-65.51, 20.05) * mm, "end": v(-66.07, 20.4) * mm});
            skLineSegment(sketch, "E1229", {"start": v(-68.97, 17.79) * mm, "end": v(-68.7, 18.3) * mm});
            skLineSegment(sketch, "E1230", {"start": v(-68.7, 18.3) * mm, "end": v(-68.59, 18.5) * mm});
            skLineSegment(sketch, "E1231", {"start": v(-68.59, 18.5) * mm, "end": v(-68.5, 18.63) * mm});
            skLineSegment(sketch, "E1232", {"start": v(-68.5, 18.63) * mm, "end": v(-68.39, 18.77) * mm});
            skLineSegment(sketch, "E1233", {"start": v(-68.39, 18.77) * mm, "end": v(-68.25, 18.92) * mm});
            skLineSegment(sketch, "E1234", {"start": v(-68.25, 18.92) * mm, "end": v(-68.09, 19.09) * mm});
            skLineSegment(sketch, "E1235", {"start": v(-68.09, 19.09) * mm, "end": v(-67.9, 19.25) * mm});
            skLineSegment(sketch, "E1236", {"start": v(-67.9, 19.25) * mm, "end": v(-67.7, 19.42) * mm});
            skLineSegment(sketch, "E1237", {"start": v(-67.7, 19.42) * mm, "end": v(-66.96, 19.94) * mm});
            skLineSegment(sketch, "E1238", {"start": v(-66.96, 19.94) * mm, "end": v(-66.07, 20.4) * mm});
            skArc(sketch, "E1239", {"start": v(-70.02, 17.42) * mm, "mid": v(-69.42, 17.4) * mm, "end": v(-68.97, 17.79) * mm});
            skArc(sketch, "E1240", {"start": v(-70.02, 17.42) * mm, "mid": v(-70.35, 17.56) * mm, "end": v(-70.67, 17.69) * mm});
            skArc(sketch, "E1241", {"start": v(-71.16, 18.7) * mm, "mid": v(-71.12, 18.1) * mm, "end": v(-70.67, 17.69) * mm});
            skLineSegment(sketch, "E1242", {"start": v(-71.16, 18.7) * mm, "end": v(-70.98, 19.25) * mm});
            skLineSegment(sketch, "E1243", {"start": v(-70.98, 19.25) * mm, "end": v(-70.92, 19.47) * mm});
            skLineSegment(sketch, "E1244", {"start": v(-85.6, 17.3) * mm, "end": v(-85.7, 17.53) * mm});
            skLineSegment(sketch, "E1245", {"start": v(-85.7, 17.53) * mm, "end": v(-85.77, 17.78) * mm});
            skLineSegment(sketch, "E1246", {"start": v(-85.77, 17.78) * mm, "end": v(-85.96, 18.67) * mm});
            skLineSegment(sketch, "E1247", {"start": v(-85.96, 18.67) * mm, "end": v(-86.06, 19.67) * mm});
            skArc(sketch, "E1248", {"start": v(-84.8, 14.88) * mm, "mid": v(-84.55, 15.42) * mm, "end": v(-84.75, 16) * mm});
            skArc(sketch, "E1249", {"start": v(-84.8, 14.88) * mm, "mid": v(-85.06, 14.63) * mm, "end": v(-85.3, 14.38) * mm});
            skArc(sketch, "E1250", {"start": v(-86.42, 14.32) * mm, "mid": v(-85.85, 14.12) * mm, "end": v(-85.3, 14.38) * mm});
            skLineSegment(sketch, "E1251", {"start": v(-86.42, 14.32) * mm, "end": v(-86.87, 14.7) * mm});
            skLineSegment(sketch, "E1252", {"start": v(-86.87, 14.7) * mm, "end": v(-87.04, 14.83) * mm});
            skLineSegment(sketch, "E1253", {"start": v(-87.04, 14.83) * mm, "end": v(-87.17, 14.91) * mm});
            skLineSegment(sketch, "E1254", {"start": v(-87.17, 14.91) * mm, "end": v(-87.33, 15) * mm});
            skLineSegment(sketch, "E1255", {"start": v(-87.33, 15) * mm, "end": v(-87.52, 15.1) * mm});
            skLineSegment(sketch, "E1256", {"start": v(-87.52, 15.1) * mm, "end": v(-87.73, 15.18) * mm});
            skLineSegment(sketch, "E1257", {"start": v(-87.73, 15.18) * mm, "end": v(-87.96, 15.26) * mm});
            skLineSegment(sketch, "E1258", {"start": v(-87.96, 15.26) * mm, "end": v(-88.21, 15.34) * mm});
            skLineSegment(sketch, "E1259", {"start": v(-88.21, 15.34) * mm, "end": v(-89.1, 15.53) * mm});
            skLineSegment(sketch, "E1260", {"start": v(-89.1, 15.53) * mm, "end": v(-90.1, 15.63) * mm});
            skArc(sketch, "E1261", {"start": v(-90.1, 15.63) * mm, "mid": v(-90.48, 15.08) * mm, "end": v(-90.84, 14.52) * mm});
            skLineSegment(sketch, "E1262", {"start": v(-88.22, 11.63) * mm, "end": v(-88.73, 11.9) * mm});
            skLineSegment(sketch, "E1263", {"start": v(-88.73, 11.9) * mm, "end": v(-88.93, 12) * mm});
            skLineSegment(sketch, "E1264", {"start": v(-88.93, 12) * mm, "end": v(-89.05, 12.1) * mm});
            skLineSegment(sketch, "E1265", {"start": v(-89.05, 12.1) * mm, "end": v(-89.2, 12.2) * mm});
            skLineSegment(sketch, "E1266", {"start": v(-89.2, 12.2) * mm, "end": v(-89.35, 12.35) * mm});
            skLineSegment(sketch, "E1267", {"start": v(-89.35, 12.35) * mm, "end": v(-89.52, 12.5) * mm});
            skLineSegment(sketch, "E1268", {"start": v(-89.52, 12.5) * mm, "end": v(-89.68, 12.7) * mm});
            skLineSegment(sketch, "E1269", {"start": v(-89.68, 12.7) * mm, "end": v(-89.85, 12.9) * mm});
            skLineSegment(sketch, "E1270", {"start": v(-89.85, 12.9) * mm, "end": v(-90.36, 13.64) * mm});
            skLineSegment(sketch, "E1271", {"start": v(-90.36, 13.64) * mm, "end": v(-90.84, 14.52) * mm});
            skArc(sketch, "E1272", {"start": v(-87.85, 10.57) * mm, "mid": v(-87.82, 11.18) * mm, "end": v(-88.22, 11.63) * mm});
            skArc(sketch, "E1273", {"start": v(-87.85, 10.57) * mm, "mid": v(-87.98, 10.25) * mm, "end": v(-88.12, 9.92) * mm});
            skArc(sketch, "E1274", {"start": v(-89.13, 9.44) * mm, "mid": v(-88.52, 9.48) * mm, "end": v(-88.12, 9.92) * mm});
            skLineSegment(sketch, "E1275", {"start": v(-89.13, 9.44) * mm, "end": v(-89.68, 9.61) * mm});
            skLineSegment(sketch, "E1276", {"start": v(-89.68, 9.61) * mm, "end": v(-89.9, 9.68) * mm});
            skLineSegment(sketch, "E1277", {"start": v(-89.9, 9.68) * mm, "end": v(-90.04, 9.7) * mm});
            skLineSegment(sketch, "E1278", {"start": v(-90.04, 9.7) * mm, "end": v(-90.23, 9.72) * mm});
            skLineSegment(sketch, "E1279", {"start": v(-90.23, 9.72) * mm, "end": v(-90.44, 9.73) * mm});
            skLineSegment(sketch, "E1280", {"start": v(-90.44, 9.73) * mm, "end": v(-90.66, 9.73) * mm});
            skLineSegment(sketch, "E1281", {"start": v(-90.66, 9.73) * mm, "end": v(-90.91, 9.72) * mm});
            skLineSegment(sketch, "E1282", {"start": v(-90.91, 9.72) * mm, "end": v(-91.17, 9.7) * mm});
            skArc(sketch, "E1283", {"start": v(-90.84, -4.36) * mm, "mid": v(-90.48, -4.92) * mm, "end": v(-90.1, -5.46) * mm});
            skLineSegment(sketch, "E1284", {"start": v(-74.28, -9.74) * mm, "end": v(-74.25, -9.97) * mm});
            skLineSegment(sketch, "E1285", {"start": v(-86.42, -4.15) * mm, "end": v(-86.87, -4.52) * mm});
            skLineSegment(sketch, "E1286", {"start": v(-74.25, -9.97) * mm, "end": v(-74.22, -10.1) * mm});
            skLineSegment(sketch, "E1287", {"start": v(-86.87, -4.52) * mm, "end": v(-87.04, -4.67) * mm});
            skLineSegment(sketch, "E1288", {"start": v(-74.22, -10.1) * mm, "end": v(-74.17, -10.29) * mm});
            skLineSegment(sketch, "E1289", {"start": v(-87.04, -4.67) * mm, "end": v(-87.17, -4.75) * mm});
            skLineSegment(sketch, "E1290", {"start": v(-74.17, -10.29) * mm, "end": v(-74.1, -10.48) * mm});
            skLineSegment(sketch, "E1291", {"start": v(-87.17, -4.75) * mm, "end": v(-87.33, -4.83) * mm});
            skLineSegment(sketch, "E1292", {"start": v(-74.1, -10.48) * mm, "end": v(-74.01, -10.7) * mm});
            skLineSegment(sketch, "E1293", {"start": v(-87.33, -4.83) * mm, "end": v(-87.52, -4.92) * mm});
            skLineSegment(sketch, "E1294", {"start": v(-74.01, -10.7) * mm, "end": v(-73.9, -10.92) * mm});
            skLineSegment(sketch, "E1295", {"start": v(-87.52, -4.92) * mm, "end": v(-87.73, -5.01) * mm});
            skLineSegment(sketch, "E1296", {"start": v(-73.9, -10.92) * mm, "end": v(-73.78, -11.15) * mm});
            skLineSegment(sketch, "E1297", {"start": v(-87.73, -5.01) * mm, "end": v(-87.96, -5.1) * mm});
            skLineSegment(sketch, "E1298", {"start": v(-73.78, -11.15) * mm, "end": v(-73.3, -11.9) * mm});
            skLineSegment(sketch, "E1299", {"start": v(-87.96, -5.1) * mm, "end": v(-88.21, -5.17) * mm});
            skLineSegment(sketch, "E1300", {"start": v(-73.3, -11.9) * mm, "end": v(-72.66, -12.69) * mm});
            skLineSegment(sketch, "E1301", {"start": v(-88.21, -5.17) * mm, "end": v(-89.1, -5.36) * mm});
            skArc(sketch, "E1302", {"start": v(-72.66, -12.69) * mm, "mid": v(-72, -12.57) * mm, "end": v(-71.35, -12.43) * mm});
            skLineSegment(sketch, "E1303", {"start": v(-89.1, -5.36) * mm, "end": v(-90.1, -5.46) * mm});
            skLineSegment(sketch, "E1304", {"start": v(-71.16, -8.53) * mm, "end": v(-70.98, -9.08) * mm});
            skArc(sketch, "E1305", {"start": v(-85.3, -4.2) * mm, "mid": v(-85.85, -3.96) * mm, "end": v(-86.42, -4.15) * mm});
            skLineSegment(sketch, "E1306", {"start": v(-70.98, -9.08) * mm, "end": v(-70.92, -9.3) * mm});
            skArc(sketch, "E1307", {"start": v(-85.3, -4.2) * mm, "mid": v(-85.06, -4.46) * mm, "end": v(-84.8, -4.7) * mm});
            skLineSegment(sketch, "E1308", {"start": v(-70.92, -9.3) * mm, "end": v(-70.9, -9.45) * mm});
            skLineSegment(sketch, "E1309", {"start": v(-70.9, -9.45) * mm, "end": v(-70.87, -9.63) * mm});
            skLineSegment(sketch, "E1310", {"start": v(-70.87, -9.63) * mm, "end": v(-70.86, -9.84) * mm});
            skLineSegment(sketch, "E1311", {"start": v(-70.86, -9.84) * mm, "end": v(-70.86, -10.07) * mm});
            skLineSegment(sketch, "E1312", {"start": v(-70.86, -10.07) * mm, "end": v(-70.87, -10.31) * mm});
            skLineSegment(sketch, "E1313", {"start": v(-70.87, -10.31) * mm, "end": v(-70.9, -10.58) * mm});
            skLineSegment(sketch, "E1314", {"start": v(-70.9, -10.58) * mm, "end": v(-71.06, -11.46) * mm});
            skLineSegment(sketch, "E1315", {"start": v(-71.06, -11.46) * mm, "end": v(-71.35, -12.43) * mm});
            skArc(sketch, "E1316", {"start": v(-70.67, -7.52) * mm, "mid": v(-71.12, -7.93) * mm, "end": v(-71.16, -8.53) * mm});
            skArc(sketch, "E1317", {"start": v(-70.67, -7.52) * mm, "mid": v(-70.35, -7.39) * mm, "end": v(-70.02, -7.25) * mm});
            skArc(sketch, "E1318", {"start": v(-68.97, -7.62) * mm, "mid": v(-69.42, -7.23) * mm, "end": v(-70.02, -7.25) * mm});
            skArc(sketch, "E1319", {"start": v(-78.02, 3.63) * mm, "mid": v(-77.56, 3.03) * mm, "end": v(-76.96, 2.57) * mm});
            skLineSegment(sketch, "E1320", {"start": v(-68.97, -7.62) * mm, "end": v(-68.7, -8.14) * mm});
            skArc(sketch, "E1321", {"start": v(-66.07, -10.24) * mm, "mid": v(-65.51, -9.88) * mm, "end": v(-64.97, -9.5) * mm});
            skLineSegment(sketch, "E1322", {"start": v(-66.96, -9.77) * mm, "end": v(-66.07, -10.24) * mm});
            skLineSegment(sketch, "E1323", {"start": v(-67.7, -9.25) * mm, "end": v(-66.96, -9.77) * mm});
            skLineSegment(sketch, "E1324", {"start": v(-67.9, -9.08) * mm, "end": v(-67.7, -9.25) * mm});
            skLineSegment(sketch, "E1325", {"start": v(-68.09, -8.92) * mm, "end": v(-67.9, -9.08) * mm});
            skLineSegment(sketch, "E1326", {"start": v(-68.25, -8.76) * mm, "end": v(-68.09, -8.92) * mm});
            skLineSegment(sketch, "E1327", {"start": v(-68.39, -8.6) * mm, "end": v(-68.25, -8.76) * mm});
            skLineSegment(sketch, "E1328", {"start": v(-68.5, -8.46) * mm, "end": v(-68.39, -8.6) * mm});
            skLineSegment(sketch, "E1329", {"start": v(-68.59, -8.34) * mm, "end": v(-68.5, -8.46) * mm});
            skLineSegment(sketch, "E1330", {"start": v(-68.7, -8.14) * mm, "end": v(-68.59, -8.34) * mm});
            skLineSegment(sketch, "E1331", {"start": v(-90.36, -3.47) * mm, "end": v(-90.84, -4.36) * mm});
            skLineSegment(sketch, "E1332", {"start": v(-74.33, -9.16) * mm, "end": v(-74.28, -9.74) * mm});
            skLineSegment(sketch, "E1333", {"start": v(-89.85, -2.73) * mm, "end": v(-90.36, -3.47) * mm});
            skArc(sketch, "E1334", {"start": v(-74.33, -9.16) * mm, "mid": v(-74.6, -8.62) * mm, "end": v(-75.16, -8.41) * mm});
            skLineSegment(sketch, "E1335", {"start": v(-89.68, -2.52) * mm, "end": v(-89.85, -2.73) * mm});
            skArc(sketch, "E1336", {"start": v(-75.87, -8.41) * mm, "mid": v(-75.51, -8.42) * mm, "end": v(-75.16, -8.41) * mm});
            skLineSegment(sketch, "E1337", {"start": v(-89.52, -2.34) * mm, "end": v(-89.68, -2.52) * mm});
            skArc(sketch, "E1338", {"start": v(-75.87, -8.41) * mm, "mid": v(-76.43, -8.62) * mm, "end": v(-76.7, -9.16) * mm});
            skLineSegment(sketch, "E1339", {"start": v(-89.35, -2.18) * mm, "end": v(-89.52, -2.34) * mm});
            skLineSegment(sketch, "E1340", {"start": v(-89.2, -2.04) * mm, "end": v(-89.35, -2.18) * mm});
            skLineSegment(sketch, "E1341", {"start": v(-89.05, -1.92) * mm, "end": v(-89.2, -2.04) * mm});
            skLineSegment(sketch, "E1342", {"start": v(-88.93, -1.84) * mm, "end": v(-89.05, -1.92) * mm});
            skLineSegment(sketch, "E1343", {"start": v(-88.73, -1.73) * mm, "end": v(-88.93, -1.84) * mm});
            skLineSegment(sketch, "E1344", {"start": v(-88.22, -1.46) * mm, "end": v(-88.73, -1.73) * mm});
            skArc(sketch, "E1345", {"start": v(-88.22, -1.46) * mm, "mid": v(-87.82, -1) * mm, "end": v(-87.85, -0.4) * mm});
            skArc(sketch, "E1346", {"start": v(-88.12, 0.25) * mm, "mid": v(-87.98, -0.08) * mm, "end": v(-87.85, -0.4) * mm});
            skArc(sketch, "E1347", {"start": v(-88.12, 0.25) * mm, "mid": v(-88.52, 0.69) * mm, "end": v(-89.13, 0.73) * mm});
            skLineSegment(sketch, "E1348", {"start": v(-92.06, 0.63) * mm, "end": v(-93.02, 0.92) * mm});
            skLineSegment(sketch, "E1349", {"start": v(-91.17, 0.47) * mm, "end": v(-92.06, 0.63) * mm});
            skLineSegment(sketch, "E1350", {"start": v(-90.91, 0.44) * mm, "end": v(-91.17, 0.47) * mm});
            skLineSegment(sketch, "E1351", {"start": v(-90.66, 0.43) * mm, "end": v(-90.91, 0.44) * mm});
            skLineSegment(sketch, "E1352", {"start": v(-90.44, 0.43) * mm, "end": v(-90.66, 0.43) * mm});
            skLineSegment(sketch, "E1353", {"start": v(-90.23, 0.44) * mm, "end": v(-90.44, 0.43) * mm});
            skLineSegment(sketch, "E1354", {"start": v(-90.04, 0.46) * mm, "end": v(-90.23, 0.44) * mm});
            skLineSegment(sketch, "E1355", {"start": v(-89.9, 0.49) * mm, "end": v(-90.04, 0.46) * mm});
            skLineSegment(sketch, "E1356", {"start": v(-89.68, 0.55) * mm, "end": v(-89.9, 0.49) * mm});
            skLineSegment(sketch, "E1357", {"start": v(-89.13, 0.73) * mm, "end": v(-89.68, 0.55) * mm});
            skArc(sketch, "E1358", {"start": v(-93.28, 2.23) * mm, "mid": v(-93.17, 1.57) * mm, "end": v(-93.02, 0.92) * mm});
            skLineSegment(sketch, "E1359", {"start": v(-92.5, 2.87) * mm, "end": v(-93.28, 2.23) * mm});
            skLineSegment(sketch, "E1360", {"start": v(-91.75, 3.36) * mm, "end": v(-92.5, 2.87) * mm});
            skLineSegment(sketch, "E1361", {"start": v(-77.73, -11.9) * mm, "end": v(-78.37, -12.69) * mm});
            skLineSegment(sketch, "E1362", {"start": v(-59.85, 0.47) * mm, "end": v(-58.96, 0.63) * mm});
            skLineSegment(sketch, "E1363", {"start": v(-77.24, -11.15) * mm, "end": v(-77.73, -11.9) * mm});
            skLineSegment(sketch, "E1364", {"start": v(-60.11, 0.44) * mm, "end": v(-59.85, 0.47) * mm});
            skLineSegment(sketch, "E1365", {"start": v(-77.12, -10.92) * mm, "end": v(-77.24, -11.15) * mm});
            skLineSegment(sketch, "E1366", {"start": v(-60.36, 0.43) * mm, "end": v(-60.11, 0.44) * mm});
            skLineSegment(sketch, "E1367", {"start": v(-77.01, -10.7) * mm, "end": v(-77.12, -10.92) * mm});
            skLineSegment(sketch, "E1368", {"start": v(-60.59, 0.43) * mm, "end": v(-60.36, 0.43) * mm});
            skLineSegment(sketch, "E1369", {"start": v(-63.06, -5.1) * mm, "end": v(-62.81, -5.17) * mm});
            skLineSegment(sketch, "E1370", {"start": v(-83.32, -9.25) * mm, "end": v(-84.06, -9.77) * mm});
            skLineSegment(sketch, "E1371", {"start": v(-90.88, 3.74) * mm, "end": v(-91.08, 3.67) * mm});
            skLineSegment(sketch, "E1372", {"start": v(-76.93, -10.48) * mm, "end": v(-77.01, -10.7) * mm});
            skLineSegment(sketch, "E1373", {"start": v(-60.8, 0.44) * mm, "end": v(-60.59, 0.43) * mm});
            skLineSegment(sketch, "E1374", {"start": v(-63.3, -5.01) * mm, "end": v(-63.06, -5.1) * mm});
            skLineSegment(sketch, "E1375", {"start": v(-83.12, -9.08) * mm, "end": v(-83.32, -9.25) * mm});
            skLineSegment(sketch, "E1376", {"start": v(-90.7, 3.8) * mm, "end": v(-90.88, 3.74) * mm});
            skLineSegment(sketch, "E1377", {"start": v(-76.86, -10.29) * mm, "end": v(-76.93, -10.48) * mm});
            skLineSegment(sketch, "E1378", {"start": v(-60.98, 0.46) * mm, "end": v(-60.8, 0.44) * mm});
            skLineSegment(sketch, "E1379", {"start": v(-63.5, -4.92) * mm, "end": v(-63.3, -5.01) * mm});
            skLineSegment(sketch, "E1380", {"start": v(-82.94, -8.92) * mm, "end": v(-83.12, -9.08) * mm});
            skLineSegment(sketch, "E1381", {"start": v(-90.56, 3.82) * mm, "end": v(-90.7, 3.8) * mm});
            skLineSegment(sketch, "E1382", {"start": v(-76.8, -10.1) * mm, "end": v(-76.86, -10.29) * mm});
            skLineSegment(sketch, "E1383", {"start": v(-61.13, 0.49) * mm, "end": v(-60.98, 0.46) * mm});
            skLineSegment(sketch, "E1384", {"start": v(-63.7, -4.83) * mm, "end": v(-63.5, -4.92) * mm});
            skLineSegment(sketch, "E1385", {"start": v(-82.78, -8.76) * mm, "end": v(-82.94, -8.92) * mm});
            skLineSegment(sketch, "E1386", {"start": v(-90.33, 3.85) * mm, "end": v(-90.56, 3.82) * mm});
            skLineSegment(sketch, "E1387", {"start": v(-76.77, -9.97) * mm, "end": v(-76.8, -10.1) * mm});
            skLineSegment(sketch, "E1388", {"start": v(-61.35, 0.55) * mm, "end": v(-61.13, 0.49) * mm});
            skLineSegment(sketch, "E1389", {"start": v(-63.86, -4.75) * mm, "end": v(-63.7, -4.83) * mm});
            skLineSegment(sketch, "E1390", {"start": v(-82.64, -8.6) * mm, "end": v(-82.78, -8.76) * mm});
            skLineSegment(sketch, "E1391", {"start": v(-89.76, 3.9) * mm, "end": v(-90.33, 3.85) * mm});
            skLineSegment(sketch, "E1392", {"start": v(-76.75, -9.74) * mm, "end": v(-76.77, -9.97) * mm});
            skLineSegment(sketch, "E1393", {"start": v(-61.9, 0.73) * mm, "end": v(-61.35, 0.55) * mm});
            skLineSegment(sketch, "E1394", {"start": v(-63.98, -4.67) * mm, "end": v(-63.86, -4.75) * mm});
            skLineSegment(sketch, "E1395", {"start": v(-82.52, -8.46) * mm, "end": v(-82.64, -8.6) * mm});
            skArc(sketch, "E1396", {"start": v(-89.76, 3.9) * mm, "mid": v(-89.22, 4.16) * mm, "end": v(-89, 4.73) * mm});
            skLineSegment(sketch, "E1397", {"start": v(-76.7, -9.16) * mm, "end": v(-76.75, -9.74) * mm});
            skArc(sketch, "E1398", {"start": v(-61.9, 0.73) * mm, "mid": v(-62.5, 0.69) * mm, "end": v(-62.9, 0.25) * mm});
            skLineSegment(sketch, "E1399", {"start": v(-64.16, -4.52) * mm, "end": v(-63.98, -4.67) * mm});
            skLineSegment(sketch, "E1400", {"start": v(-82.44, -8.34) * mm, "end": v(-82.52, -8.46) * mm});
            skArc(sketch, "E1401", {"start": v(-89, 5.44) * mm, "mid": v(-89.01, 5.08) * mm, "end": v(-89, 4.73) * mm});
            skArc(sketch, "E1402", {"start": v(-79.67, -12.43) * mm, "mid": v(-79.02, -12.57) * mm, "end": v(-78.37, -12.69) * mm});
            skArc(sketch, "E1403", {"start": v(-63.18, -0.4) * mm, "mid": v(-63.04, -0.08) * mm, "end": v(-62.9, 0.25) * mm});
            skLineSegment(sketch, "E1404", {"start": v(-64.6, -4.15) * mm, "end": v(-64.16, -4.52) * mm});
            skLineSegment(sketch, "E1405", {"start": v(-82.33, -8.14) * mm, "end": v(-82.44, -8.34) * mm});
            skArc(sketch, "E1406", {"start": v(-89, 5.44) * mm, "mid": v(-89.22, 6) * mm, "end": v(-89.76, 6.27) * mm});
            skLineSegment(sketch, "E1407", {"start": v(-79.97, -11.46) * mm, "end": v(-79.67, -12.43) * mm});
            skArc(sketch, "E1408", {"start": v(-63.18, -0.4) * mm, "mid": v(-63.2, -1) * mm, "end": v(-62.8, -1.46) * mm});
            skArc(sketch, "E1409", {"start": v(-64.6, -4.15) * mm, "mid": v(-65.17, -3.96) * mm, "end": v(-65.72, -4.2) * mm});
            skLineSegment(sketch, "E1410", {"start": v(-82.06, -7.62) * mm, "end": v(-82.33, -8.14) * mm});
            skLineSegment(sketch, "E1411", {"start": v(-92.5, 7.3) * mm, "end": v(-93.28, 7.94) * mm});
            skLineSegment(sketch, "E1412", {"start": v(-80.13, -10.58) * mm, "end": v(-79.97, -11.46) * mm});
            skLineSegment(sketch, "E1413", {"start": v(-60.66, -3.47) * mm, "end": v(-60.19, -4.36) * mm});
            skArc(sketch, "E1414", {"start": v(-86.06, -9.5) * mm, "mid": v(-85.51, -9.88) * mm, "end": v(-84.95, -10.24) * mm});
            skLineSegment(sketch, "E1415", {"start": v(-91.75, 6.81) * mm, "end": v(-92.5, 7.3) * mm});
            skLineSegment(sketch, "E1416", {"start": v(-80.15, -10.31) * mm, "end": v(-80.13, -10.58) * mm});
            skLineSegment(sketch, "E1417", {"start": v(-61.18, -2.73) * mm, "end": v(-60.66, -3.47) * mm});
            skArc(sketch, "E1418", {"start": v(-66.22, -4.7) * mm, "mid": v(-65.97, -4.46) * mm, "end": v(-65.72, -4.2) * mm});
            skLineSegment(sketch, "E1419", {"start": v(-85.96, -8.5) * mm, "end": v(-86.06, -9.5) * mm});
            skLineSegment(sketch, "E1420", {"start": v(-91.51, 6.7) * mm, "end": v(-91.75, 6.81) * mm});
            skLineSegment(sketch, "E1421", {"start": v(-80.16, -10.07) * mm, "end": v(-80.15, -10.31) * mm});
            skLineSegment(sketch, "E1422", {"start": v(-61.34, -2.52) * mm, "end": v(-61.18, -2.73) * mm});
            skArc(sketch, "E1423", {"start": v(-66.22, -4.7) * mm, "mid": v(-66.47, -5.26) * mm, "end": v(-66.28, -5.83) * mm});
            skLineSegment(sketch, "E1424", {"start": v(-85.77, -7.62) * mm, "end": v(-85.96, -8.5) * mm});
            skLineSegment(sketch, "E1425", {"start": v(-91.3, 6.59) * mm, "end": v(-91.51, 6.7) * mm});
            skLineSegment(sketch, "E1426", {"start": v(-80.16, -9.84) * mm, "end": v(-80.16, -10.07) * mm});
            skLineSegment(sketch, "E1427", {"start": v(-61.5, -2.34) * mm, "end": v(-61.34, -2.52) * mm});
            skLineSegment(sketch, "E1428", {"start": v(-65.06, -8.5) * mm, "end": v(-64.97, -9.5) * mm});
            skLineSegment(sketch, "E1429", {"start": v(-85.7, -7.37) * mm, "end": v(-85.77, -7.62) * mm});
            skLineSegment(sketch, "E1430", {"start": v(-91.08, 6.5) * mm, "end": v(-91.3, 6.59) * mm});
            skLineSegment(sketch, "E1431", {"start": v(-80.15, -9.63) * mm, "end": v(-80.16, -9.84) * mm});
            skLineSegment(sketch, "E1432", {"start": v(-61.67, -2.18) * mm, "end": v(-61.5, -2.34) * mm});
            skLineSegment(sketch, "E1433", {"start": v(-85.52, 17.1) * mm, "end": v(-85.6, 17.3) * mm});
            skLineSegment(sketch, "E1434", {"start": v(-65.26, -7.62) * mm, "end": v(-65.06, -8.5) * mm});
            skLineSegment(sketch, "E1435", {"start": v(-85.6, -7.14) * mm, "end": v(-85.7, -7.37) * mm});
            skLineSegment(sketch, "E1436", {"start": v(-90.88, 6.43) * mm, "end": v(-91.08, 6.5) * mm});
            skLineSegment(sketch, "E1437", {"start": v(-80.13, -9.45) * mm, "end": v(-80.15, -9.63) * mm});
            skLineSegment(sketch, "E1438", {"start": v(-61.83, -2.04) * mm, "end": v(-61.67, -2.18) * mm});
            skLineSegment(sketch, "E1439", {"start": v(-85.43, 16.9) * mm, "end": v(-85.52, 17.1) * mm});
            skLineSegment(sketch, "E1440", {"start": v(-65.33, -7.37) * mm, "end": v(-65.26, -7.62) * mm});
            skLineSegment(sketch, "E1441", {"start": v(-85.52, -6.92) * mm, "end": v(-85.6, -7.14) * mm});
            skLineSegment(sketch, "E1442", {"start": v(-90.7, 6.38) * mm, "end": v(-90.88, 6.43) * mm});
            skLineSegment(sketch, "E1443", {"start": v(-80.1, -9.3) * mm, "end": v(-80.13, -9.45) * mm});
            skLineSegment(sketch, "E1444", {"start": v(-61.97, -1.92) * mm, "end": v(-61.83, -2.04) * mm});
            skLineSegment(sketch, "E1445", {"start": v(-85.34, 16.74) * mm, "end": v(-85.43, 16.9) * mm});
            skLineSegment(sketch, "E1446", {"start": v(-65.42, -7.14) * mm, "end": v(-65.33, -7.37) * mm});
            skLineSegment(sketch, "E1447", {"start": v(-85.43, -6.73) * mm, "end": v(-85.52, -6.92) * mm});
            skLineSegment(sketch, "E1448", {"start": v(-90.56, 6.34) * mm, "end": v(-90.7, 6.38) * mm});
            skLineSegment(sketch, "E1449", {"start": v(-80.04, -9.08) * mm, "end": v(-80.1, -9.3) * mm});
            skLineSegment(sketch, "E1450", {"start": v(-62.1, -1.84) * mm, "end": v(-61.97, -1.92) * mm});
            skLineSegment(sketch, "E1451", {"start": v(-65.5, -6.92) * mm, "end": v(-65.42, -7.14) * mm});
            skLineSegment(sketch, "E1452", {"start": v(-85.34, -6.57) * mm, "end": v(-85.43, -6.73) * mm});
            skLineSegment(sketch, "E1453", {"start": v(-90.33, 6.32) * mm, "end": v(-90.56, 6.34) * mm});
            skLineSegment(sketch, "E1454", {"start": v(-79.87, -8.53) * mm, "end": v(-80.04, -9.08) * mm});
            skLineSegment(sketch, "E1455", {"start": v(-62.3, -1.73) * mm, "end": v(-62.1, -1.84) * mm});
            skLineSegment(sketch, "E1456", {"start": v(-65.6, -6.73) * mm, "end": v(-65.5, -6.92) * mm});
            skLineSegment(sketch, "E1457", {"start": v(-85.26, -6.45) * mm, "end": v(-85.34, -6.57) * mm});
            skLineSegment(sketch, "E1458", {"start": v(-89.76, 6.27) * mm, "end": v(-90.33, 6.32) * mm});
            skArc(sketch, "E1459", {"start": v(-79.87, -8.53) * mm, "mid": v(-79.9, -7.93) * mm, "end": v(-80.35, -7.52) * mm});
            skLineSegment(sketch, "E1460", {"start": v(-62.8, -1.46) * mm, "end": v(-62.3, -1.73) * mm});
            skLineSegment(sketch, "E1461", {"start": v(-65.68, -6.57) * mm, "end": v(-65.6, -6.73) * mm});
            skLineSegment(sketch, "E1462", {"start": v(-85.12, -6.27) * mm, "end": v(-85.26, -6.45) * mm});
            skArc(sketch, "E1463", {"start": v(-93.02, 9.25) * mm, "mid": v(-93.17, 8.6) * mm, "end": v(-93.28, 7.94) * mm});
            skArc(sketch, "E1464", {"start": v(-81, -7.25) * mm, "mid": v(-80.68, -7.39) * mm, "end": v(-80.35, -7.52) * mm});
            skArc(sketch, "E1465", {"start": v(-60.93, -5.46) * mm, "mid": v(-60.55, -4.92) * mm, "end": v(-60.19, -4.36) * mm});
            skLineSegment(sketch, "E1466", {"start": v(-65.76, -6.45) * mm, "end": v(-65.68, -6.57) * mm});
            skLineSegment(sketch, "E1467", {"start": v(-84.75, -5.83) * mm, "end": v(-85.12, -6.27) * mm});
            skLineSegment(sketch, "E1468", {"start": v(-92.06, 9.54) * mm, "end": v(-93.02, 9.25) * mm});
            skArc(sketch, "E1469", {"start": v(-81, -7.25) * mm, "mid": v(-81.6, -7.23) * mm, "end": v(-82.06, -7.62) * mm});
            skLineSegment(sketch, "E1470", {"start": v(-61.93, -5.36) * mm, "end": v(-60.93, -5.46) * mm});
            skLineSegment(sketch, "E1471", {"start": v(-65.9, -6.27) * mm, "end": v(-65.76, -6.45) * mm});
            skArc(sketch, "E1472", {"start": v(-84.75, -5.83) * mm, "mid": v(-84.55, -5.26) * mm, "end": v(-84.8, -4.7) * mm});
            skLineSegment(sketch, "E1473", {"start": v(-91.17, 9.7) * mm, "end": v(-92.06, 9.54) * mm});
            skLineSegment(sketch, "E1474", {"start": v(-84.06, -9.77) * mm, "end": v(-84.95, -10.24) * mm});
            skLineSegment(sketch, "E1475", {"start": v(-62.81, -5.17) * mm, "end": v(-61.93, -5.36) * mm});
            skLineSegment(sketch, "E1476", {"start": v(-66.28, -5.83) * mm, "end": v(-65.9, -6.27) * mm});
            skLineSegment(sketch, "E1477", {"start": v(-91.51, 3.48) * mm, "end": v(-91.75, 3.36) * mm});
            skLineSegment(sketch, "E1478", {"start": v(-91.3, 3.58) * mm, "end": v(-91.51, 3.48) * mm});
            skLineSegment(sketch, "E1479", {"start": v(-91.08, 3.67) * mm, "end": v(-91.3, 3.58) * mm});
            skLineSegment(sketch, "E1480", {"start": v(-75.51, 2.18) * mm, "end": v(-75.51, 1.98) * mm});
            skLineSegment(sketch, "E1481", {"start": v(-74.06, 2.57) * mm, "end": v(-73.96, 2.4) * mm});
            skLineSegment(sketch, "E1482", {"start": v(-73, 3.63) * mm, "end": v(-72.83, 3.53) * mm});
            skLineSegment(sketch, "E1483", {"start": v(-72.61, 5.08) * mm, "end": v(-72.41, 5.08) * mm});
            skLineSegment(sketch, "E1484", {"start": v(-73, 6.53) * mm, "end": v(-72.83, 6.63) * mm});
            skLineSegment(sketch, "E1485", {"start": v(-74.06, 7.6) * mm, "end": v(-73.96, 7.77) * mm});
            skArc(sketch, "E1486", {"start": v(-73, 6.53) * mm, "mid": v(-73.46, 7.13) * mm, "end": v(-74.06, 7.6) * mm});
            skArc(sketch, "E1487", {"start": v(-72.41, 5.08) * mm, "mid": v(-72.52, 5.89) * mm, "end": v(-72.83, 6.63) * mm});
            skArc(sketch, "E1488", {"start": v(-73, 3.63) * mm, "mid": v(-72.71, 4.33) * mm, "end": v(-72.61, 5.08) * mm});
            skArc(sketch, "E1489", {"start": v(-73.96, 2.4) * mm, "mid": v(-73.32, 2.9) * mm, "end": v(-72.83, 3.53) * mm});
            skArc(sketch, "E1490", {"start": v(-75.51, 2.18) * mm, "mid": v(-74.76, 2.28) * mm, "end": v(-74.06, 2.57) * mm});
            skArc(sketch, "E1491", {"start": v(-77.06, 2.4) * mm, "mid": v(-76.31, 2.09) * mm, "end": v(-75.51, 1.98) * mm});
            skArc(sketch, "E1492", {"start": v(-78.61, 5.08) * mm, "mid": v(-78.5, 4.28) * mm, "end": v(-78.2, 3.53) * mm});
            skArc(sketch, "E1493", {"start": v(-77.06, 7.77) * mm, "mid": v(-77.7, 7.28) * mm, "end": v(-78.2, 6.63) * mm});
            skArc(sketch, "E1494", {"start": v(-78.02, 6.53) * mm, "mid": v(-78.31, 5.83) * mm, "end": v(-78.41, 5.08) * mm});
            skArc(sketch, "E1495", {"start": v(-73.96, 7.77) * mm, "mid": v(-74.71, 8.08) * mm, "end": v(-75.51, 8.18) * mm});
            skArc(sketch, "E1496", {"start": v(-75.51, 7.98) * mm, "mid": v(-76.26, 7.88) * mm, "end": v(-76.96, 7.6) * mm});
            skLineSegment(sketch, "E1497", {"start": v(-75.51, 7.98) * mm, "end": v(-75.51, 8.18) * mm});
            skLineSegment(sketch, "E1498", {"start": v(-76.96, 7.6) * mm, "end": v(-77.06, 7.77) * mm});
            skLineSegment(sketch, "E1499", {"start": v(-78.02, 6.53) * mm, "end": v(-78.2, 6.63) * mm});
            skLineSegment(sketch, "E1500", {"start": v(-78.41, 5.08) * mm, "end": v(-78.61, 5.08) * mm});
            skLineSegment(sketch, "E1501", {"start": v(-78.02, 3.63) * mm, "end": v(-78.2, 3.53) * mm});
            skLineSegment(sketch, "E1502", {"start": v(-76.96, 2.57) * mm, "end": v(-77.06, 2.4) * mm});
            skCircle(sketch, "E1503", {"center": v(34.56, 61.46) * mm, "radius": 30 * mm});
            skArc(sketch, "E1504", {"start": v(29.02, 64.66) * mm, "mid": v(28.38, 63.12) * mm, "end": v(28.16, 61.46) * mm});
            skCircle(sketch, "E1505", {"center": v(61.06, 61.46) * mm, "radius": 0.5 * mm});
            skCircle(sketch, "E1506", {"center": v(34.56, 34.96) * mm, "radius": 0.75 * mm});
            skCircle(sketch, "E1507", {"center": v(8.06, 61.46) * mm, "radius": 1 * mm});
            skLineSegment(sketch, "E1508", {"start": v(-57.7, -53.04) * mm, "end": v(-57.3, -52.64) * mm});
            skLineSegment(sketch, "E1509", {"start": v(20.74, -9.58) * mm, "end": v(20.47, -10.1) * mm});
            skArc(sketch, "E1510", {"start": v(31.26, 67.18) * mm, "mid": v(29.9, 66.13) * mm, "end": v(28.85, 64.76) * mm});
            skLineSegment(sketch, "E1511", {"start": v(34.56, 67.86) * mm, "end": v(34.56, 68.06) * mm});
            skLineSegment(sketch, "E1512.1.0", {"start": v(31.36, 67) * mm, "end": v(31.26, 67.18) * mm});
            skLineSegment(sketch, "E1512.2.0", {"start": v(29.02, 64.66) * mm, "end": v(28.85, 64.76) * mm});
            skLineSegment(sketch, "E1512.3.0", {"start": v(28.16, 61.46) * mm, "end": v(27.96, 61.46) * mm});
            skLineSegment(sketch, "E1512.4.0", {"start": v(29.02, 58.26) * mm, "end": v(28.85, 58.16) * mm});
            skLineSegment(sketch, "E1512.5.0", {"start": v(31.36, 55.92) * mm, "end": v(31.26, 55.75) * mm});
            skLineSegment(sketch, "E1512.6.0", {"start": v(34.56, 55.06) * mm, "end": v(34.56, 54.86) * mm});
            skLineSegment(sketch, "E1512.7.0", {"start": v(37.76, 55.92) * mm, "end": v(37.86, 55.75) * mm});
            skLineSegment(sketch, "E1512.8.0", {"start": v(40.1, 58.26) * mm, "end": v(40.28, 58.16) * mm});
            skLineSegment(sketch, "E1512.9.0", {"start": v(40.96, 61.46) * mm, "end": v(41.16, 61.46) * mm});
            skLineSegment(sketch, "E1512.10.0", {"start": v(40.1, 64.66) * mm, "end": v(40.28, 64.76) * mm});
            skLineSegment(sketch, "E1512.11.0", {"start": v(37.76, 67) * mm, "end": v(37.86, 67.18) * mm});
            skArc(sketch, "E1513.trimOffspring", {"start": v(37.86, 67.18) * mm, "mid": v(36.27, 67.84) * mm, "end": v(34.56, 68.06) * mm});
            skArc(sketch, "E1514.trimOffspring", {"start": v(41.16, 61.46) * mm, "mid": v(40.94, 63.17) * mm, "end": v(40.28, 64.76) * mm});
            skArc(sketch, "E1515.trimOffspring", {"start": v(37.86, 55.75) * mm, "mid": v(39.23, 56.8) * mm, "end": v(40.28, 58.16) * mm});
            skArc(sketch, "E1516.trimOffspring", {"start": v(31.26, 55.75) * mm, "mid": v(32.85, 55.09) * mm, "end": v(34.56, 54.86) * mm});
            skArc(sketch, "E1517.trimOffspring", {"start": v(27.96, 61.46) * mm, "mid": v(28.19, 59.75) * mm, "end": v(28.85, 58.16) * mm});
            skArc(sketch, "E1518.trimOffspring", {"start": v(29.02, 58.26) * mm, "mid": v(30.04, 56.94) * mm, "end": v(31.36, 55.92) * mm});
            skArc(sketch, "E1519.trimOffspring", {"start": v(34.56, 55.06) * mm, "mid": v(36.22, 55.28) * mm, "end": v(37.76, 55.92) * mm});
            skArc(sketch, "E1520.trimOffspring", {"start": v(40.1, 58.26) * mm, "mid": v(40.74, 59.8) * mm, "end": v(40.96, 61.46) * mm});
            skArc(sketch, "E1521.trimOffspring", {"start": v(40.1, 64.66) * mm, "mid": v(39.09, 65.99) * mm, "end": v(37.76, 67) * mm});
            skArc(sketch, "E1522.trimOffspring", {"start": v(34.56, 67.86) * mm, "mid": v(32.9, 67.64) * mm, "end": v(31.36, 67) * mm});
            skLineSegment(sketch, "E1523", {"start": v(-152.21, 15.46) * mm, "end": v(-152.3, 15.58) * mm});
            skLineSegment(sketch, "E1524", {"start": v(-152.07, 15.28) * mm, "end": v(-152.21, 15.46) * mm});
            skLineSegment(sketch, "E1525", {"start": v(-151.7, 14.84) * mm, "end": v(-152.07, 15.28) * mm});
            skArc(sketch, "E1526", {"start": v(-151.9, 19.25) * mm, "mid": v(-152.46, 18.9) * mm, "end": v(-153, 18.51) * mm});
            skLineSegment(sketch, "E1527", {"start": v(-151.01, 18.78) * mm, "end": v(-151.9, 19.25) * mm});
            skLineSegment(sketch, "E1528", {"start": v(-150.27, 18.26) * mm, "end": v(-151.01, 18.78) * mm});
            skLineSegment(sketch, "E1529", {"start": v(-150.07, 18.1) * mm, "end": v(-150.27, 18.26) * mm});
            skLineSegment(sketch, "E1530", {"start": v(-149.89, 17.93) * mm, "end": v(-150.07, 18.1) * mm});
            skLineSegment(sketch, "E1531", {"start": v(-149.73, 17.77) * mm, "end": v(-149.89, 17.93) * mm});
            skLineSegment(sketch, "E1532", {"start": v(-149.59, 17.61) * mm, "end": v(-149.73, 17.77) * mm});
            skLineSegment(sketch, "E1533", {"start": v(-149.47, 17.47) * mm, "end": v(-149.59, 17.61) * mm});
            skLineSegment(sketch, "E1534", {"start": v(-149.39, 17.35) * mm, "end": v(-149.47, 17.47) * mm});
            skLineSegment(sketch, "E1535", {"start": v(-149.28, 17.15) * mm, "end": v(-149.39, 17.35) * mm});
            skLineSegment(sketch, "E1536", {"start": v(-149, 16.63) * mm, "end": v(-149.28, 17.15) * mm});
            skArc(sketch, "E1537", {"start": v(-149, 16.63) * mm, "mid": v(-148.56, 16.24) * mm, "end": v(-147.95, 16.26) * mm});
            skArc(sketch, "E1538", {"start": v(-147.3, 16.53) * mm, "mid": v(-147.63, 16.4) * mm, "end": v(-147.95, 16.26) * mm});
            skArc(sketch, "E1539", {"start": v(-147.3, 16.53) * mm, "mid": v(-146.86, 16.94) * mm, "end": v(-146.82, 17.54) * mm});
            skLineSegment(sketch, "E1540", {"start": v(-146.92, 20.47) * mm, "end": v(-146.62, 21.44) * mm});
            skLineSegment(sketch, "E1541", {"start": v(-147.08, 19.59) * mm, "end": v(-146.92, 20.47) * mm});
            skLineSegment(sketch, "E1542", {"start": v(-147.1, 19.32) * mm, "end": v(-147.08, 19.59) * mm});
            skLineSegment(sketch, "E1543", {"start": v(-147.11, 19.08) * mm, "end": v(-147.1, 19.32) * mm});
            skLineSegment(sketch, "E1544", {"start": v(-147.11, 18.85) * mm, "end": v(-147.11, 19.08) * mm});
            skLineSegment(sketch, "E1545", {"start": v(-147.1, 18.64) * mm, "end": v(-147.11, 18.85) * mm});
            skLineSegment(sketch, "E1546", {"start": v(-147.08, 18.46) * mm, "end": v(-147.1, 18.64) * mm});
            skLineSegment(sketch, "E1547", {"start": v(-147.06, 18.31) * mm, "end": v(-147.08, 18.46) * mm});
            skLineSegment(sketch, "E1548", {"start": v(-147, 18.1) * mm, "end": v(-147.06, 18.31) * mm});
            skLineSegment(sketch, "E1549", {"start": v(-146.82, 17.54) * mm, "end": v(-147, 18.1) * mm});
            skArc(sketch, "E1550", {"start": v(-145.32, 21.7) * mm, "mid": v(-145.97, 21.58) * mm, "end": v(-146.62, 21.44) * mm});
            skLineSegment(sketch, "E1551", {"start": v(-144.68, 20.92) * mm, "end": v(-145.32, 21.7) * mm});
            skLineSegment(sketch, "E1552", {"start": v(-144.2, 20.16) * mm, "end": v(-144.68, 20.92) * mm});
            skLineSegment(sketch, "E1553", {"start": v(-144.07, 19.93) * mm, "end": v(-144.2, 20.16) * mm});
            skLineSegment(sketch, "E1554", {"start": v(-143.96, 19.7) * mm, "end": v(-144.07, 19.93) * mm});
            skLineSegment(sketch, "E1555", {"start": v(-143.88, 19.5) * mm, "end": v(-143.96, 19.7) * mm});
            skLineSegment(sketch, "E1556", {"start": v(-143.8, 19.3) * mm, "end": v(-143.88, 19.5) * mm});
            skLineSegment(sketch, "E1557", {"start": v(-143.75, 19.12) * mm, "end": v(-143.8, 19.3) * mm});
            skLineSegment(sketch, "E1558", {"start": v(-143.72, 18.98) * mm, "end": v(-143.75, 19.12) * mm});
            skLineSegment(sketch, "E1559", {"start": v(-143.7, 18.75) * mm, "end": v(-143.72, 18.98) * mm});
            skLineSegment(sketch, "E1560", {"start": v(-143.65, 18.17) * mm, "end": v(-143.7, 18.75) * mm});
            skArc(sketch, "E1561", {"start": v(-143.65, 18.17) * mm, "mid": v(-143.38, 17.63) * mm, "end": v(-142.82, 17.42) * mm});
            skArc(sketch, "E1562", {"start": v(-142.1, 17.42) * mm, "mid": v(-142.46, 17.43) * mm, "end": v(-142.82, 17.42) * mm});
            skArc(sketch, "E1563", {"start": v(-142.1, 17.42) * mm, "mid": v(-141.54, 17.63) * mm, "end": v(-141.28, 18.17) * mm});
            skLineSegment(sketch, "E1564", {"start": v(-140.25, 20.92) * mm, "end": v(-139.6, 21.7) * mm});
            skLineSegment(sketch, "E1565", {"start": v(-140.73, 20.16) * mm, "end": v(-140.25, 20.92) * mm});
            skLineSegment(sketch, "E1566", {"start": v(-140.86, 19.93) * mm, "end": v(-140.73, 20.16) * mm});
            skLineSegment(sketch, "E1567", {"start": v(-140.96, 19.7) * mm, "end": v(-140.86, 19.93) * mm});
            skLineSegment(sketch, "E1568", {"start": v(-141.05, 19.5) * mm, "end": v(-140.96, 19.7) * mm});
            skLineSegment(sketch, "E1569", {"start": v(-141.12, 19.3) * mm, "end": v(-141.05, 19.5) * mm});
            skLineSegment(sketch, "E1570", {"start": v(-141.17, 19.12) * mm, "end": v(-141.12, 19.3) * mm});
            skLineSegment(sketch, "E1571", {"start": v(-141.2, 18.98) * mm, "end": v(-141.17, 19.12) * mm});
            skLineSegment(sketch, "E1572", {"start": v(-141.23, 18.75) * mm, "end": v(-141.2, 18.98) * mm});
            skLineSegment(sketch, "E1573", {"start": v(-141.28, 18.17) * mm, "end": v(-141.23, 18.75) * mm});
            skArc(sketch, "E1574", {"start": v(-138.3, 21.44) * mm, "mid": v(-138.95, 21.58) * mm, "end": v(-139.6, 21.7) * mm});
            skLineSegment(sketch, "E1575", {"start": v(-138, 20.47) * mm, "end": v(-138.3, 21.44) * mm});
            skLineSegment(sketch, "E1576", {"start": v(-137.85, 19.59) * mm, "end": v(-138, 20.47) * mm});
            skLineSegment(sketch, "E1577", {"start": v(-137.82, 19.32) * mm, "end": v(-137.85, 19.59) * mm});
            skLineSegment(sketch, "E1578", {"start": v(-137.81, 19.08) * mm, "end": v(-137.82, 19.32) * mm});
            skLineSegment(sketch, "E1579", {"start": v(-137.81, 18.85) * mm, "end": v(-137.81, 19.08) * mm});
            skLineSegment(sketch, "E1580", {"start": v(-137.82, 18.64) * mm, "end": v(-137.81, 18.85) * mm});
            skLineSegment(sketch, "E1581", {"start": v(-137.84, 18.46) * mm, "end": v(-137.82, 18.64) * mm});
            skLineSegment(sketch, "E1582", {"start": v(-137.87, 18.31) * mm, "end": v(-137.84, 18.46) * mm});
            skLineSegment(sketch, "E1583", {"start": v(-125.91, -0.53) * mm, "end": v(-124.95, -0.24) * mm});
            skArc(sketch, "E1584", {"start": v(-124.95, -0.24) * mm, "mid": v(-124.8, 0.41) * mm, "end": v(-124.7, 1.07) * mm});
            skLineSegment(sketch, "E1585", {"start": v(-128.22, 2.74) * mm, "end": v(-127.64, 2.7) * mm});
            skLineSegment(sketch, "E1586", {"start": v(-127.64, 2.7) * mm, "end": v(-127.41, 2.67) * mm});
            skLineSegment(sketch, "E1587", {"start": v(-127.41, 2.67) * mm, "end": v(-127.27, 2.63) * mm});
            skLineSegment(sketch, "E1588", {"start": v(-127.27, 2.63) * mm, "end": v(-127.1, 2.58) * mm});
            skLineSegment(sketch, "E1589", {"start": v(-127.1, 2.58) * mm, "end": v(-126.9, 2.51) * mm});
            skLineSegment(sketch, "E1590", {"start": v(-126.9, 2.51) * mm, "end": v(-126.68, 2.42) * mm});
            skLineSegment(sketch, "E1591", {"start": v(-126.68, 2.42) * mm, "end": v(-126.46, 2.32) * mm});
            skLineSegment(sketch, "E1592", {"start": v(-126.46, 2.32) * mm, "end": v(-126.23, 2.2) * mm});
            skLineSegment(sketch, "E1593", {"start": v(-126.23, 2.2) * mm, "end": v(-125.47, 1.7) * mm});
            skLineSegment(sketch, "E1594", {"start": v(-125.47, 1.7) * mm, "end": v(-124.7, 1.07) * mm});
            skArc(sketch, "E1595", {"start": v(-128.97, 3.57) * mm, "mid": v(-128.76, 3) * mm, "end": v(-128.22, 2.74) * mm});
            skArc(sketch, "E1596", {"start": v(-128.97, 3.57) * mm, "mid": v(-128.96, 3.93) * mm, "end": v(-128.97, 4.28) * mm});
            skArc(sketch, "E1597", {"start": v(-128.22, 5.11) * mm, "mid": v(-128.76, 4.85) * mm, "end": v(-128.97, 4.28) * mm});
            skLineSegment(sketch, "E1598", {"start": v(-128.22, 5.11) * mm, "end": v(-127.64, 5.16) * mm});
            skLineSegment(sketch, "E1599", {"start": v(-127.64, 5.16) * mm, "end": v(-127.41, 5.19) * mm});
            skLineSegment(sketch, "E1600", {"start": v(-127.41, 5.19) * mm, "end": v(-127.27, 5.22) * mm});
            skLineSegment(sketch, "E1601", {"start": v(-127.27, 5.22) * mm, "end": v(-127.1, 5.27) * mm});
            skLineSegment(sketch, "E1602", {"start": v(-127.1, 5.27) * mm, "end": v(-126.9, 5.34) * mm});
            skLineSegment(sketch, "E1603", {"start": v(-126.9, 5.34) * mm, "end": v(-126.68, 5.43) * mm});
            skLineSegment(sketch, "E1604", {"start": v(-126.68, 5.43) * mm, "end": v(-126.46, 5.53) * mm});
            skLineSegment(sketch, "E1605", {"start": v(-126.46, 5.53) * mm, "end": v(-126.23, 5.66) * mm});
            skLineSegment(sketch, "E1606", {"start": v(-126.23, 5.66) * mm, "end": v(-125.47, 6.14) * mm});
            skLineSegment(sketch, "E1607", {"start": v(-125.47, 6.14) * mm, "end": v(-124.7, 6.78) * mm});
            skArc(sketch, "E1608", {"start": v(-124.7, 6.78) * mm, "mid": v(-124.8, 7.44) * mm, "end": v(-124.95, 8.09) * mm});
            skLineSegment(sketch, "E1609", {"start": v(-128.85, 8.28) * mm, "end": v(-128.3, 8.46) * mm});
            skLineSegment(sketch, "E1610", {"start": v(-128.3, 8.46) * mm, "end": v(-128.08, 8.52) * mm});
            skLineSegment(sketch, "E1611", {"start": v(-128.08, 8.52) * mm, "end": v(-127.93, 8.55) * mm});
            skLineSegment(sketch, "E1612", {"start": v(-127.93, 8.55) * mm, "end": v(-127.75, 8.57) * mm});
            skLineSegment(sketch, "E1613", {"start": v(-127.75, 8.57) * mm, "end": v(-127.54, 8.58) * mm});
            skLineSegment(sketch, "E1614", {"start": v(-127.54, 8.58) * mm, "end": v(-127.31, 8.58) * mm});
            skLineSegment(sketch, "E1615", {"start": v(-127.31, 8.58) * mm, "end": v(-127.06, 8.57) * mm});
            skLineSegment(sketch, "E1616", {"start": v(-127.06, 8.57) * mm, "end": v(-126.8, 8.54) * mm});
            skLineSegment(sketch, "E1617", {"start": v(-126.8, 8.54) * mm, "end": v(-125.91, 8.38) * mm});
            skLineSegment(sketch, "E1618", {"start": v(-125.91, 8.38) * mm, "end": v(-124.95, 8.09) * mm});
            skArc(sketch, "E1619", {"start": v(-129.86, 8.76) * mm, "mid": v(-129.45, 8.32) * mm, "end": v(-128.85, 8.28) * mm});
            skArc(sketch, "E1620", {"start": v(-129.86, 8.76) * mm, "mid": v(-130, 9.1) * mm, "end": v(-130.13, 9.42) * mm});
            skArc(sketch, "E1621", {"start": v(-129.76, 10.47) * mm, "mid": v(-130.15, 10.02) * mm, "end": v(-130.13, 9.42) * mm});
            skLineSegment(sketch, "E1622", {"start": v(-129.76, 10.47) * mm, "end": v(-129.24, 10.74) * mm});
            skLineSegment(sketch, "E1623", {"start": v(-129.24, 10.74) * mm, "end": v(-129.04, 10.85) * mm});
            skLineSegment(sketch, "E1624", {"start": v(-129.04, 10.85) * mm, "end": v(-128.92, 10.93) * mm});
            skLineSegment(sketch, "E1625", {"start": v(-128.92, 10.93) * mm, "end": v(-128.78, 11.05) * mm});
            skLineSegment(sketch, "E1626", {"start": v(-128.78, 11.05) * mm, "end": v(-128.62, 11.19) * mm});
            skLineSegment(sketch, "E1627", {"start": v(-128.62, 11.19) * mm, "end": v(-128.46, 11.35) * mm});
            skLineSegment(sketch, "E1628", {"start": v(-128.46, 11.35) * mm, "end": v(-128.3, 11.53) * mm});
            skLineSegment(sketch, "E1629", {"start": v(-128.3, 11.53) * mm, "end": v(-128.13, 11.74) * mm});
            skLineSegment(sketch, "E1630", {"start": v(-128.13, 11.74) * mm, "end": v(-127.61, 12.48) * mm});
            skLineSegment(sketch, "E1631", {"start": v(-127.61, 12.48) * mm, "end": v(-127.14, 13.37) * mm});
            skArc(sketch, "E1632", {"start": v(-127.14, 13.37) * mm, "mid": v(-127.5, 13.93) * mm, "end": v(-127.88, 14.47) * mm});
            skLineSegment(sketch, "E1633", {"start": v(-131.55, 13.16) * mm, "end": v(-131.1, 13.53) * mm});
            skLineSegment(sketch, "E1634", {"start": v(-131.1, 13.53) * mm, "end": v(-130.93, 13.68) * mm});
            skLineSegment(sketch, "E1635", {"start": v(-130.93, 13.68) * mm, "end": v(-130.8, 13.76) * mm});
            skLineSegment(sketch, "E1636", {"start": v(-130.8, 13.76) * mm, "end": v(-130.64, 13.84) * mm});
            skLineSegment(sketch, "E1637", {"start": v(-130.64, 13.84) * mm, "end": v(-130.46, 13.93) * mm});
            skLineSegment(sketch, "E1638", {"start": v(-130.46, 13.93) * mm, "end": v(-130.24, 14.02) * mm});
            skLineSegment(sketch, "E1639", {"start": v(-130.24, 14.02) * mm, "end": v(-130.01, 14.1) * mm});
            skLineSegment(sketch, "E1640", {"start": v(-130.01, 14.1) * mm, "end": v(-129.76, 14.18) * mm});
            skLineSegment(sketch, "E1641", {"start": v(-129.76, 14.18) * mm, "end": v(-128.88, 14.37) * mm});
            skLineSegment(sketch, "E1642", {"start": v(-128.88, 14.37) * mm, "end": v(-127.88, 14.47) * mm});
            skArc(sketch, "E1643", {"start": v(-132.67, 13.22) * mm, "mid": v(-132.12, 12.97) * mm, "end": v(-131.55, 13.16) * mm});
            skArc(sketch, "E1644", {"start": v(-132.67, 13.22) * mm, "mid": v(-132.92, 13.47) * mm, "end": v(-133.17, 13.72) * mm});
            skArc(sketch, "E1645", {"start": v(-133.23, 14.84) * mm, "mid": v(-133.42, 14.27) * mm, "end": v(-133.17, 13.72) * mm});
            skLineSegment(sketch, "E1646", {"start": v(-133.23, 14.84) * mm, "end": v(-132.86, 15.28) * mm});
            skLineSegment(sketch, "E1647", {"start": v(-132.86, 15.28) * mm, "end": v(-132.71, 15.46) * mm});
            skLineSegment(sketch, "E1648", {"start": v(-132.71, 15.46) * mm, "end": v(-132.63, 15.58) * mm});
            skLineSegment(sketch, "E1649", {"start": v(-132.63, 15.58) * mm, "end": v(-132.55, 15.74) * mm});
            skLineSegment(sketch, "E1650", {"start": v(-132.55, 15.74) * mm, "end": v(-132.45, 15.93) * mm});
            skLineSegment(sketch, "E1651", {"start": v(-132.45, 15.93) * mm, "end": v(-132.37, 16.15) * mm});
            skLineSegment(sketch, "E1652", {"start": v(-132.37, 16.15) * mm, "end": v(-132.28, 16.38) * mm});
            skLineSegment(sketch, "E1653", {"start": v(-132.28, 16.38) * mm, "end": v(-132.2, 16.63) * mm});
            skLineSegment(sketch, "E1654", {"start": v(-132.2, 16.63) * mm, "end": v(-132.01, 17.51) * mm});
            skLineSegment(sketch, "E1655", {"start": v(-132.01, 17.51) * mm, "end": v(-131.92, 18.51) * mm});
            skArc(sketch, "E1656", {"start": v(-131.92, 18.51) * mm, "mid": v(-132.46, 18.9) * mm, "end": v(-133.02, 19.25) * mm});
            skLineSegment(sketch, "E1657", {"start": v(-135.92, 16.63) * mm, "end": v(-135.65, 17.15) * mm});
            skLineSegment(sketch, "E1658", {"start": v(-135.65, 17.15) * mm, "end": v(-135.54, 17.35) * mm});
            skLineSegment(sketch, "E1659", {"start": v(-135.54, 17.35) * mm, "end": v(-135.45, 17.47) * mm});
            skLineSegment(sketch, "E1660", {"start": v(-135.45, 17.47) * mm, "end": v(-135.34, 17.61) * mm});
            skLineSegment(sketch, "E1661", {"start": v(-135.34, 17.61) * mm, "end": v(-135.2, 17.77) * mm});
            skLineSegment(sketch, "E1662", {"start": v(-135.2, 17.77) * mm, "end": v(-135.04, 17.93) * mm});
            skLineSegment(sketch, "E1663", {"start": v(-135.04, 17.93) * mm, "end": v(-134.85, 18.1) * mm});
            skLineSegment(sketch, "E1664", {"start": v(-134.85, 18.1) * mm, "end": v(-134.65, 18.26) * mm});
            skLineSegment(sketch, "E1665", {"start": v(-134.65, 18.26) * mm, "end": v(-133.91, 18.78) * mm});
            skLineSegment(sketch, "E1666", {"start": v(-133.91, 18.78) * mm, "end": v(-133.02, 19.25) * mm});
            skArc(sketch, "E1667", {"start": v(-136.97, 16.26) * mm, "mid": v(-136.37, 16.24) * mm, "end": v(-135.92, 16.63) * mm});
            skArc(sketch, "E1668", {"start": v(-136.97, 16.26) * mm, "mid": v(-137.3, 16.4) * mm, "end": v(-137.62, 16.53) * mm});
            skArc(sketch, "E1669", {"start": v(-138.1, 17.54) * mm, "mid": v(-138.07, 16.94) * mm, "end": v(-137.62, 16.53) * mm});
            skLineSegment(sketch, "E1670", {"start": v(-138.1, 17.54) * mm, "end": v(-137.93, 18.1) * mm});
            skLineSegment(sketch, "E1671", {"start": v(-137.93, 18.1) * mm, "end": v(-137.87, 18.31) * mm});
            skLineSegment(sketch, "E1672", {"start": v(-152.56, 16.15) * mm, "end": v(-152.64, 16.38) * mm});
            skLineSegment(sketch, "E1673", {"start": v(-152.64, 16.38) * mm, "end": v(-152.72, 16.63) * mm});
            skLineSegment(sketch, "E1674", {"start": v(-152.72, 16.63) * mm, "end": v(-152.91, 17.51) * mm});
            skLineSegment(sketch, "E1675", {"start": v(-152.91, 17.51) * mm, "end": v(-153, 18.51) * mm});
            skArc(sketch, "E1676", {"start": v(-151.76, 13.72) * mm, "mid": v(-151.5, 14.27) * mm, "end": v(-151.7, 14.84) * mm});
            skArc(sketch, "E1677", {"start": v(-151.76, 13.72) * mm, "mid": v(-152, 13.47) * mm, "end": v(-152.26, 13.22) * mm});
            skArc(sketch, "E1678", {"start": v(-153.37, 13.16) * mm, "mid": v(-152.8, 12.97) * mm, "end": v(-152.26, 13.22) * mm});
            skLineSegment(sketch, "E1679", {"start": v(-153.37, 13.16) * mm, "end": v(-153.82, 13.53) * mm});
            skLineSegment(sketch, "E1680", {"start": v(-153.82, 13.53) * mm, "end": v(-154, 13.68) * mm});
            skLineSegment(sketch, "E1681", {"start": v(-154, 13.68) * mm, "end": v(-154.12, 13.76) * mm});
            skLineSegment(sketch, "E1682", {"start": v(-154.12, 13.76) * mm, "end": v(-154.28, 13.84) * mm});
            skLineSegment(sketch, "E1683", {"start": v(-154.28, 13.84) * mm, "end": v(-154.47, 13.93) * mm});
            skLineSegment(sketch, "E1684", {"start": v(-154.47, 13.93) * mm, "end": v(-154.68, 14.02) * mm});
            skLineSegment(sketch, "E1685", {"start": v(-154.68, 14.02) * mm, "end": v(-154.91, 14.1) * mm});
            skLineSegment(sketch, "E1686", {"start": v(-154.91, 14.1) * mm, "end": v(-155.16, 14.18) * mm});
            skLineSegment(sketch, "E1687", {"start": v(-155.16, 14.18) * mm, "end": v(-156.05, 14.37) * mm});
            skLineSegment(sketch, "E1688", {"start": v(-156.05, 14.37) * mm, "end": v(-157.05, 14.47) * mm});
            skArc(sketch, "E1689", {"start": v(-157.05, 14.47) * mm, "mid": v(-157.43, 13.93) * mm, "end": v(-157.79, 13.37) * mm});
            skLineSegment(sketch, "E1690", {"start": v(-155.17, 10.47) * mm, "end": v(-155.68, 10.74) * mm});
            skLineSegment(sketch, "E1691", {"start": v(-155.68, 10.74) * mm, "end": v(-155.88, 10.85) * mm});
            skLineSegment(sketch, "E1692", {"start": v(-155.88, 10.85) * mm, "end": v(-156, 10.93) * mm});
            skLineSegment(sketch, "E1693", {"start": v(-156, 10.93) * mm, "end": v(-156.15, 11.05) * mm});
            skLineSegment(sketch, "E1694", {"start": v(-156.15, 11.05) * mm, "end": v(-156.3, 11.19) * mm});
            skLineSegment(sketch, "E1695", {"start": v(-156.3, 11.19) * mm, "end": v(-156.47, 11.35) * mm});
            skLineSegment(sketch, "E1696", {"start": v(-156.47, 11.35) * mm, "end": v(-156.63, 11.53) * mm});
            skLineSegment(sketch, "E1697", {"start": v(-156.63, 11.53) * mm, "end": v(-156.8, 11.74) * mm});
            skLineSegment(sketch, "E1698", {"start": v(-156.8, 11.74) * mm, "end": v(-157.31, 12.48) * mm});
            skLineSegment(sketch, "E1699", {"start": v(-157.31, 12.48) * mm, "end": v(-157.79, 13.37) * mm});
            skArc(sketch, "E1700", {"start": v(-154.8, 9.42) * mm, "mid": v(-154.77, 10.02) * mm, "end": v(-155.17, 10.47) * mm});
            skArc(sketch, "E1701", {"start": v(-154.8, 9.42) * mm, "mid": v(-154.93, 9.1) * mm, "end": v(-155.07, 8.76) * mm});
            skArc(sketch, "E1702", {"start": v(-156.08, 8.28) * mm, "mid": v(-155.47, 8.32) * mm, "end": v(-155.07, 8.76) * mm});
            skLineSegment(sketch, "E1703", {"start": v(-156.08, 8.28) * mm, "end": v(-156.63, 8.46) * mm});
            skLineSegment(sketch, "E1704", {"start": v(-156.63, 8.46) * mm, "end": v(-156.85, 8.52) * mm});
            skLineSegment(sketch, "E1705", {"start": v(-156.85, 8.52) * mm, "end": v(-157, 8.55) * mm});
            skLineSegment(sketch, "E1706", {"start": v(-157, 8.55) * mm, "end": v(-157.18, 8.57) * mm});
            skLineSegment(sketch, "E1707", {"start": v(-157.18, 8.57) * mm, "end": v(-157.39, 8.58) * mm});
            skLineSegment(sketch, "E1708", {"start": v(-157.39, 8.58) * mm, "end": v(-157.61, 8.58) * mm});
            skLineSegment(sketch, "E1709", {"start": v(-157.61, 8.58) * mm, "end": v(-157.86, 8.57) * mm});
            skLineSegment(sketch, "E1710", {"start": v(-157.86, 8.57) * mm, "end": v(-158.12, 8.54) * mm});
            skArc(sketch, "E1711", {"start": v(-157.79, -5.51) * mm, "mid": v(-157.43, -6.07) * mm, "end": v(-157.05, -6.62) * mm});
            skLineSegment(sketch, "E1712", {"start": v(-141.23, -10.9) * mm, "end": v(-141.2, -11.12) * mm});
            skLineSegment(sketch, "E1713", {"start": v(-153.37, -5.3) * mm, "end": v(-153.82, -5.68) * mm});
            skLineSegment(sketch, "E1714", {"start": v(-141.2, -11.12) * mm, "end": v(-141.17, -11.27) * mm});
            skLineSegment(sketch, "E1715", {"start": v(-153.82, -5.68) * mm, "end": v(-154, -5.82) * mm});
            skLineSegment(sketch, "E1716", {"start": v(-141.17, -11.27) * mm, "end": v(-141.12, -11.44) * mm});
            skLineSegment(sketch, "E1717", {"start": v(-154, -5.82) * mm, "end": v(-154.12, -5.9) * mm});
            skLineSegment(sketch, "E1718", {"start": v(-141.12, -11.44) * mm, "end": v(-141.05, -11.64) * mm});
            skLineSegment(sketch, "E1719", {"start": v(-154.12, -5.9) * mm, "end": v(-154.28, -6) * mm});
            skLineSegment(sketch, "E1720", {"start": v(-141.05, -11.64) * mm, "end": v(-140.96, -11.85) * mm});
            skLineSegment(sketch, "E1721", {"start": v(-154.28, -6) * mm, "end": v(-154.47, -6.08) * mm});
            skLineSegment(sketch, "E1722", {"start": v(-140.96, -11.85) * mm, "end": v(-140.86, -12.08) * mm});
            skLineSegment(sketch, "E1723", {"start": v(-154.47, -6.08) * mm, "end": v(-154.68, -6.17) * mm});
            skLineSegment(sketch, "E1724", {"start": v(-140.86, -12.08) * mm, "end": v(-140.73, -12.3) * mm});
            skLineSegment(sketch, "E1725", {"start": v(-154.68, -6.17) * mm, "end": v(-154.91, -6.25) * mm});
            skLineSegment(sketch, "E1726", {"start": v(-140.73, -12.3) * mm, "end": v(-140.25, -13.07) * mm});
            skLineSegment(sketch, "E1727", {"start": v(-154.91, -6.25) * mm, "end": v(-155.16, -6.33) * mm});
            skLineSegment(sketch, "E1728", {"start": v(-140.25, -13.07) * mm, "end": v(-139.6, -13.85) * mm});
            skLineSegment(sketch, "E1729", {"start": v(-155.16, -6.33) * mm, "end": v(-156.05, -6.52) * mm});
            skArc(sketch, "E1730", {"start": v(-139.6, -13.85) * mm, "mid": v(-138.95, -13.73) * mm, "end": v(-138.3, -13.59) * mm});
            skLineSegment(sketch, "E1731", {"start": v(-156.05, -6.52) * mm, "end": v(-157.05, -6.62) * mm});
            skLineSegment(sketch, "E1732", {"start": v(-138.1, -9.69) * mm, "end": v(-137.93, -10.24) * mm});
            skArc(sketch, "E1733", {"start": v(-152.26, -5.37) * mm, "mid": v(-152.8, -5.11) * mm, "end": v(-153.37, -5.3) * mm});
            skLineSegment(sketch, "E1734", {"start": v(-137.93, -10.24) * mm, "end": v(-137.87, -10.46) * mm});
            skArc(sketch, "E1735", {"start": v(-152.26, -5.37) * mm, "mid": v(-152, -5.62) * mm, "end": v(-151.76, -5.87) * mm});
            skLineSegment(sketch, "E1736", {"start": v(-137.87, -10.46) * mm, "end": v(-137.84, -10.6) * mm});
            skLineSegment(sketch, "E1737", {"start": v(-137.84, -10.6) * mm, "end": v(-137.82, -10.79) * mm});
            skLineSegment(sketch, "E1738", {"start": v(-137.82, -10.79) * mm, "end": v(-137.81, -11) * mm});
            skLineSegment(sketch, "E1739", {"start": v(-137.81, -11) * mm, "end": v(-137.81, -11.23) * mm});
            skLineSegment(sketch, "E1740", {"start": v(-137.81, -11.23) * mm, "end": v(-137.82, -11.47) * mm});
            skLineSegment(sketch, "E1741", {"start": v(-137.82, -11.47) * mm, "end": v(-137.85, -11.73) * mm});
            skLineSegment(sketch, "E1742", {"start": v(-137.85, -11.73) * mm, "end": v(-138, -12.62) * mm});
            skLineSegment(sketch, "E1743", {"start": v(-138, -12.62) * mm, "end": v(-138.3, -13.59) * mm});
            skArc(sketch, "E1744", {"start": v(-137.62, -8.68) * mm, "mid": v(-138.07, -9.09) * mm, "end": v(-138.1, -9.69) * mm});
            skArc(sketch, "E1745", {"start": v(-137.62, -8.68) * mm, "mid": v(-137.3, -8.55) * mm, "end": v(-136.97, -8.4) * mm});
            skArc(sketch, "E1746", {"start": v(-135.92, -8.78) * mm, "mid": v(-136.37, -8.38) * mm, "end": v(-136.97, -8.4) * mm});
            skArc(sketch, "E1747", {"start": v(-144.97, 2.48) * mm, "mid": v(-144.51, 1.88) * mm, "end": v(-143.91, 1.41) * mm});
            skLineSegment(sketch, "E1748", {"start": v(-135.92, -8.78) * mm, "end": v(-135.65, -9.3) * mm});
            skArc(sketch, "E1749", {"start": v(-133.02, -11.4) * mm, "mid": v(-132.46, -11.04) * mm, "end": v(-131.92, -10.66) * mm});
            skLineSegment(sketch, "E1750", {"start": v(-133.91, -10.93) * mm, "end": v(-133.02, -11.4) * mm});
            skLineSegment(sketch, "E1751", {"start": v(-134.65, -10.4) * mm, "end": v(-133.91, -10.93) * mm});
            skLineSegment(sketch, "E1752", {"start": v(-134.85, -10.24) * mm, "end": v(-134.65, -10.4) * mm});
            skLineSegment(sketch, "E1753", {"start": v(-135.04, -10.08) * mm, "end": v(-134.85, -10.24) * mm});
            skLineSegment(sketch, "E1754", {"start": v(-135.2, -9.91) * mm, "end": v(-135.04, -10.08) * mm});
            skLineSegment(sketch, "E1755", {"start": v(-135.34, -9.76) * mm, "end": v(-135.2, -9.91) * mm});
            skLineSegment(sketch, "E1756", {"start": v(-135.45, -9.62) * mm, "end": v(-135.34, -9.76) * mm});
            skLineSegment(sketch, "E1757", {"start": v(-135.54, -9.5) * mm, "end": v(-135.45, -9.62) * mm});
            skLineSegment(sketch, "E1758", {"start": v(-135.65, -9.3) * mm, "end": v(-135.54, -9.5) * mm});
            skLineSegment(sketch, "E1759", {"start": v(-157.31, -4.63) * mm, "end": v(-157.79, -5.51) * mm});
            skLineSegment(sketch, "E1760", {"start": v(-141.28, -10.32) * mm, "end": v(-141.23, -10.9) * mm});
            skLineSegment(sketch, "E1761", {"start": v(-156.8, -3.88) * mm, "end": v(-157.31, -4.63) * mm});
            skArc(sketch, "E1762", {"start": v(-141.28, -10.32) * mm, "mid": v(-141.54, -9.78) * mm, "end": v(-142.1, -9.57) * mm});
            skLineSegment(sketch, "E1763", {"start": v(-156.63, -3.68) * mm, "end": v(-156.8, -3.88) * mm});
            skArc(sketch, "E1764", {"start": v(-142.82, -9.57) * mm, "mid": v(-142.46, -9.57) * mm, "end": v(-142.1, -9.57) * mm});
            skLineSegment(sketch, "E1765", {"start": v(-156.47, -3.5) * mm, "end": v(-156.63, -3.68) * mm});
            skArc(sketch, "E1766", {"start": v(-142.82, -9.57) * mm, "mid": v(-143.38, -9.78) * mm, "end": v(-143.65, -10.32) * mm});
            skLineSegment(sketch, "E1767", {"start": v(-156.3, -3.34) * mm, "end": v(-156.47, -3.5) * mm});
            skLineSegment(sketch, "E1768", {"start": v(-156.15, -3.2) * mm, "end": v(-156.3, -3.34) * mm});
            skLineSegment(sketch, "E1769", {"start": v(-156, -3.08) * mm, "end": v(-156.15, -3.2) * mm});
            skLineSegment(sketch, "E1770", {"start": v(-155.88, -3) * mm, "end": v(-156, -3.08) * mm});
            skLineSegment(sketch, "E1771", {"start": v(-155.68, -2.89) * mm, "end": v(-155.88, -3) * mm});
            skLineSegment(sketch, "E1772", {"start": v(-155.17, -2.62) * mm, "end": v(-155.68, -2.89) * mm});
            skArc(sketch, "E1773", {"start": v(-155.17, -2.62) * mm, "mid": v(-154.77, -2.17) * mm, "end": v(-154.8, -1.56) * mm});
            skArc(sketch, "E1774", {"start": v(-155.07, -0.91) * mm, "mid": v(-154.93, -1.24) * mm, "end": v(-154.8, -1.56) * mm});
            skArc(sketch, "E1775", {"start": v(-155.07, -0.91) * mm, "mid": v(-155.47, -0.47) * mm, "end": v(-156.08, -0.43) * mm});
            skLineSegment(sketch, "E1776", {"start": v(-159.01, -0.53) * mm, "end": v(-159.97, -0.24) * mm});
            skLineSegment(sketch, "E1777", {"start": v(-158.12, -0.69) * mm, "end": v(-159.01, -0.53) * mm});
            skLineSegment(sketch, "E1778", {"start": v(-157.86, -0.71) * mm, "end": v(-158.12, -0.69) * mm});
            skLineSegment(sketch, "E1779", {"start": v(-157.61, -0.72) * mm, "end": v(-157.86, -0.71) * mm});
            skLineSegment(sketch, "E1780", {"start": v(-157.39, -0.72) * mm, "end": v(-157.61, -0.72) * mm});
            skLineSegment(sketch, "E1781", {"start": v(-157.18, -0.71) * mm, "end": v(-157.39, -0.72) * mm});
            skLineSegment(sketch, "E1782", {"start": v(-157, -0.7) * mm, "end": v(-157.18, -0.71) * mm});
            skLineSegment(sketch, "E1783", {"start": v(-156.85, -0.67) * mm, "end": v(-157, -0.7) * mm});
            skLineSegment(sketch, "E1784", {"start": v(-156.63, -0.6) * mm, "end": v(-156.85, -0.67) * mm});
            skLineSegment(sketch, "E1785", {"start": v(-156.08, -0.43) * mm, "end": v(-156.63, -0.6) * mm});
            skArc(sketch, "E1786", {"start": v(-160.23, 1.07) * mm, "mid": v(-160.12, 0.41) * mm, "end": v(-159.97, -0.24) * mm});
            skLineSegment(sketch, "E1787", {"start": v(-159.46, 1.7) * mm, "end": v(-160.23, 1.07) * mm});
            skLineSegment(sketch, "E1788", {"start": v(-158.7, 2.2) * mm, "end": v(-159.46, 1.7) * mm});
            skLineSegment(sketch, "E1789", {"start": v(-144.68, -13.07) * mm, "end": v(-145.32, -13.85) * mm});
            skLineSegment(sketch, "E1790", {"start": v(-126.8, -0.69) * mm, "end": v(-125.91, -0.53) * mm});
            skLineSegment(sketch, "E1791", {"start": v(-144.2, -12.3) * mm, "end": v(-144.68, -13.07) * mm});
            skLineSegment(sketch, "E1792", {"start": v(-127.06, -0.71) * mm, "end": v(-126.8, -0.69) * mm});
            skLineSegment(sketch, "E1793", {"start": v(-144.07, -12.08) * mm, "end": v(-144.2, -12.3) * mm});
            skLineSegment(sketch, "E1794", {"start": v(-127.31, -0.72) * mm, "end": v(-127.06, -0.71) * mm});
            skLineSegment(sketch, "E1795", {"start": v(-143.96, -11.85) * mm, "end": v(-144.07, -12.08) * mm});
            skLineSegment(sketch, "E1796", {"start": v(-127.54, -0.72) * mm, "end": v(-127.31, -0.72) * mm});
            skLineSegment(sketch, "E1797", {"start": v(-130.01, -6.25) * mm, "end": v(-129.76, -6.33) * mm});
            skLineSegment(sketch, "E1798", {"start": v(-150.27, -10.4) * mm, "end": v(-151.01, -10.93) * mm});
            skLineSegment(sketch, "E1799", {"start": v(-157.83, 2.58) * mm, "end": v(-158.03, 2.51) * mm});
            skLineSegment(sketch, "E1800", {"start": v(-143.88, -11.64) * mm, "end": v(-143.96, -11.85) * mm});
            skLineSegment(sketch, "E1801", {"start": v(-127.75, -0.71) * mm, "end": v(-127.54, -0.72) * mm});
            skLineSegment(sketch, "E1802", {"start": v(-130.24, -6.17) * mm, "end": v(-130.01, -6.25) * mm});
            skLineSegment(sketch, "E1803", {"start": v(-150.07, -10.24) * mm, "end": v(-150.27, -10.4) * mm});
            skLineSegment(sketch, "E1804", {"start": v(-157.66, 2.63) * mm, "end": v(-157.83, 2.58) * mm});
            skLineSegment(sketch, "E1805", {"start": v(-143.8, -11.44) * mm, "end": v(-143.88, -11.64) * mm});
            skLineSegment(sketch, "E1806", {"start": v(-127.93, -0.7) * mm, "end": v(-127.75, -0.71) * mm});
            skLineSegment(sketch, "E1807", {"start": v(-130.46, -6.08) * mm, "end": v(-130.24, -6.17) * mm});
            skLineSegment(sketch, "E1808", {"start": v(-149.89, -10.08) * mm, "end": v(-150.07, -10.24) * mm});
            skLineSegment(sketch, "E1809", {"start": v(-157.51, 2.67) * mm, "end": v(-157.66, 2.63) * mm});
            skLineSegment(sketch, "E1810", {"start": v(-143.75, -11.27) * mm, "end": v(-143.8, -11.44) * mm});
            skLineSegment(sketch, "E1811", {"start": v(-128.08, -0.67) * mm, "end": v(-127.93, -0.7) * mm});
            skLineSegment(sketch, "E1812", {"start": v(-130.64, -6) * mm, "end": v(-130.46, -6.08) * mm});
            skLineSegment(sketch, "E1813", {"start": v(-149.73, -9.91) * mm, "end": v(-149.89, -10.08) * mm});
            skLineSegment(sketch, "E1814", {"start": v(-157.28, 2.7) * mm, "end": v(-157.51, 2.67) * mm});
            skLineSegment(sketch, "E1815", {"start": v(-143.72, -11.12) * mm, "end": v(-143.75, -11.27) * mm});
            skLineSegment(sketch, "E1816", {"start": v(-128.3, -0.6) * mm, "end": v(-128.08, -0.67) * mm});
            skLineSegment(sketch, "E1817", {"start": v(-130.8, -5.9) * mm, "end": v(-130.64, -6) * mm});
            skLineSegment(sketch, "E1818", {"start": v(-149.59, -9.76) * mm, "end": v(-149.73, -9.91) * mm});
            skLineSegment(sketch, "E1819", {"start": v(-156.7, 2.74) * mm, "end": v(-157.28, 2.7) * mm});
            skLineSegment(sketch, "E1820", {"start": v(-143.7, -10.9) * mm, "end": v(-143.72, -11.12) * mm});
            skLineSegment(sketch, "E1821", {"start": v(-128.85, -0.43) * mm, "end": v(-128.3, -0.6) * mm});
            skLineSegment(sketch, "E1822", {"start": v(-130.93, -5.82) * mm, "end": v(-130.8, -5.9) * mm});
            skLineSegment(sketch, "E1823", {"start": v(-149.47, -9.62) * mm, "end": v(-149.59, -9.76) * mm});
            skArc(sketch, "E1824", {"start": v(-156.7, 2.74) * mm, "mid": v(-156.17, 3) * mm, "end": v(-155.96, 3.57) * mm});
            skLineSegment(sketch, "E1825", {"start": v(-143.65, -10.32) * mm, "end": v(-143.7, -10.9) * mm});
            skArc(sketch, "E1826", {"start": v(-128.85, -0.43) * mm, "mid": v(-129.45, -0.47) * mm, "end": v(-129.86, -0.91) * mm});
            skLineSegment(sketch, "E1827", {"start": v(-131.1, -5.68) * mm, "end": v(-130.93, -5.82) * mm});
            skLineSegment(sketch, "E1828", {"start": v(-149.39, -9.5) * mm, "end": v(-149.47, -9.62) * mm});
            skArc(sketch, "E1829", {"start": v(-155.96, 4.28) * mm, "mid": v(-155.96, 3.93) * mm, "end": v(-155.96, 3.57) * mm});
            skArc(sketch, "E1830", {"start": v(-146.62, -13.59) * mm, "mid": v(-145.97, -13.73) * mm, "end": v(-145.32, -13.85) * mm});
            skArc(sketch, "E1831", {"start": v(-130.13, -1.56) * mm, "mid": v(-130, -1.24) * mm, "end": v(-129.86, -0.91) * mm});
            skLineSegment(sketch, "E1832", {"start": v(-131.55, -5.3) * mm, "end": v(-131.1, -5.68) * mm});
            skLineSegment(sketch, "E1833", {"start": v(-149.28, -9.3) * mm, "end": v(-149.39, -9.5) * mm});
            skArc(sketch, "E1834", {"start": v(-155.96, 4.28) * mm, "mid": v(-156.17, 4.85) * mm, "end": v(-156.7, 5.11) * mm});
            skLineSegment(sketch, "E1835", {"start": v(-146.92, -12.62) * mm, "end": v(-146.62, -13.59) * mm});
            skArc(sketch, "E1836", {"start": v(-130.13, -1.56) * mm, "mid": v(-130.15, -2.17) * mm, "end": v(-129.76, -2.62) * mm});
            skArc(sketch, "E1837", {"start": v(-131.55, -5.3) * mm, "mid": v(-132.12, -5.11) * mm, "end": v(-132.67, -5.37) * mm});
            skLineSegment(sketch, "E1838", {"start": v(-149, -8.78) * mm, "end": v(-149.28, -9.3) * mm});
            skLineSegment(sketch, "E1839", {"start": v(-159.46, 6.14) * mm, "end": v(-160.23, 6.78) * mm});
            skLineSegment(sketch, "E1840", {"start": v(-147.08, -11.73) * mm, "end": v(-146.92, -12.62) * mm});
            skLineSegment(sketch, "E1841", {"start": v(-127.61, -4.63) * mm, "end": v(-127.14, -5.51) * mm});
            skArc(sketch, "E1842", {"start": v(-153, -10.66) * mm, "mid": v(-152.46, -11.04) * mm, "end": v(-151.9, -11.4) * mm});
            skLineSegment(sketch, "E1843", {"start": v(-158.7, 5.66) * mm, "end": v(-159.46, 6.14) * mm});
            skLineSegment(sketch, "E1844", {"start": v(-147.1, -11.47) * mm, "end": v(-147.08, -11.73) * mm});
            skLineSegment(sketch, "E1845", {"start": v(-128.13, -3.88) * mm, "end": v(-127.61, -4.63) * mm});
            skArc(sketch, "E1846", {"start": v(-133.17, -5.87) * mm, "mid": v(-132.92, -5.62) * mm, "end": v(-132.67, -5.37) * mm});
            skLineSegment(sketch, "E1847", {"start": v(-152.91, -9.66) * mm, "end": v(-153, -10.66) * mm});
            skLineSegment(sketch, "E1848", {"start": v(-158.46, 5.53) * mm, "end": v(-158.7, 5.66) * mm});
            skLineSegment(sketch, "E1849", {"start": v(-147.11, -11.23) * mm, "end": v(-147.1, -11.47) * mm});
            skLineSegment(sketch, "E1850", {"start": v(-128.3, -3.68) * mm, "end": v(-128.13, -3.88) * mm});
            skArc(sketch, "E1851", {"start": v(-133.17, -5.87) * mm, "mid": v(-133.42, -6.41) * mm, "end": v(-133.23, -6.98) * mm});
            skLineSegment(sketch, "E1852", {"start": v(-152.72, -8.77) * mm, "end": v(-152.91, -9.66) * mm});
            skLineSegment(sketch, "E1853", {"start": v(-158.24, 5.43) * mm, "end": v(-158.46, 5.53) * mm});
            skLineSegment(sketch, "E1854", {"start": v(-147.11, -11) * mm, "end": v(-147.11, -11.23) * mm});
            skLineSegment(sketch, "E1855", {"start": v(-128.46, -3.5) * mm, "end": v(-128.3, -3.68) * mm});
            skLineSegment(sketch, "E1856", {"start": v(-132.01, -9.66) * mm, "end": v(-131.92, -10.66) * mm});
            skLineSegment(sketch, "E1857", {"start": v(-152.64, -8.52) * mm, "end": v(-152.72, -8.77) * mm});
            skLineSegment(sketch, "E1858", {"start": v(-158.03, 5.34) * mm, "end": v(-158.24, 5.43) * mm});
            skLineSegment(sketch, "E1859", {"start": v(-147.1, -10.79) * mm, "end": v(-147.11, -11) * mm});
            skLineSegment(sketch, "E1860", {"start": v(-128.62, -3.34) * mm, "end": v(-128.46, -3.5) * mm});
            skLineSegment(sketch, "E1861", {"start": v(-152.47, 15.93) * mm, "end": v(-152.56, 16.15) * mm});
            skLineSegment(sketch, "E1862", {"start": v(-132.2, -8.77) * mm, "end": v(-132.01, -9.66) * mm});
            skLineSegment(sketch, "E1863", {"start": v(-152.56, -8.3) * mm, "end": v(-152.64, -8.52) * mm});
            skLineSegment(sketch, "E1864", {"start": v(-157.83, 5.27) * mm, "end": v(-158.03, 5.34) * mm});
            skLineSegment(sketch, "E1865", {"start": v(-147.08, -10.6) * mm, "end": v(-147.1, -10.79) * mm});
            skLineSegment(sketch, "E1866", {"start": v(-128.78, -3.2) * mm, "end": v(-128.62, -3.34) * mm});
            skLineSegment(sketch, "E1867", {"start": v(-152.38, 15.74) * mm, "end": v(-152.47, 15.93) * mm});
            skLineSegment(sketch, "E1868", {"start": v(-132.28, -8.52) * mm, "end": v(-132.2, -8.77) * mm});
            skLineSegment(sketch, "E1869", {"start": v(-152.47, -8.08) * mm, "end": v(-152.56, -8.3) * mm});
            skLineSegment(sketch, "E1870", {"start": v(-157.66, 5.22) * mm, "end": v(-157.83, 5.27) * mm});
            skLineSegment(sketch, "E1871", {"start": v(-147.06, -10.46) * mm, "end": v(-147.08, -10.6) * mm});
            skLineSegment(sketch, "E1872", {"start": v(-128.92, -3.08) * mm, "end": v(-128.78, -3.2) * mm});
            skLineSegment(sketch, "E1873", {"start": v(-152.3, 15.58) * mm, "end": v(-152.38, 15.74) * mm});
            skLineSegment(sketch, "E1874", {"start": v(-132.37, -8.3) * mm, "end": v(-132.28, -8.52) * mm});
            skLineSegment(sketch, "E1875", {"start": v(-152.38, -7.9) * mm, "end": v(-152.47, -8.08) * mm});
            skLineSegment(sketch, "E1876", {"start": v(-157.51, 5.19) * mm, "end": v(-157.66, 5.22) * mm});
            skLineSegment(sketch, "E1877", {"start": v(-147, -10.24) * mm, "end": v(-147.06, -10.46) * mm});
            skLineSegment(sketch, "E1878", {"start": v(-129.04, -3) * mm, "end": v(-128.92, -3.08) * mm});
            skLineSegment(sketch, "E1879", {"start": v(-132.45, -8.08) * mm, "end": v(-132.37, -8.3) * mm});
            skLineSegment(sketch, "E1880", {"start": v(-152.3, -7.73) * mm, "end": v(-152.38, -7.9) * mm});
            skLineSegment(sketch, "E1881", {"start": v(-157.28, 5.16) * mm, "end": v(-157.51, 5.19) * mm});
            skLineSegment(sketch, "E1882", {"start": v(-146.82, -9.69) * mm, "end": v(-147, -10.24) * mm});
            skLineSegment(sketch, "E1883", {"start": v(-129.24, -2.89) * mm, "end": v(-129.04, -3) * mm});
            skLineSegment(sketch, "E1884", {"start": v(-132.55, -7.9) * mm, "end": v(-132.45, -8.08) * mm});
            skLineSegment(sketch, "E1885", {"start": v(-152.21, -7.6) * mm, "end": v(-152.3, -7.73) * mm});
            skLineSegment(sketch, "E1886", {"start": v(-156.7, 5.11) * mm, "end": v(-157.28, 5.16) * mm});
            skArc(sketch, "E1887", {"start": v(-146.82, -9.69) * mm, "mid": v(-146.86, -9.09) * mm, "end": v(-147.3, -8.68) * mm});
            skLineSegment(sketch, "E1888", {"start": v(-129.76, -2.62) * mm, "end": v(-129.24, -2.89) * mm});
            skLineSegment(sketch, "E1889", {"start": v(-132.63, -7.73) * mm, "end": v(-132.55, -7.9) * mm});
            skLineSegment(sketch, "E1890", {"start": v(-152.07, -7.43) * mm, "end": v(-152.21, -7.6) * mm});
            skArc(sketch, "E1891", {"start": v(-159.97, 8.09) * mm, "mid": v(-160.12, 7.44) * mm, "end": v(-160.23, 6.78) * mm});
            skArc(sketch, "E1892", {"start": v(-147.95, -8.4) * mm, "mid": v(-147.63, -8.55) * mm, "end": v(-147.3, -8.68) * mm});
            skArc(sketch, "E1893", {"start": v(-127.88, -6.62) * mm, "mid": v(-127.5, -6.07) * mm, "end": v(-127.14, -5.51) * mm});
            skLineSegment(sketch, "E1894", {"start": v(-132.71, -7.6) * mm, "end": v(-132.63, -7.73) * mm});
            skLineSegment(sketch, "E1895", {"start": v(-151.7, -6.98) * mm, "end": v(-152.07, -7.43) * mm});
            skLineSegment(sketch, "E1896", {"start": v(-159.01, 8.38) * mm, "end": v(-159.97, 8.09) * mm});
            skArc(sketch, "E1897", {"start": v(-147.95, -8.4) * mm, "mid": v(-148.56, -8.38) * mm, "end": v(-149, -8.78) * mm});
            skLineSegment(sketch, "E1898", {"start": v(-128.88, -6.52) * mm, "end": v(-127.88, -6.62) * mm});
            skLineSegment(sketch, "E1899", {"start": v(-132.86, -7.43) * mm, "end": v(-132.71, -7.6) * mm});
            skArc(sketch, "E1900", {"start": v(-151.7, -6.98) * mm, "mid": v(-151.5, -6.41) * mm, "end": v(-151.76, -5.87) * mm});
            skLineSegment(sketch, "E1901", {"start": v(-158.12, 8.54) * mm, "end": v(-159.01, 8.38) * mm});
            skLineSegment(sketch, "E1902", {"start": v(-151.01, -10.93) * mm, "end": v(-151.9, -11.4) * mm});
            skLineSegment(sketch, "E1903", {"start": v(-129.76, -6.33) * mm, "end": v(-128.88, -6.52) * mm});
            skLineSegment(sketch, "E1904", {"start": v(-133.23, -6.98) * mm, "end": v(-132.86, -7.43) * mm});
            skLineSegment(sketch, "E1905", {"start": v(-158.46, 2.32) * mm, "end": v(-158.7, 2.2) * mm});
            skLineSegment(sketch, "E1906", {"start": v(-158.24, 2.42) * mm, "end": v(-158.46, 2.32) * mm});
            skLineSegment(sketch, "E1907", {"start": v(-158.03, 2.51) * mm, "end": v(-158.24, 2.42) * mm});
            skLineSegment(sketch, "E1908", {"start": v(-142.46, 1.03) * mm, "end": v(-142.46, 0.83) * mm});
            skLineSegment(sketch, "E1909", {"start": v(-141.01, 1.41) * mm, "end": v(-140.91, 1.24) * mm});
            skLineSegment(sketch, "E1910", {"start": v(-139.95, 2.48) * mm, "end": v(-139.78, 2.38) * mm});
            skLineSegment(sketch, "E1911", {"start": v(-139.56, 3.93) * mm, "end": v(-139.36, 3.93) * mm});
            skLineSegment(sketch, "E1912", {"start": v(-139.95, 5.38) * mm, "end": v(-139.78, 5.48) * mm});
            skLineSegment(sketch, "E1913", {"start": v(-141.01, 6.44) * mm, "end": v(-140.91, 6.61) * mm});
            skArc(sketch, "E1914", {"start": v(-139.95, 5.38) * mm, "mid": v(-140.41, 5.98) * mm, "end": v(-141.01, 6.44) * mm});
            skArc(sketch, "E1915", {"start": v(-139.36, 3.93) * mm, "mid": v(-139.47, 4.73) * mm, "end": v(-139.78, 5.48) * mm});
            skArc(sketch, "E1916", {"start": v(-139.95, 2.48) * mm, "mid": v(-139.66, 3.18) * mm, "end": v(-139.56, 3.93) * mm});
            skArc(sketch, "E1917", {"start": v(-140.91, 1.24) * mm, "mid": v(-140.27, 1.73) * mm, "end": v(-139.78, 2.38) * mm});
            skArc(sketch, "E1918", {"start": v(-142.46, 1.03) * mm, "mid": v(-141.71, 1.13) * mm, "end": v(-141.01, 1.41) * mm});
            skArc(sketch, "E1919", {"start": v(-144.01, 1.24) * mm, "mid": v(-143.26, 0.93) * mm, "end": v(-142.46, 0.83) * mm});
            skArc(sketch, "E1920", {"start": v(-145.56, 3.93) * mm, "mid": v(-145.46, 3.12) * mm, "end": v(-145.15, 2.38) * mm});
            skArc(sketch, "E1921", {"start": v(-144.01, 6.61) * mm, "mid": v(-144.65, 6.12) * mm, "end": v(-145.15, 5.48) * mm});
            skArc(sketch, "E1922", {"start": v(-144.97, 5.38) * mm, "mid": v(-145.26, 4.68) * mm, "end": v(-145.36, 3.93) * mm});
            skArc(sketch, "E1923", {"start": v(-140.91, 6.61) * mm, "mid": v(-141.66, 6.92) * mm, "end": v(-142.46, 7.03) * mm});
            skArc(sketch, "E1924", {"start": v(-142.46, 6.83) * mm, "mid": v(-143.21, 6.73) * mm, "end": v(-143.91, 6.44) * mm});
            skLineSegment(sketch, "E1925", {"start": v(-142.46, 6.83) * mm, "end": v(-142.46, 7.03) * mm});
            skLineSegment(sketch, "E1926", {"start": v(-143.91, 6.44) * mm, "end": v(-144.01, 6.61) * mm});
            skLineSegment(sketch, "E1927", {"start": v(-144.97, 5.38) * mm, "end": v(-145.15, 5.48) * mm});
            skLineSegment(sketch, "E1928", {"start": v(-145.36, 3.93) * mm, "end": v(-145.56, 3.93) * mm});
            skLineSegment(sketch, "E1929", {"start": v(-144.97, 2.48) * mm, "end": v(-145.15, 2.38) * mm});
            skLineSegment(sketch, "E1930", {"start": v(-143.91, 1.41) * mm, "end": v(-144.01, 1.24) * mm});
            skLineSegment(sketch, "E1931.bottom", {"start": v(22.7, -60.62) * mm, "end": v(56.96, -60.62) * mm});
            skLineSegment(sketch, "E1931.top", {"start": v(22.7, -72.62) * mm, "end": v(56.96, -72.62) * mm});
            skLineSegment(sketch, "E1931.left", {"start": v(16.7, -66.62) * mm, "end": v(16.7, -66.62) * mm});
            skLineSegment(sketch, "E1931.right", {"start": v(59.96, -63.62) * mm, "end": v(59.96, -69.62) * mm});
            skArc(sketch, "E1932", {"start": v(53.4, -69.3) * mm, "mid": v(54.16, -69.62) * mm, "end": v(54.96, -69.72) * mm});
            skArc(sketch, "E1933", {"start": v(21.16, -63.94) * mm, "mid": v(20.52, -64.43) * mm, "end": v(20.02, -65.07) * mm});
            skPoint(sketch, "E1933.centerSnap0", {"position": v(16.7, -66.62) * mm});
            skPoint(sketch, "E1934.visualSharp", {"position": v(16.7, -60.62) * mm});
            skArc(sketch, "E1934.filletArc", {"start": v(22.7, -60.62) * mm, "mid": v(18.47, -62.38) * mm, "end": v(16.7, -66.62) * mm});
            skPoint(sketch, "E1935.visualSharp", {"position": v(16.7, -72.62) * mm});
            skArc(sketch, "E1935.filletArc", {"start": v(16.7, -66.62) * mm, "mid": v(18.47, -70.87) * mm, "end": v(22.7, -72.62) * mm});
            skArc(sketch, "E1936", {"start": v(22.7, -63.72) * mm, "mid": v(21.96, -63.82) * mm, "end": v(21.26, -64.11) * mm});
            skArc(sketch, "E1937", {"start": v(54.96, -63.72) * mm, "mid": v(54.2, -63.82) * mm, "end": v(53.5, -64.11) * mm});
            skLineSegment(sketch, "E1938", {"start": v(22.7, -63.72) * mm, "end": v(22.7, -63.52) * mm});
            skLineSegment(sketch, "E1939.1.0", {"start": v(21.26, -64.11) * mm, "end": v(21.16, -63.94) * mm});
            skLineSegment(sketch, "E1939.2.0", {"start": v(20.2, -65.17) * mm, "end": v(20.02, -65.07) * mm});
            skLineSegment(sketch, "E1939.3.0", {"start": v(19.8, -66.62) * mm, "end": v(19.6, -66.62) * mm});
            skLineSegment(sketch, "E1939.4.0", {"start": v(20.2, -68.07) * mm, "end": v(20.02, -68.17) * mm});
            skLineSegment(sketch, "E1939.5.0", {"start": v(21.26, -69.13) * mm, "end": v(21.16, -69.3) * mm});
            skLineSegment(sketch, "E1939.6.0", {"start": v(22.7, -69.52) * mm, "end": v(22.7, -69.72) * mm});
            skLineSegment(sketch, "E1939.7.0", {"start": v(24.16, -69.13) * mm, "end": v(24.26, -69.3) * mm});
            skLineSegment(sketch, "E1939.8.0", {"start": v(25.22, -68.07) * mm, "end": v(25.4, -68.17) * mm});
            skLineSegment(sketch, "E1939.9.0", {"start": v(25.6, -66.62) * mm, "end": v(25.8, -66.62) * mm});
            skLineSegment(sketch, "E1939.10.0", {"start": v(25.22, -65.17) * mm, "end": v(25.4, -65.07) * mm});
            skLineSegment(sketch, "E1939.11.0", {"start": v(24.16, -64.11) * mm, "end": v(24.26, -63.94) * mm});
            skLineSegment(sketch, "E1940", {"start": v(54.96, -63.72) * mm, "end": v(54.96, -63.52) * mm});
            skLineSegment(sketch, "E1941.1.0", {"start": v(53.5, -64.11) * mm, "end": v(53.4, -63.94) * mm});
            skLineSegment(sketch, "E1941.2.0", {"start": v(52.45, -65.17) * mm, "end": v(52.27, -65.07) * mm});
            skLineSegment(sketch, "E1941.3.0", {"start": v(52.06, -66.62) * mm, "end": v(51.86, -66.62) * mm});
            skLineSegment(sketch, "E1941.4.0", {"start": v(52.45, -68.07) * mm, "end": v(52.27, -68.17) * mm});
            skLineSegment(sketch, "E1941.5.0", {"start": v(53.5, -69.13) * mm, "end": v(53.4, -69.3) * mm});
            skLineSegment(sketch, "E1941.6.0", {"start": v(54.96, -69.52) * mm, "end": v(54.96, -69.72) * mm});
            skLineSegment(sketch, "E1941.7.0", {"start": v(56.4, -69.13) * mm, "end": v(56.5, -69.3) * mm});
            skLineSegment(sketch, "E1941.8.0", {"start": v(57.47, -68.07) * mm, "end": v(57.64, -68.17) * mm});
            skLineSegment(sketch, "E1941.9.0", {"start": v(57.86, -66.62) * mm, "end": v(58.06, -66.62) * mm});
            skLineSegment(sketch, "E1941.10.0", {"start": v(57.47, -65.17) * mm, "end": v(57.64, -65.07) * mm});
            skLineSegment(sketch, "E1941.11.0", {"start": v(56.4, -64.11) * mm, "end": v(56.5, -63.94) * mm});
            skArc(sketch, "E1942.trimOffspring", {"start": v(25.22, -65.17) * mm, "mid": v(24.76, -64.57) * mm, "end": v(24.16, -64.11) * mm});
            skArc(sketch, "E1943.trimOffspring", {"start": v(25.22, -68.07) * mm, "mid": v(25.5, -67.37) * mm, "end": v(25.6, -66.62) * mm});
            skArc(sketch, "E1944.trimOffspring", {"start": v(22.7, -69.52) * mm, "mid": v(23.46, -69.42) * mm, "end": v(24.16, -69.13) * mm});
            skArc(sketch, "E1945.trimOffspring", {"start": v(20.2, -68.07) * mm, "mid": v(20.66, -68.67) * mm, "end": v(21.26, -69.13) * mm});
            skArc(sketch, "E1946.trimOffspring", {"start": v(20.2, -65.17) * mm, "mid": v(19.9, -65.87) * mm, "end": v(19.8, -66.62) * mm});
            skArc(sketch, "E1947.trimOffspring", {"start": v(24.26, -63.94) * mm, "mid": v(23.51, -63.63) * mm, "end": v(22.7, -63.52) * mm});
            skArc(sketch, "E1948.trimOffspring", {"start": v(25.8, -66.62) * mm, "mid": v(25.7, -65.82) * mm, "end": v(25.4, -65.07) * mm});
            skArc(sketch, "E1949.trimOffspring", {"start": v(24.26, -69.3) * mm, "mid": v(24.9, -68.81) * mm, "end": v(25.4, -68.17) * mm});
            skArc(sketch, "E1950.trimOffspring", {"start": v(21.16, -69.3) * mm, "mid": v(21.9, -69.62) * mm, "end": v(22.7, -69.72) * mm});
            skArc(sketch, "E1951.trimOffspring", {"start": v(19.6, -66.62) * mm, "mid": v(19.71, -67.43) * mm, "end": v(20.02, -68.17) * mm});
            skArc(sketch, "E1952.trimOffspring", {"start": v(57.47, -65.17) * mm, "mid": v(57, -64.57) * mm, "end": v(56.4, -64.11) * mm});
            skArc(sketch, "E1953.trimOffspring", {"start": v(57.47, -68.07) * mm, "mid": v(57.76, -67.37) * mm, "end": v(57.86, -66.62) * mm});
            skArc(sketch, "E1954.trimOffspring", {"start": v(54.96, -69.52) * mm, "mid": v(55.7, -69.42) * mm, "end": v(56.4, -69.13) * mm});
            skArc(sketch, "E1955.trimOffspring", {"start": v(52.45, -68.07) * mm, "mid": v(52.9, -68.67) * mm, "end": v(53.5, -69.13) * mm});
            skArc(sketch, "E1956.trimOffspring", {"start": v(52.45, -65.17) * mm, "mid": v(52.16, -65.87) * mm, "end": v(52.06, -66.62) * mm});
            skArc(sketch, "E1957.trimOffspring", {"start": v(56.5, -69.3) * mm, "mid": v(57.15, -68.81) * mm, "end": v(57.64, -68.17) * mm});
            skArc(sketch, "E1958.trimOffspring", {"start": v(58.06, -66.62) * mm, "mid": v(57.95, -65.82) * mm, "end": v(57.64, -65.07) * mm});
            skArc(sketch, "E1959.trimOffspring", {"start": v(56.5, -63.94) * mm, "mid": v(55.76, -63.63) * mm, "end": v(54.96, -63.52) * mm});
            skArc(sketch, "E1960.trimOffspring", {"start": v(53.4, -63.94) * mm, "mid": v(52.77, -64.43) * mm, "end": v(52.27, -65.07) * mm});
            skArc(sketch, "E1961.trimOffspring", {"start": v(51.86, -66.62) * mm, "mid": v(51.96, -67.43) * mm, "end": v(52.27, -68.17) * mm});
            skLineSegment(sketch, "E1962.bottom", {"start": v(21.97, -88.93) * mm, "end": v(56.22, -88.93) * mm});
            skLineSegment(sketch, "E1962.top", {"start": v(21.97, -100.93) * mm, "end": v(56.22, -100.93) * mm});
            skLineSegment(sketch, "E1962.left", {"start": v(15.97, -94.93) * mm, "end": v(15.97, -94.93) * mm});
            skLineSegment(sketch, "E1962.right", {"start": v(59.22, -91.93) * mm, "end": v(59.22, -97.93) * mm});
            skArc(sketch, "E1963", {"start": v(52.67, -97.61) * mm, "mid": v(53.42, -97.92) * mm, "end": v(54.22, -98.03) * mm});
            skArc(sketch, "E1964", {"start": v(20.42, -92.24) * mm, "mid": v(19.78, -92.74) * mm, "end": v(19.28, -93.38) * mm});
            skPoint(sketch, "E1964.centerSnap0", {"position": v(15.97, -94.93) * mm});
            skPoint(sketch, "E1965.visualSharp", {"position": v(15.97, -88.93) * mm});
            skArc(sketch, "E1965.filletArc", {"start": v(21.97, -88.93) * mm, "mid": v(17.73, -90.68) * mm, "end": v(15.97, -94.93) * mm});
            skPoint(sketch, "E1966.visualSharp", {"position": v(15.97, -100.93) * mm});
            skArc(sketch, "E1966.filletArc", {"start": v(15.97, -94.93) * mm, "mid": v(17.73, -99.17) * mm, "end": v(21.97, -100.93) * mm});
            skArc(sketch, "E1967", {"start": v(21.97, -92.03) * mm, "mid": v(21.22, -92.13) * mm, "end": v(20.52, -92.42) * mm});
            skArc(sketch, "E1968", {"start": v(54.22, -92.03) * mm, "mid": v(53.47, -92.13) * mm, "end": v(52.77, -92.42) * mm});
            skLineSegment(sketch, "E1969", {"start": v(21.97, -92.03) * mm, "end": v(21.97, -91.83) * mm});
            skLineSegment(sketch, "E1970.1.0", {"start": v(20.52, -92.42) * mm, "end": v(20.42, -92.24) * mm});
            skLineSegment(sketch, "E1970.2.0", {"start": v(19.46, -93.48) * mm, "end": v(19.28, -93.38) * mm});
            skLineSegment(sketch, "E1970.3.0", {"start": v(19.07, -94.93) * mm, "end": v(18.87, -94.93) * mm});
            skLineSegment(sketch, "E1970.4.0", {"start": v(19.46, -96.38) * mm, "end": v(19.28, -96.48) * mm});
            skLineSegment(sketch, "E1970.5.0", {"start": v(20.52, -97.44) * mm, "end": v(20.42, -97.61) * mm});
            skLineSegment(sketch, "E1970.6.0", {"start": v(21.97, -97.83) * mm, "end": v(21.97, -98.03) * mm});
            skLineSegment(sketch, "E1970.7.0", {"start": v(23.42, -97.44) * mm, "end": v(23.52, -97.61) * mm});
            skLineSegment(sketch, "E1970.8.0", {"start": v(24.48, -96.38) * mm, "end": v(24.65, -96.48) * mm});
            skLineSegment(sketch, "E1970.9.0", {"start": v(24.87, -94.93) * mm, "end": v(25.07, -94.93) * mm});
            skLineSegment(sketch, "E1970.10.0", {"start": v(24.48, -93.48) * mm, "end": v(24.65, -93.38) * mm});
            skLineSegment(sketch, "E1970.11.0", {"start": v(23.42, -92.42) * mm, "end": v(23.52, -92.24) * mm});
            skLineSegment(sketch, "E1971", {"start": v(54.22, -92.03) * mm, "end": v(54.22, -91.83) * mm});
            skLineSegment(sketch, "E1972.1.0", {"start": v(52.77, -92.42) * mm, "end": v(52.67, -92.24) * mm});
            skLineSegment(sketch, "E1972.2.0", {"start": v(51.7, -93.48) * mm, "end": v(51.53, -93.38) * mm});
            skLineSegment(sketch, "E1972.3.0", {"start": v(51.32, -94.93) * mm, "end": v(51.12, -94.93) * mm});
            skLineSegment(sketch, "E1972.4.0", {"start": v(51.7, -96.38) * mm, "end": v(51.53, -96.48) * mm});
            skLineSegment(sketch, "E1972.5.0", {"start": v(52.77, -97.44) * mm, "end": v(52.67, -97.61) * mm});
            skLineSegment(sketch, "E1972.6.0", {"start": v(54.22, -97.83) * mm, "end": v(54.22, -98.03) * mm});
            skLineSegment(sketch, "E1972.7.0", {"start": v(55.67, -97.44) * mm, "end": v(55.77, -97.61) * mm});
            skLineSegment(sketch, "E1972.8.0", {"start": v(56.73, -96.38) * mm, "end": v(56.9, -96.48) * mm});
            skLineSegment(sketch, "E1972.9.0", {"start": v(57.12, -94.93) * mm, "end": v(57.32, -94.93) * mm});
            skLineSegment(sketch, "E1972.10.0", {"start": v(56.73, -93.48) * mm, "end": v(56.9, -93.38) * mm});
            skLineSegment(sketch, "E1972.11.0", {"start": v(55.67, -92.42) * mm, "end": v(55.77, -92.24) * mm});
            skArc(sketch, "E1973.trimOffspring", {"start": v(24.48, -93.48) * mm, "mid": v(24.02, -92.88) * mm, "end": v(23.42, -92.42) * mm});
            skArc(sketch, "E1974.trimOffspring", {"start": v(24.48, -96.38) * mm, "mid": v(24.77, -95.68) * mm, "end": v(24.87, -94.93) * mm});
            skArc(sketch, "E1975.trimOffspring", {"start": v(21.97, -97.83) * mm, "mid": v(22.72, -97.73) * mm, "end": v(23.42, -97.44) * mm});
            skArc(sketch, "E1976.trimOffspring", {"start": v(19.46, -96.38) * mm, "mid": v(19.92, -96.98) * mm, "end": v(20.52, -97.44) * mm});
            skArc(sketch, "E1977.trimOffspring", {"start": v(19.46, -93.48) * mm, "mid": v(19.17, -94.18) * mm, "end": v(19.07, -94.93) * mm});
            skArc(sketch, "E1978.trimOffspring", {"start": v(23.52, -92.24) * mm, "mid": v(22.77, -91.93) * mm, "end": v(21.97, -91.83) * mm});
            skArc(sketch, "E1979.trimOffspring", {"start": v(25.07, -94.93) * mm, "mid": v(24.96, -94.13) * mm, "end": v(24.65, -93.38) * mm});
            skArc(sketch, "E1980.trimOffspring", {"start": v(23.52, -97.61) * mm, "mid": v(24.16, -97.12) * mm, "end": v(24.65, -96.48) * mm});
            skArc(sketch, "E1981.trimOffspring", {"start": v(20.42, -97.61) * mm, "mid": v(21.17, -97.92) * mm, "end": v(21.97, -98.03) * mm});
            skArc(sketch, "E1982.trimOffspring", {"start": v(18.87, -94.93) * mm, "mid": v(18.98, -95.73) * mm, "end": v(19.28, -96.48) * mm});
            skArc(sketch, "E1983.trimOffspring", {"start": v(56.73, -93.48) * mm, "mid": v(56.27, -92.88) * mm, "end": v(55.67, -92.42) * mm});
            skArc(sketch, "E1984.trimOffspring", {"start": v(56.73, -96.38) * mm, "mid": v(57.02, -95.68) * mm, "end": v(57.12, -94.93) * mm});
            skArc(sketch, "E1985.trimOffspring", {"start": v(54.22, -97.83) * mm, "mid": v(54.97, -97.73) * mm, "end": v(55.67, -97.44) * mm});
            skArc(sketch, "E1986.trimOffspring", {"start": v(51.7, -96.38) * mm, "mid": v(52.17, -96.98) * mm, "end": v(52.77, -97.44) * mm});
            skArc(sketch, "E1987.trimOffspring", {"start": v(51.7, -93.48) * mm, "mid": v(51.42, -94.18) * mm, "end": v(51.32, -94.93) * mm});
            skArc(sketch, "E1988.trimOffspring", {"start": v(55.77, -97.61) * mm, "mid": v(56.41, -97.12) * mm, "end": v(56.9, -96.48) * mm});
            skArc(sketch, "E1989.trimOffspring", {"start": v(57.32, -94.93) * mm, "mid": v(57.21, -94.13) * mm, "end": v(56.9, -93.38) * mm});
            skArc(sketch, "E1990.trimOffspring", {"start": v(55.77, -92.24) * mm, "mid": v(55.02, -91.93) * mm, "end": v(54.22, -91.83) * mm});
            skArc(sketch, "E1991.trimOffspring", {"start": v(52.67, -92.24) * mm, "mid": v(52.03, -92.74) * mm, "end": v(51.53, -93.38) * mm});
            skArc(sketch, "E1992.trimOffspring", {"start": v(51.12, -94.93) * mm, "mid": v(51.23, -95.73) * mm, "end": v(51.53, -96.48) * mm});
            skArc(sketch, "E1993", {"start": v(-33.58, 14.86) * mm, "mid": v(-33.83, 14.61) * mm, "end": v(-34.08, 14.36) * mm});
            skLineSegment(sketch, "E1994", {"start": v(-25.63, 20.44) * mm, "end": v(-25.7, 20.63) * mm});
            skLineSegment(sketch, "E1995", {"start": v(-38.67, 0.47) * mm, "end": v(-38.81, 0.45) * mm});
            skLineSegment(sketch, "E1996", {"start": v(-23.05, -9.76) * mm, "end": v(-23.02, -9.98) * mm});
            skLineSegment(sketch, "E1997", {"start": v(-9.23, 3.8) * mm, "end": v(-9.09, 3.78) * mm});
            skArc(sketch, "E1998", {"start": v(-35.2, 14.3) * mm, "mid": v(-34.62, 14.1) * mm, "end": v(-34.08, 14.36) * mm});
            skLineSegment(sketch, "E1999", {"start": v(-25.7, 20.63) * mm, "end": v(-25.78, 20.85) * mm});
            skLineSegment(sketch, "E2000", {"start": v(-38.81, 0.45) * mm, "end": v(-39, 0.43) * mm});
            skLineSegment(sketch, "E2001", {"start": v(-23.02, -9.98) * mm, "end": v(-23, -10.13) * mm});
            skLineSegment(sketch, "E2002", {"start": v(-9.09, 3.78) * mm, "end": v(-8.91, 3.72) * mm});
            skLineSegment(sketch, "E2003", {"start": v(-35.2, 14.3) * mm, "end": v(-35.64, 14.67) * mm});
            skLineSegment(sketch, "E2004", {"start": v(-25.78, 20.85) * mm, "end": v(-25.89, 21.07) * mm});
            skLineSegment(sketch, "E2005", {"start": v(-39, 0.43) * mm, "end": v(-39.2, 0.42) * mm});
            skLineSegment(sketch, "E2006", {"start": v(-23, -10.13) * mm, "end": v(-22.94, -10.3) * mm});
            skLineSegment(sketch, "E2007", {"start": v(-8.91, 3.72) * mm, "end": v(-8.72, 3.65) * mm});
            skLineSegment(sketch, "E2008", {"start": v(-35.64, 14.67) * mm, "end": v(-35.82, 14.82) * mm});
            skLineSegment(sketch, "E2009", {"start": v(-25.89, 21.07) * mm, "end": v(-26.01, 21.3) * mm});
            skLineSegment(sketch, "E2010", {"start": v(-39.2, 0.42) * mm, "end": v(-39.44, 0.42) * mm});
            skLineSegment(sketch, "E2011", {"start": v(-22.94, -10.3) * mm, "end": v(-22.87, -10.5) * mm});
            skLineSegment(sketch, "E2012", {"start": v(-8.72, 3.65) * mm, "end": v(-8.5, 3.57) * mm});
            skLineSegment(sketch, "E2013", {"start": v(-35.82, 14.82) * mm, "end": v(-35.94, 14.9) * mm});
            skLineSegment(sketch, "E2014", {"start": v(-26.01, 21.3) * mm, "end": v(-26.5, 22.06) * mm});
            skLineSegment(sketch, "E2015", {"start": v(-39.44, 0.42) * mm, "end": v(-39.68, 0.43) * mm});
            skLineSegment(sketch, "E2016", {"start": v(-22.87, -10.5) * mm, "end": v(-22.78, -10.71) * mm});
            skLineSegment(sketch, "E2017", {"start": v(-8.5, 3.57) * mm, "end": v(-8.28, 3.46) * mm});
            skLineSegment(sketch, "E2018", {"start": v(-35.94, 14.9) * mm, "end": v(-36.1, 14.98) * mm});
            skLineSegment(sketch, "E2019", {"start": v(-26.5, 22.06) * mm, "end": v(-27.14, 22.84) * mm});
            skLineSegment(sketch, "E2020", {"start": v(-39.68, 0.43) * mm, "end": v(-39.94, 0.45) * mm});
            skLineSegment(sketch, "E2021", {"start": v(-22.78, -10.71) * mm, "end": v(-22.68, -10.93) * mm});
            skLineSegment(sketch, "E2022", {"start": v(-8.28, 3.46) * mm, "end": v(-8.05, 3.34) * mm});
            skLineSegment(sketch, "E2023", {"start": v(-36.1, 14.98) * mm, "end": v(-36.3, 15.07) * mm});
            skArc(sketch, "E2024", {"start": v(-27.14, 22.84) * mm, "mid": v(-27.8, 22.72) * mm, "end": v(-28.44, 22.58) * mm});
            skLineSegment(sketch, "E2025", {"start": v(-39.94, 0.45) * mm, "end": v(-40.83, 0.61) * mm});
            skLineSegment(sketch, "E2026", {"start": v(-22.68, -10.93) * mm, "end": v(-22.55, -11.17) * mm});
            skLineSegment(sketch, "E2027", {"start": v(-8.05, 3.34) * mm, "end": v(-7.29, 2.85) * mm});
            skLineSegment(sketch, "E2028", {"start": v(-36.3, 15.07) * mm, "end": v(-36.5, 15.16) * mm});
            skLineSegment(sketch, "E2029", {"start": v(-28.64, 18.68) * mm, "end": v(-28.81, 19.23) * mm});
            skLineSegment(sketch, "E2030", {"start": v(-40.83, 0.61) * mm, "end": v(-41.8, 0.9) * mm});
            skLineSegment(sketch, "E2031", {"start": v(-22.55, -11.17) * mm, "end": v(-22.07, -11.93) * mm});
            skLineSegment(sketch, "E2032", {"start": v(-7.29, 2.85) * mm, "end": v(-6.51, 2.21) * mm});
            skLineSegment(sketch, "E2033", {"start": v(-36.5, 15.16) * mm, "end": v(-36.73, 15.25) * mm});
            skLineSegment(sketch, "E2034", {"start": v(-28.81, 19.23) * mm, "end": v(-28.88, 19.45) * mm});
            skArc(sketch, "E2035", {"start": v(-36.89, 0.23) * mm, "mid": v(-37.3, 0.67) * mm, "end": v(-37.9, 0.71) * mm});
            skLineSegment(sketch, "E2036", {"start": v(-22.07, -11.93) * mm, "end": v(-21.43, -12.7) * mm});
            skArc(sketch, "E2037", {"start": v(-10.79, 4.71) * mm, "mid": v(-10.58, 4.15) * mm, "end": v(-10.04, 3.88) * mm});
            skLineSegment(sketch, "E2038", {"start": v(-36.73, 15.25) * mm, "end": v(-36.98, 15.32) * mm});
            skLineSegment(sketch, "E2039", {"start": v(-28.88, 19.45) * mm, "end": v(-28.9, 19.6) * mm});
            skArc(sketch, "E2040", {"start": v(-36.89, 0.23) * mm, "mid": v(-36.76, -0.1) * mm, "end": v(-36.62, -0.42) * mm});
            skArc(sketch, "E2041", {"start": v(-21.43, -12.7) * mm, "mid": v(-20.77, -12.59) * mm, "end": v(-20.12, -12.45) * mm});
            skArc(sketch, "E2042", {"start": v(-10.79, 4.71) * mm, "mid": v(-10.78, 5.07) * mm, "end": v(-10.79, 5.42) * mm});
            skLineSegment(sketch, "E2043", {"start": v(-36.98, 15.32) * mm, "end": v(-37.87, 15.52) * mm});
            skLineSegment(sketch, "E2044", {"start": v(-28.9, 19.6) * mm, "end": v(-28.92, 19.78) * mm});
            skArc(sketch, "E2045", {"start": v(-36.99, -1.48) * mm, "mid": v(-36.6, -1.03) * mm, "end": v(-36.62, -0.42) * mm});
            skLineSegment(sketch, "E2046", {"start": v(-19.93, -8.55) * mm, "end": v(-19.75, -9.1) * mm});
            skArc(sketch, "E2047", {"start": v(-10.04, 6.25) * mm, "mid": v(-10.58, 5.99) * mm, "end": v(-10.79, 5.42) * mm});
            skLineSegment(sketch, "E2048", {"start": v(-37.87, 15.52) * mm, "end": v(-38.87, 15.61) * mm});
            skLineSegment(sketch, "E2049", {"start": v(-28.92, 19.78) * mm, "end": v(-28.93, 20) * mm});
            skLineSegment(sketch, "E2050", {"start": v(-36.99, -1.48) * mm, "end": v(-37.5, -1.75) * mm});
            skLineSegment(sketch, "E2051", {"start": v(-19.75, -9.1) * mm, "end": v(-19.69, -9.32) * mm});
            skLineSegment(sketch, "E2052", {"start": v(-10.04, 6.25) * mm, "end": v(-9.46, 6.3) * mm});
            skArc(sketch, "E2053", {"start": v(-38.87, 15.61) * mm, "mid": v(-39.25, 15.07) * mm, "end": v(-39.6, 14.5) * mm});
            skLineSegment(sketch, "E2054", {"start": v(-28.93, 20) * mm, "end": v(-28.93, 20.22) * mm});
            skLineSegment(sketch, "E2055", {"start": v(-37.5, -1.75) * mm, "end": v(-37.7, -1.86) * mm});
            skLineSegment(sketch, "E2056", {"start": v(-37.7, -1.86) * mm, "end": v(-37.83, -1.94) * mm});
            skLineSegment(sketch, "E2057", {"start": v(-37.83, -1.94) * mm, "end": v(-37.97, -2.06) * mm});
            skLineSegment(sketch, "E2058", {"start": v(-19.64, -9.65) * mm, "end": v(-19.63, -9.86) * mm});
            skLineSegment(sketch, "E2059", {"start": v(-9.09, 6.36) * mm, "end": v(-8.91, 6.41) * mm});
            skLineSegment(sketch, "E2060", {"start": v(-37.97, -2.06) * mm, "end": v(-38.12, -2.2) * mm});
            skLineSegment(sketch, "E2061", {"start": v(-19.63, -9.86) * mm, "end": v(-19.63, -10.08) * mm});
            skLineSegment(sketch, "E2062", {"start": v(-8.91, 6.41) * mm, "end": v(-8.72, 6.48) * mm});
            skLineSegment(sketch, "E2063", {"start": v(-38.12, -2.2) * mm, "end": v(-38.29, -2.36) * mm});
            skLineSegment(sketch, "E2064", {"start": v(-19.63, -10.08) * mm, "end": v(-19.64, -10.33) * mm});
            skLineSegment(sketch, "E2065", {"start": v(-8.72, 6.48) * mm, "end": v(-8.5, 6.57) * mm});
            skLineSegment(sketch, "E2066", {"start": v(-38.29, -2.36) * mm, "end": v(-38.45, -2.54) * mm});
            skLineSegment(sketch, "E2067", {"start": v(-19.64, -10.33) * mm, "end": v(-19.67, -10.6) * mm});
            skLineSegment(sketch, "E2068", {"start": v(-8.5, 6.57) * mm, "end": v(-8.28, 6.67) * mm});
            skLineSegment(sketch, "E2069", {"start": v(-38.45, -2.54) * mm, "end": v(-38.62, -2.74) * mm});
            skLineSegment(sketch, "E2070", {"start": v(-19.67, -10.6) * mm, "end": v(-19.83, -11.48) * mm});
            skLineSegment(sketch, "E2071", {"start": v(-8.28, 6.67) * mm, "end": v(-8.05, 6.8) * mm});
            skLineSegment(sketch, "E2072", {"start": v(-38.62, -2.74) * mm, "end": v(-39.13, -3.48) * mm});
            skLineSegment(sketch, "E2073", {"start": v(-39.13, -3.48) * mm, "end": v(-39.6, -4.37) * mm});
            skArc(sketch, "E2074", {"start": v(-39.6, -4.37) * mm, "mid": v(-39.25, -4.93) * mm, "end": v(-38.87, -5.48) * mm});
            skLineSegment(sketch, "E2075", {"start": v(-35.2, -4.17) * mm, "end": v(-35.64, -4.54) * mm});
            skArc(sketch, "E2076", {"start": v(-17.74, -7.64) * mm, "mid": v(-18.2, -7.24) * mm, "end": v(-18.8, -7.27) * mm});
            skLineSegment(sketch, "E2077", {"start": v(-10.67, 9.42) * mm, "end": v(-10.12, 9.6) * mm});
            skLineSegment(sketch, "E2078", {"start": v(-35.64, -4.54) * mm, "end": v(-35.82, -4.68) * mm});
            skLineSegment(sketch, "E2079", {"start": v(-17.74, -7.64) * mm, "end": v(-17.47, -8.15) * mm});
            skLineSegment(sketch, "E2080", {"start": v(-10.12, 9.6) * mm, "end": v(-9.9, 9.66) * mm});
            skLineSegment(sketch, "E2081", {"start": v(-14.68, -6.29) * mm, "end": v(-14.53, -6.46) * mm});
            skLineSegment(sketch, "E2082", {"start": v(-11.58, 11.61) * mm, "end": v(-11.06, 11.88) * mm});
            skLineSegment(sketch, "E2083", {"start": v(-15.05, -5.84) * mm, "end": v(-14.68, -6.29) * mm});
            skArc(sketch, "E2084", {"start": v(-11.58, 11.61) * mm, "mid": v(-11.97, 11.16) * mm, "end": v(-11.95, 10.56) * mm});
            skArc(sketch, "E2085", {"start": v(-34.08, -4.23) * mm, "mid": v(-33.83, -4.48) * mm, "end": v(-33.58, -4.73) * mm});
            skArc(sketch, "E2086", {"start": v(-14.84, -10.26) * mm, "mid": v(-14.28, -9.9) * mm, "end": v(-13.74, -9.52) * mm});
            skArc(sketch, "E2087", {"start": v(-11.68, 9.9) * mm, "mid": v(-11.81, 10.23) * mm, "end": v(-11.95, 10.56) * mm});
            skArc(sketch, "E2088", {"start": v(-34.08, -4.23) * mm, "mid": v(-34.62, -3.97) * mm, "end": v(-35.2, -4.17) * mm});
            skLineSegment(sketch, "E2089", {"start": v(-15.73, -9.78) * mm, "end": v(-14.84, -10.26) * mm});
            skArc(sketch, "E2090", {"start": v(-11.68, 9.9) * mm, "mid": v(-11.27, 9.46) * mm, "end": v(-10.67, 9.42) * mm});
            skLineSegment(sketch, "E2091", {"start": v(-37.87, -5.38) * mm, "end": v(-38.87, -5.48) * mm});
            skLineSegment(sketch, "E2092", {"start": v(-16.47, -9.27) * mm, "end": v(-15.73, -9.78) * mm});
            skLineSegment(sketch, "E2093", {"start": v(-7.73, 9.52) * mm, "end": v(-6.77, 9.23) * mm});
            skLineSegment(sketch, "E2094", {"start": v(-36.98, -5.19) * mm, "end": v(-37.87, -5.38) * mm});
            skLineSegment(sketch, "E2095", {"start": v(-16.67, -9.1) * mm, "end": v(-16.47, -9.27) * mm});
            skLineSegment(sketch, "E2096", {"start": v(-8.62, 9.68) * mm, "end": v(-7.73, 9.52) * mm});
            skLineSegment(sketch, "E2097", {"start": v(-36.73, -5.11) * mm, "end": v(-36.98, -5.19) * mm});
            skLineSegment(sketch, "E2098", {"start": v(-16.86, -8.94) * mm, "end": v(-16.67, -9.1) * mm});
            skLineSegment(sketch, "E2099", {"start": v(-8.88, 9.7) * mm, "end": v(-8.62, 9.68) * mm});
            skLineSegment(sketch, "E2100", {"start": v(-36.5, -5.03) * mm, "end": v(-36.73, -5.11) * mm});
            skLineSegment(sketch, "E2101", {"start": v(-17.02, -8.77) * mm, "end": v(-16.86, -8.94) * mm});
            skLineSegment(sketch, "E2102", {"start": v(-9.13, 9.72) * mm, "end": v(-8.88, 9.7) * mm});
            skLineSegment(sketch, "E2103", {"start": v(-36.3, -4.94) * mm, "end": v(-36.5, -5.03) * mm});
            skLineSegment(sketch, "E2104", {"start": v(-17.16, -8.62) * mm, "end": v(-17.02, -8.77) * mm});
            skLineSegment(sketch, "E2105", {"start": v(-9.36, 9.72) * mm, "end": v(-9.13, 9.72) * mm});
            skLineSegment(sketch, "E2106", {"start": v(-36.1, -4.85) * mm, "end": v(-36.3, -4.94) * mm});
            skLineSegment(sketch, "E2107", {"start": v(-17.28, -8.48) * mm, "end": v(-17.16, -8.62) * mm});
            skLineSegment(sketch, "E2108", {"start": v(-9.57, 9.7) * mm, "end": v(-9.36, 9.72) * mm});
            skLineSegment(sketch, "E2109", {"start": v(-35.94, -4.76) * mm, "end": v(-36.1, -4.85) * mm});
            skLineSegment(sketch, "E2110", {"start": v(-17.36, -8.35) * mm, "end": v(-17.28, -8.48) * mm});
            skLineSegment(sketch, "E2111", {"start": v(-9.75, 9.69) * mm, "end": v(-9.57, 9.7) * mm});
            skLineSegment(sketch, "E2112", {"start": v(-35.82, -4.68) * mm, "end": v(-35.94, -4.76) * mm});
            skLineSegment(sketch, "E2113", {"start": v(-17.47, -8.15) * mm, "end": v(-17.36, -8.35) * mm});
            skLineSegment(sketch, "E2114", {"start": v(-9.9, 9.66) * mm, "end": v(-9.75, 9.69) * mm});
            skArc(sketch, "E2115", {"start": v(-33.58, 14.86) * mm, "mid": v(-33.32, 15.4) * mm, "end": v(-33.52, 15.98) * mm});
            skLineSegment(sketch, "E2116", {"start": v(-25.58, 20.26) * mm, "end": v(-25.63, 20.44) * mm});
            skLineSegment(sketch, "E2117", {"start": v(-38.45, 0.54) * mm, "end": v(-38.67, 0.47) * mm});
            skLineSegment(sketch, "E2118", {"start": v(-23.1, -9.18) * mm, "end": v(-23.05, -9.76) * mm});
            skLineSegment(sketch, "E2119", {"start": v(-9.46, 3.83) * mm, "end": v(-9.23, 3.8) * mm});
            skLineSegment(sketch, "E2120", {"start": v(-34.73, 18.65) * mm, "end": v(-34.83, 19.65) * mm});
            skLineSegment(sketch, "E2121", {"start": v(-25.54, 20.12) * mm, "end": v(-25.58, 20.26) * mm});
            skLineSegment(sketch, "E2122", {"start": v(-37.9, 0.71) * mm, "end": v(-38.45, 0.54) * mm});
            skArc(sketch, "E2123", {"start": v(-23.1, -9.18) * mm, "mid": v(-23.36, -8.64) * mm, "end": v(-23.93, -8.43) * mm});
            skLineSegment(sketch, "E2124", {"start": v(-10.04, 3.88) * mm, "end": v(-9.46, 3.83) * mm});
            skLineSegment(sketch, "E2125", {"start": v(-34.54, 17.77) * mm, "end": v(-34.73, 18.65) * mm});
            skLineSegment(sketch, "E2126", {"start": v(-25.52, 19.89) * mm, "end": v(-25.54, 20.12) * mm});
            skArc(sketch, "E2127", {"start": v(-42.05, 2.21) * mm, "mid": v(-41.94, 1.56) * mm, "end": v(-41.8, 0.9) * mm});
            skArc(sketch, "E2128", {"start": v(-24.64, -8.43) * mm, "mid": v(-24.28, -8.43) * mm, "end": v(-23.93, -8.43) * mm});
            skArc(sketch, "E2129", {"start": v(-6.77, 0.9) * mm, "mid": v(-6.63, 1.56) * mm, "end": v(-6.51, 2.21) * mm});
            skLineSegment(sketch, "E2130", {"start": v(-34.46, 17.52) * mm, "end": v(-34.54, 17.77) * mm});
            skLineSegment(sketch, "E2131", {"start": v(-25.47, 19.31) * mm, "end": v(-25.52, 19.89) * mm});
            skLineSegment(sketch, "E2132", {"start": v(-41.28, 2.85) * mm, "end": v(-42.05, 2.21) * mm});
            skArc(sketch, "E2133", {"start": v(-24.64, -8.43) * mm, "mid": v(-25.2, -8.64) * mm, "end": v(-25.47, -9.18) * mm});
            skLineSegment(sketch, "E2134", {"start": v(-7.73, 0.61) * mm, "end": v(-6.77, 0.9) * mm});
            skLineSegment(sketch, "E2135", {"start": v(-34.38, 17.29) * mm, "end": v(-34.46, 17.52) * mm});
            skArc(sketch, "E2136", {"start": v(-25.47, 19.31) * mm, "mid": v(-25.2, 18.77) * mm, "end": v(-24.64, 18.56) * mm});
            skLineSegment(sketch, "E2137", {"start": v(-26.5, -11.93) * mm, "end": v(-27.14, -12.7) * mm});
            skLineSegment(sketch, "E2138", {"start": v(-8.62, 0.45) * mm, "end": v(-7.73, 0.61) * mm});
            skLineSegment(sketch, "E2139", {"start": v(-34.3, 17.07) * mm, "end": v(-34.38, 17.29) * mm});
            skArc(sketch, "E2140", {"start": v(-23.93, 18.56) * mm, "mid": v(-24.28, 18.57) * mm, "end": v(-24.64, 18.56) * mm});
            skLineSegment(sketch, "E2141", {"start": v(-26.01, -11.17) * mm, "end": v(-26.5, -11.93) * mm});
            skLineSegment(sketch, "E2142", {"start": v(-8.88, 0.43) * mm, "end": v(-8.62, 0.45) * mm});
            skLineSegment(sketch, "E2143", {"start": v(-34.2, 16.88) * mm, "end": v(-34.3, 17.07) * mm});
            skArc(sketch, "E2144", {"start": v(-23.93, 18.56) * mm, "mid": v(-23.36, 18.77) * mm, "end": v(-23.1, 19.31) * mm});
            skLineSegment(sketch, "E2145", {"start": v(-25.89, -10.93) * mm, "end": v(-26.01, -11.17) * mm});
            skLineSegment(sketch, "E2146", {"start": v(-9.13, 0.42) * mm, "end": v(-8.88, 0.43) * mm});
            skLineSegment(sketch, "E2147", {"start": v(-34.11, 16.72) * mm, "end": v(-34.2, 16.88) * mm});
            skLineSegment(sketch, "E2148", {"start": v(-22.07, 22.06) * mm, "end": v(-21.43, 22.84) * mm});
            skLineSegment(sketch, "E2149", {"start": v(-25.78, -10.71) * mm, "end": v(-25.89, -10.93) * mm});
            skLineSegment(sketch, "E2150", {"start": v(-9.36, 0.42) * mm, "end": v(-9.13, 0.42) * mm});
            skLineSegment(sketch, "E2151", {"start": v(-34.03, 16.6) * mm, "end": v(-34.11, 16.72) * mm});
            skLineSegment(sketch, "E2152", {"start": v(-22.55, 21.3) * mm, "end": v(-22.07, 22.06) * mm});
            skLineSegment(sketch, "E2153", {"start": v(-25.7, -10.5) * mm, "end": v(-25.78, -10.71) * mm});
            skLineSegment(sketch, "E2154", {"start": v(-9.57, 0.43) * mm, "end": v(-9.36, 0.42) * mm});
            skLineSegment(sketch, "E2155", {"start": v(-33.9, 16.42) * mm, "end": v(-34.03, 16.6) * mm});
            skLineSegment(sketch, "E2156", {"start": v(-22.68, 21.07) * mm, "end": v(-22.55, 21.3) * mm});
            skLineSegment(sketch, "E2157", {"start": v(-25.63, -10.3) * mm, "end": v(-25.7, -10.5) * mm});
            skLineSegment(sketch, "E2158", {"start": v(-9.75, 0.45) * mm, "end": v(-9.57, 0.43) * mm});
            skLineSegment(sketch, "E2159", {"start": v(-33.52, 15.98) * mm, "end": v(-33.9, 16.42) * mm});
            skLineSegment(sketch, "E2160", {"start": v(-22.78, 20.85) * mm, "end": v(-22.68, 21.07) * mm});
            skLineSegment(sketch, "E2161", {"start": v(-25.58, -10.13) * mm, "end": v(-25.63, -10.3) * mm});
            skLineSegment(sketch, "E2162", {"start": v(-9.9, 0.47) * mm, "end": v(-9.75, 0.45) * mm});
            skArc(sketch, "E2163", {"start": v(-33.72, 20.4) * mm, "mid": v(-34.28, 20.03) * mm, "end": v(-34.83, 19.65) * mm});
            skLineSegment(sketch, "E2164", {"start": v(-22.87, 20.63) * mm, "end": v(-22.78, 20.85) * mm});
            skLineSegment(sketch, "E2165", {"start": v(-25.54, -9.98) * mm, "end": v(-25.58, -10.13) * mm});
            skLineSegment(sketch, "E2166", {"start": v(-10.12, 0.54) * mm, "end": v(-9.9, 0.47) * mm});
            skLineSegment(sketch, "E2167", {"start": v(-32.83, 19.92) * mm, "end": v(-33.72, 20.4) * mm});
            skLineSegment(sketch, "E2168", {"start": v(-22.94, 20.44) * mm, "end": v(-22.87, 20.63) * mm});
            skLineSegment(sketch, "E2169", {"start": v(-25.52, -9.76) * mm, "end": v(-25.54, -9.98) * mm});
            skLineSegment(sketch, "E2170", {"start": v(-10.67, 0.71) * mm, "end": v(-10.12, 0.54) * mm});
            skLineSegment(sketch, "E2171", {"start": v(-32.1, 19.4) * mm, "end": v(-32.83, 19.92) * mm});
            skLineSegment(sketch, "E2172", {"start": v(-23, 20.26) * mm, "end": v(-22.94, 20.44) * mm});
            skLineSegment(sketch, "E2173", {"start": v(-25.47, -9.18) * mm, "end": v(-25.52, -9.76) * mm});
            skArc(sketch, "E2174", {"start": v(-10.67, 0.71) * mm, "mid": v(-11.27, 0.67) * mm, "end": v(-11.68, 0.23) * mm});
            skLineSegment(sketch, "E2175", {"start": v(-31.9, 19.24) * mm, "end": v(-32.1, 19.4) * mm});
            skLineSegment(sketch, "E2176", {"start": v(-23.02, 20.12) * mm, "end": v(-23, 20.26) * mm});
            skArc(sketch, "E2177", {"start": v(-28.44, -12.45) * mm, "mid": v(-27.8, -12.59) * mm, "end": v(-27.14, -12.7) * mm});
            skArc(sketch, "E2178", {"start": v(-11.95, -0.42) * mm, "mid": v(-11.81, -0.1) * mm, "end": v(-11.68, 0.23) * mm});
            skLineSegment(sketch, "E2179", {"start": v(-31.7, 19.07) * mm, "end": v(-31.9, 19.24) * mm});
            skLineSegment(sketch, "E2180", {"start": v(-23.05, 19.89) * mm, "end": v(-23.02, 20.12) * mm});
            skLineSegment(sketch, "E2181", {"start": v(-28.74, -11.48) * mm, "end": v(-28.44, -12.45) * mm});
            skArc(sketch, "E2182", {"start": v(-11.95, -0.42) * mm, "mid": v(-11.97, -1.03) * mm, "end": v(-11.58, -1.48) * mm});
            skLineSegment(sketch, "E2183", {"start": v(-31.55, 18.9) * mm, "end": v(-31.7, 19.07) * mm});
            skLineSegment(sketch, "E2184", {"start": v(-23.1, 19.31) * mm, "end": v(-23.05, 19.89) * mm});
            skLineSegment(sketch, "E2185", {"start": v(-28.9, -10.6) * mm, "end": v(-28.74, -11.48) * mm});
            skLineSegment(sketch, "E2186", {"start": v(-9.43, -3.48) * mm, "end": v(-8.96, -4.37) * mm});
            skLineSegment(sketch, "E2187", {"start": v(-31.4, 18.75) * mm, "end": v(-31.55, 18.9) * mm});
            skArc(sketch, "E2188", {"start": v(-20.12, 22.58) * mm, "mid": v(-20.77, 22.72) * mm, "end": v(-21.43, 22.84) * mm});
            skLineSegment(sketch, "E2189", {"start": v(-28.92, -10.33) * mm, "end": v(-28.9, -10.6) * mm});
            skLineSegment(sketch, "E2190", {"start": v(-9.95, -2.74) * mm, "end": v(-9.43, -3.48) * mm});
            skLineSegment(sketch, "E2191", {"start": v(-31.3, 18.6) * mm, "end": v(-31.4, 18.75) * mm});
            skLineSegment(sketch, "E2192", {"start": v(-19.83, 21.62) * mm, "end": v(-20.12, 22.58) * mm});
            skLineSegment(sketch, "E2193", {"start": v(-28.93, -10.08) * mm, "end": v(-28.92, -10.33) * mm});
            skLineSegment(sketch, "E2194", {"start": v(-10.11, -2.54) * mm, "end": v(-9.95, -2.74) * mm});
            skLineSegment(sketch, "E2195", {"start": v(-31.2, 18.49) * mm, "end": v(-31.3, 18.6) * mm});
            skLineSegment(sketch, "E2196", {"start": v(-19.67, 20.73) * mm, "end": v(-19.83, 21.62) * mm});
            skLineSegment(sketch, "E2197", {"start": v(-28.93, -9.86) * mm, "end": v(-28.93, -10.08) * mm});
            skLineSegment(sketch, "E2198", {"start": v(-10.28, -2.36) * mm, "end": v(-10.11, -2.54) * mm});
            skLineSegment(sketch, "E2199", {"start": v(-31.1, 18.29) * mm, "end": v(-31.2, 18.49) * mm});
            skLineSegment(sketch, "E2200", {"start": v(-19.64, 20.47) * mm, "end": v(-19.67, 20.73) * mm});
            skLineSegment(sketch, "E2201", {"start": v(-28.92, -9.65) * mm, "end": v(-28.93, -9.86) * mm});
            skLineSegment(sketch, "E2202", {"start": v(-10.44, -2.2) * mm, "end": v(-10.28, -2.36) * mm});
            skLineSegment(sketch, "E2203", {"start": v(-30.83, 17.77) * mm, "end": v(-31.1, 18.29) * mm});
            skLineSegment(sketch, "E2204", {"start": v(-19.63, 20.22) * mm, "end": v(-19.64, 20.47) * mm});
            skLineSegment(sketch, "E2205", {"start": v(-28.9, -9.46) * mm, "end": v(-28.92, -9.65) * mm});
            skLineSegment(sketch, "E2206", {"start": v(-10.6, -2.06) * mm, "end": v(-10.44, -2.2) * mm});
            skArc(sketch, "E2207", {"start": v(-30.83, 17.77) * mm, "mid": v(-30.38, 17.38) * mm, "end": v(-29.77, 17.4) * mm});
            skLineSegment(sketch, "E2208", {"start": v(-19.63, 20) * mm, "end": v(-19.63, 20.22) * mm});
            skLineSegment(sketch, "E2209", {"start": v(-28.88, -9.32) * mm, "end": v(-28.9, -9.46) * mm});
            skLineSegment(sketch, "E2210", {"start": v(-10.74, -1.94) * mm, "end": v(-10.6, -2.06) * mm});
            skArc(sketch, "E2211", {"start": v(-29.12, 17.67) * mm, "mid": v(-29.45, 17.54) * mm, "end": v(-29.77, 17.4) * mm});
            skLineSegment(sketch, "E2212", {"start": v(-19.64, 19.78) * mm, "end": v(-19.63, 20) * mm});
            skLineSegment(sketch, "E2213", {"start": v(-28.81, -9.1) * mm, "end": v(-28.88, -9.32) * mm});
            skLineSegment(sketch, "E2214", {"start": v(-10.86, -1.86) * mm, "end": v(-10.74, -1.94) * mm});
            skArc(sketch, "E2215", {"start": v(-29.12, 17.67) * mm, "mid": v(-28.68, 18.08) * mm, "end": v(-28.64, 18.68) * mm});
            skLineSegment(sketch, "E2216", {"start": v(-19.66, 19.6) * mm, "end": v(-19.64, 19.78) * mm});
            skLineSegment(sketch, "E2217", {"start": v(-28.64, -8.55) * mm, "end": v(-28.81, -9.1) * mm});
            skLineSegment(sketch, "E2218", {"start": v(-11.06, -1.75) * mm, "end": v(-10.86, -1.86) * mm});
            skLineSegment(sketch, "E2219", {"start": v(-28.74, 21.62) * mm, "end": v(-28.44, 22.58) * mm});
            skLineSegment(sketch, "E2220", {"start": v(-19.69, 19.45) * mm, "end": v(-19.66, 19.6) * mm});
            skLineSegment(sketch, "E2221", {"start": v(-40.52, 3.34) * mm, "end": v(-41.28, 2.85) * mm});
            skArc(sketch, "E2222", {"start": v(-28.64, -8.55) * mm, "mid": v(-28.68, -7.94) * mm, "end": v(-29.12, -7.54) * mm});
            skLineSegment(sketch, "E2223", {"start": v(-11.58, -1.48) * mm, "end": v(-11.06, -1.75) * mm});
            skLineSegment(sketch, "E2224", {"start": v(-40.28, 3.46) * mm, "end": v(-40.52, 3.34) * mm});
            skArc(sketch, "E2225", {"start": v(-29.77, -7.27) * mm, "mid": v(-29.45, -7.4) * mm, "end": v(-29.12, -7.54) * mm});
            skArc(sketch, "E2226", {"start": v(-9.7, -5.48) * mm, "mid": v(-9.32, -4.93) * mm, "end": v(-8.96, -4.37) * mm});
            skLineSegment(sketch, "E2227", {"start": v(-40.06, 3.57) * mm, "end": v(-40.28, 3.46) * mm});
            skArc(sketch, "E2228", {"start": v(-29.77, -7.27) * mm, "mid": v(-30.38, -7.24) * mm, "end": v(-30.83, -7.64) * mm});
            skLineSegment(sketch, "E2229", {"start": v(-10.7, -5.38) * mm, "end": v(-9.7, -5.48) * mm});
            skLineSegment(sketch, "E2230", {"start": v(-39.85, 3.65) * mm, "end": v(-40.06, 3.57) * mm});
            skLineSegment(sketch, "E2231", {"start": v(-32.83, -9.78) * mm, "end": v(-33.72, -10.26) * mm});
            skLineSegment(sketch, "E2232", {"start": v(-11.58, -5.19) * mm, "end": v(-10.7, -5.38) * mm});
            skLineSegment(sketch, "E2233", {"start": v(-39.68, 9.7) * mm, "end": v(-39.94, 9.68) * mm});
            skLineSegment(sketch, "E2234", {"start": v(-39.65, 3.72) * mm, "end": v(-39.85, 3.65) * mm});
            skLineSegment(sketch, "E2235", {"start": v(-32.1, -9.27) * mm, "end": v(-32.83, -9.78) * mm});
            skLineSegment(sketch, "E2236", {"start": v(-11.83, -5.11) * mm, "end": v(-11.58, -5.19) * mm});
            skLineSegment(sketch, "E2237", {"start": v(-39.44, 9.72) * mm, "end": v(-39.68, 9.7) * mm});
            skLineSegment(sketch, "E2238", {"start": v(-39.48, 3.78) * mm, "end": v(-39.65, 3.72) * mm});
            skLineSegment(sketch, "E2239", {"start": v(-31.9, -9.1) * mm, "end": v(-32.1, -9.27) * mm});
            skLineSegment(sketch, "E2240", {"start": v(-12.06, -5.03) * mm, "end": v(-11.83, -5.11) * mm});
            skLineSegment(sketch, "E2241", {"start": v(-39.2, 9.72) * mm, "end": v(-39.44, 9.72) * mm});
            skLineSegment(sketch, "E2242", {"start": v(-39.33, 3.8) * mm, "end": v(-39.48, 3.78) * mm});
            skLineSegment(sketch, "E2243", {"start": v(-31.7, -8.94) * mm, "end": v(-31.9, -9.1) * mm});
            skLineSegment(sketch, "E2244", {"start": v(-12.28, -4.94) * mm, "end": v(-12.06, -5.03) * mm});
            skLineSegment(sketch, "E2245", {"start": v(-39, 9.7) * mm, "end": v(-39.2, 9.72) * mm});
            skLineSegment(sketch, "E2246", {"start": v(-39.1, 3.83) * mm, "end": v(-39.33, 3.8) * mm});
            skLineSegment(sketch, "E2247", {"start": v(-31.55, -8.77) * mm, "end": v(-31.7, -8.94) * mm});
            skLineSegment(sketch, "E2248", {"start": v(-12.47, -4.85) * mm, "end": v(-12.28, -4.94) * mm});
            skLineSegment(sketch, "E2249", {"start": v(-38.81, 9.69) * mm, "end": v(-39, 9.7) * mm});
            skLineSegment(sketch, "E2250", {"start": v(-38.53, 3.88) * mm, "end": v(-39.1, 3.83) * mm});
            skLineSegment(sketch, "E2251", {"start": v(-31.4, -8.62) * mm, "end": v(-31.55, -8.77) * mm});
            skLineSegment(sketch, "E2252", {"start": v(-12.63, -4.76) * mm, "end": v(-12.47, -4.85) * mm});
            skLineSegment(sketch, "E2253", {"start": v(-38.67, 9.66) * mm, "end": v(-38.81, 9.69) * mm});
            skArc(sketch, "E2254", {"start": v(-38.53, 3.88) * mm, "mid": v(-37.99, 4.15) * mm, "end": v(-37.78, 4.71) * mm});
            skLineSegment(sketch, "E2255", {"start": v(-31.3, -8.48) * mm, "end": v(-31.4, -8.62) * mm});
            skLineSegment(sketch, "E2256", {"start": v(-12.75, -4.68) * mm, "end": v(-12.63, -4.76) * mm});
            skLineSegment(sketch, "E2257", {"start": v(-38.45, 9.6) * mm, "end": v(-38.67, 9.66) * mm});
            skArc(sketch, "E2258", {"start": v(-37.78, 5.42) * mm, "mid": v(-37.78, 5.07) * mm, "end": v(-37.78, 4.71) * mm});
            skLineSegment(sketch, "E2259", {"start": v(-31.2, -8.35) * mm, "end": v(-31.3, -8.48) * mm});
            skLineSegment(sketch, "E2260", {"start": v(-12.93, -4.54) * mm, "end": v(-12.75, -4.68) * mm});
            skLineSegment(sketch, "E2261", {"start": v(-37.9, 9.42) * mm, "end": v(-38.45, 9.6) * mm});
            skArc(sketch, "E2262", {"start": v(-37.78, 5.42) * mm, "mid": v(-37.99, 5.99) * mm, "end": v(-38.53, 6.25) * mm});
            skLineSegment(sketch, "E2263", {"start": v(-31.1, -8.15) * mm, "end": v(-31.2, -8.35) * mm});
            skLineSegment(sketch, "E2264", {"start": v(-13.37, -4.17) * mm, "end": v(-12.93, -4.54) * mm});
            skArc(sketch, "E2265", {"start": v(-37.9, 9.42) * mm, "mid": v(-37.3, 9.46) * mm, "end": v(-36.89, 9.9) * mm});
            skLineSegment(sketch, "E2266", {"start": v(-41.28, 7.28) * mm, "end": v(-42.05, 7.92) * mm});
            skArc(sketch, "E2267", {"start": v(-13.37, -4.17) * mm, "mid": v(-13.94, -3.97) * mm, "end": v(-14.5, -4.23) * mm});
            skArc(sketch, "E2268", {"start": v(-36.62, 10.56) * mm, "mid": v(-36.76, 10.23) * mm, "end": v(-36.89, 9.9) * mm});
            skLineSegment(sketch, "E2269", {"start": v(-40.52, 6.8) * mm, "end": v(-41.28, 7.28) * mm});
            skArc(sketch, "E2270", {"start": v(-34.83, -9.52) * mm, "mid": v(-34.28, -9.9) * mm, "end": v(-33.72, -10.26) * mm});
            skArc(sketch, "E2271", {"start": v(-36.62, 10.56) * mm, "mid": v(-36.6, 11.16) * mm, "end": v(-36.99, 11.61) * mm});
            skLineSegment(sketch, "E2272", {"start": v(-40.28, 6.67) * mm, "end": v(-40.52, 6.8) * mm});
            skLineSegment(sketch, "E2273", {"start": v(-34.73, -8.52) * mm, "end": v(-34.83, -9.52) * mm});
            skLineSegment(sketch, "E2274", {"start": v(-39.13, 13.62) * mm, "end": v(-39.6, 14.5) * mm});
            skLineSegment(sketch, "E2275", {"start": v(-40.06, 6.57) * mm, "end": v(-40.28, 6.67) * mm});
            skLineSegment(sketch, "E2276", {"start": v(-34.54, -7.63) * mm, "end": v(-34.73, -8.52) * mm});
            skLineSegment(sketch, "E2277", {"start": v(-38.62, 12.88) * mm, "end": v(-39.13, 13.62) * mm});
            skLineSegment(sketch, "E2278", {"start": v(-39.85, 6.48) * mm, "end": v(-40.06, 6.57) * mm});
            skArc(sketch, "E2279", {"start": v(-6.51, 7.92) * mm, "mid": v(-6.63, 8.58) * mm, "end": v(-6.77, 9.23) * mm});
            skArc(sketch, "E2280", {"start": v(-19.44, -7.54) * mm, "mid": v(-19.12, -7.4) * mm, "end": v(-18.8, -7.27) * mm});
            skLineSegment(sketch, "E2281", {"start": v(-34.46, -7.38) * mm, "end": v(-34.54, -7.63) * mm});
            skLineSegment(sketch, "E2282", {"start": v(-38.45, 12.68) * mm, "end": v(-38.62, 12.88) * mm});
            skLineSegment(sketch, "E2283", {"start": v(-39.65, 6.41) * mm, "end": v(-39.85, 6.48) * mm});
            skLineSegment(sketch, "E2284", {"start": v(-7.29, 7.28) * mm, "end": v(-6.51, 7.92) * mm});
            skArc(sketch, "E2285", {"start": v(-19.44, -7.54) * mm, "mid": v(-19.89, -7.94) * mm, "end": v(-19.93, -8.55) * mm});
            skLineSegment(sketch, "E2286", {"start": v(-34.38, -7.15) * mm, "end": v(-34.46, -7.38) * mm});
            skLineSegment(sketch, "E2287", {"start": v(-38.29, 12.5) * mm, "end": v(-38.45, 12.68) * mm});
            skLineSegment(sketch, "E2288", {"start": v(-39.48, 6.36) * mm, "end": v(-39.65, 6.41) * mm});
            skLineSegment(sketch, "E2289", {"start": v(-8.05, 6.8) * mm, "end": v(-7.29, 7.28) * mm});
            skLineSegment(sketch, "E2290", {"start": v(-19.83, -11.48) * mm, "end": v(-20.12, -12.45) * mm});
            skLineSegment(sketch, "E2291", {"start": v(-34.3, -6.94) * mm, "end": v(-34.38, -7.15) * mm});
            skLineSegment(sketch, "E2292", {"start": v(-38.12, 12.33) * mm, "end": v(-38.29, 12.5) * mm});
            skLineSegment(sketch, "E2293", {"start": v(-39.33, 6.33) * mm, "end": v(-39.48, 6.36) * mm});
            skLineSegment(sketch, "E2294", {"start": v(-34.2, -6.75) * mm, "end": v(-34.3, -6.94) * mm});
            skLineSegment(sketch, "E2295", {"start": v(-37.97, 12.2) * mm, "end": v(-38.12, 12.33) * mm});
            skLineSegment(sketch, "E2296", {"start": v(-39.1, 6.3) * mm, "end": v(-39.33, 6.33) * mm});
            skLineSegment(sketch, "E2297", {"start": v(-34.11, -6.59) * mm, "end": v(-34.2, -6.75) * mm});
            skLineSegment(sketch, "E2298", {"start": v(-37.83, 12.08) * mm, "end": v(-37.97, 12.2) * mm});
            skLineSegment(sketch, "E2299", {"start": v(-38.53, 6.25) * mm, "end": v(-39.1, 6.3) * mm});
            skLineSegment(sketch, "E2300", {"start": v(-34.03, -6.46) * mm, "end": v(-34.11, -6.59) * mm});
            skLineSegment(sketch, "E2301", {"start": v(-37.7, 12) * mm, "end": v(-37.83, 12.08) * mm});
            skArc(sketch, "E2302", {"start": v(-41.8, 9.23) * mm, "mid": v(-41.94, 8.58) * mm, "end": v(-42.05, 7.92) * mm});
            skLineSegment(sketch, "E2303", {"start": v(-33.9, -6.29) * mm, "end": v(-34.03, -6.46) * mm});
            skLineSegment(sketch, "E2304", {"start": v(-37.5, 11.88) * mm, "end": v(-37.7, 12) * mm});
            skLineSegment(sketch, "E2305", {"start": v(-40.83, 9.52) * mm, "end": v(-41.8, 9.23) * mm});
            skLineSegment(sketch, "E2306", {"start": v(-33.52, -5.84) * mm, "end": v(-33.9, -6.29) * mm});
            skLineSegment(sketch, "E2307", {"start": v(-36.99, 11.61) * mm, "end": v(-37.5, 11.88) * mm});
            skLineSegment(sketch, "E2308", {"start": v(-39.94, 9.68) * mm, "end": v(-40.83, 9.52) * mm});
            skArc(sketch, "E2309", {"start": v(-33.52, -5.84) * mm, "mid": v(-33.32, -5.27) * mm, "end": v(-33.58, -4.73) * mm});
            skLineSegment(sketch, "E2310", {"start": v(-28.9, 20.73) * mm, "end": v(-28.74, 21.62) * mm});
            skLineSegment(sketch, "E2311", {"start": v(-19.75, 19.23) * mm, "end": v(-19.69, 19.45) * mm});
            skLineSegment(sketch, "E2312", {"start": v(-28.92, 20.47) * mm, "end": v(-28.9, 20.73) * mm});
            skLineSegment(sketch, "E2313", {"start": v(-19.93, 18.68) * mm, "end": v(-19.75, 19.23) * mm});
            skLineSegment(sketch, "E2314", {"start": v(-28.93, 20.22) * mm, "end": v(-28.92, 20.47) * mm});
            skArc(sketch, "E2315", {"start": v(-19.93, 18.68) * mm, "mid": v(-19.89, 18.08) * mm, "end": v(-19.44, 17.67) * mm});
            skLineSegment(sketch, "E2316", {"start": v(-14.53, -6.46) * mm, "end": v(-14.45, -6.59) * mm});
            skLineSegment(sketch, "E2317", {"start": v(-11.06, 11.88) * mm, "end": v(-10.86, 12) * mm});
            skLineSegment(sketch, "E2318", {"start": v(-14.45, -6.59) * mm, "end": v(-14.37, -6.75) * mm});
            skLineSegment(sketch, "E2319", {"start": v(-10.86, 12) * mm, "end": v(-10.74, 12.08) * mm});
            skLineSegment(sketch, "E2320", {"start": v(-14.37, -6.75) * mm, "end": v(-14.28, -6.94) * mm});
            skLineSegment(sketch, "E2321", {"start": v(-10.74, 12.08) * mm, "end": v(-10.6, 12.2) * mm});
            skLineSegment(sketch, "E2322", {"start": v(-14.28, -6.94) * mm, "end": v(-14.19, -7.15) * mm});
            skLineSegment(sketch, "E2323", {"start": v(-10.6, 12.2) * mm, "end": v(-10.44, 12.33) * mm});
            skLineSegment(sketch, "E2324", {"start": v(-14.19, -7.15) * mm, "end": v(-14.1, -7.38) * mm});
            skLineSegment(sketch, "E2325", {"start": v(-10.44, 12.33) * mm, "end": v(-10.28, 12.5) * mm});
            skLineSegment(sketch, "E2326", {"start": v(-14.1, -7.38) * mm, "end": v(-14.03, -7.63) * mm});
            skLineSegment(sketch, "E2327", {"start": v(-10.28, 12.5) * mm, "end": v(-10.11, 12.68) * mm});
            skLineSegment(sketch, "E2328", {"start": v(-14.03, -7.63) * mm, "end": v(-13.83, -8.52) * mm});
            skLineSegment(sketch, "E2329", {"start": v(-10.11, 12.68) * mm, "end": v(-9.95, 12.88) * mm});
            skLineSegment(sketch, "E2330", {"start": v(-13.83, -8.52) * mm, "end": v(-13.74, -9.52) * mm});
            skLineSegment(sketch, "E2331", {"start": v(-9.95, 12.88) * mm, "end": v(-9.43, 13.62) * mm});
            skArc(sketch, "E2332", {"start": v(-15, -4.73) * mm, "mid": v(-15.24, -5.27) * mm, "end": v(-15.05, -5.84) * mm});
            skLineSegment(sketch, "E2333", {"start": v(-9.43, 13.62) * mm, "end": v(-8.96, 14.5) * mm});
            skArc(sketch, "E2334", {"start": v(-15, -4.73) * mm, "mid": v(-14.74, -4.48) * mm, "end": v(-14.5, -4.23) * mm});
            skArc(sketch, "E2335", {"start": v(-8.96, 14.5) * mm, "mid": v(-9.32, 15.07) * mm, "end": v(-9.7, 15.61) * mm});
            skLineSegment(sketch, "E2336", {"start": v(-13.37, 14.3) * mm, "end": v(-12.93, 14.67) * mm});
            skLineSegment(sketch, "E2337", {"start": v(-12.93, 14.67) * mm, "end": v(-12.75, 14.82) * mm});
            skLineSegment(sketch, "E2338", {"start": v(-12.75, 14.82) * mm, "end": v(-12.63, 14.9) * mm});
            skLineSegment(sketch, "E2339", {"start": v(-12.63, 14.9) * mm, "end": v(-12.47, 14.98) * mm});
            skLineSegment(sketch, "E2340", {"start": v(-12.47, 14.98) * mm, "end": v(-12.28, 15.07) * mm});
            skLineSegment(sketch, "E2341", {"start": v(-12.28, 15.07) * mm, "end": v(-12.06, 15.16) * mm});
            skLineSegment(sketch, "E2342", {"start": v(-12.06, 15.16) * mm, "end": v(-11.83, 15.25) * mm});
            skLineSegment(sketch, "E2343", {"start": v(-11.83, 15.25) * mm, "end": v(-11.58, 15.32) * mm});
            skLineSegment(sketch, "E2344", {"start": v(-11.58, 15.32) * mm, "end": v(-10.7, 15.52) * mm});
            skLineSegment(sketch, "E2345", {"start": v(-10.7, 15.52) * mm, "end": v(-9.7, 15.61) * mm});
            skArc(sketch, "E2346", {"start": v(-14.5, 14.36) * mm, "mid": v(-13.94, 14.1) * mm, "end": v(-13.37, 14.3) * mm});
            skArc(sketch, "E2347", {"start": v(-14.5, 14.36) * mm, "mid": v(-14.74, 14.61) * mm, "end": v(-15, 14.86) * mm});
            skArc(sketch, "E2348", {"start": v(-15.05, 15.98) * mm, "mid": v(-15.24, 15.4) * mm, "end": v(-15, 14.86) * mm});
            skLineSegment(sketch, "E2349", {"start": v(-15.05, 15.98) * mm, "end": v(-14.68, 16.42) * mm});
            skLineSegment(sketch, "E2350", {"start": v(-14.68, 16.42) * mm, "end": v(-14.53, 16.6) * mm});
            skLineSegment(sketch, "E2351", {"start": v(-14.53, 16.6) * mm, "end": v(-14.45, 16.72) * mm});
            skLineSegment(sketch, "E2352", {"start": v(-14.45, 16.72) * mm, "end": v(-14.37, 16.88) * mm});
            skLineSegment(sketch, "E2353", {"start": v(-14.37, 16.88) * mm, "end": v(-14.28, 17.07) * mm});
            skLineSegment(sketch, "E2354", {"start": v(-14.28, 17.07) * mm, "end": v(-14.19, 17.29) * mm});
            skLineSegment(sketch, "E2355", {"start": v(-14.19, 17.29) * mm, "end": v(-14.1, 17.52) * mm});
            skLineSegment(sketch, "E2356", {"start": v(-14.1, 17.52) * mm, "end": v(-14.03, 17.77) * mm});
            skLineSegment(sketch, "E2357", {"start": v(-14.03, 17.77) * mm, "end": v(-13.83, 18.65) * mm});
            skLineSegment(sketch, "E2358", {"start": v(-13.83, 18.65) * mm, "end": v(-13.74, 19.65) * mm});
            skArc(sketch, "E2359", {"start": v(-13.74, 19.65) * mm, "mid": v(-14.28, 20.03) * mm, "end": v(-14.84, 20.4) * mm});
            skLineSegment(sketch, "E2360", {"start": v(-17.74, 17.77) * mm, "end": v(-17.47, 18.29) * mm});
            skLineSegment(sketch, "E2361", {"start": v(-17.47, 18.29) * mm, "end": v(-17.36, 18.49) * mm});
            skLineSegment(sketch, "E2362", {"start": v(-17.36, 18.49) * mm, "end": v(-17.28, 18.6) * mm});
            skLineSegment(sketch, "E2363", {"start": v(-17.28, 18.6) * mm, "end": v(-17.16, 18.75) * mm});
            skLineSegment(sketch, "E2364", {"start": v(-17.16, 18.75) * mm, "end": v(-17.02, 18.9) * mm});
            skLineSegment(sketch, "E2365", {"start": v(-17.02, 18.9) * mm, "end": v(-16.86, 19.07) * mm});
            skLineSegment(sketch, "E2366", {"start": v(-16.86, 19.07) * mm, "end": v(-16.67, 19.24) * mm});
            skLineSegment(sketch, "E2367", {"start": v(-16.67, 19.24) * mm, "end": v(-16.47, 19.4) * mm});
            skLineSegment(sketch, "E2368", {"start": v(-16.47, 19.4) * mm, "end": v(-15.73, 19.92) * mm});
            skLineSegment(sketch, "E2369", {"start": v(-15.73, 19.92) * mm, "end": v(-14.84, 20.4) * mm});
            skArc(sketch, "E2370", {"start": v(-18.8, 17.4) * mm, "mid": v(-18.2, 17.38) * mm, "end": v(-17.74, 17.77) * mm});
            skArc(sketch, "E2371", {"start": v(-18.8, 17.4) * mm, "mid": v(-19.12, 17.54) * mm, "end": v(-19.44, 17.67) * mm});
            skCircle(sketch, "E2372", {"center": v(-24.28, 5.07) * mm, "radius": 3.1 * mm});
            skLineSegment(sketch, "E2373", {"start": v(-19.69, -9.32) * mm, "end": v(-19.66, -9.46) * mm});
            skLineSegment(sketch, "E2374", {"start": v(-9.46, 6.3) * mm, "end": v(-9.23, 6.33) * mm});
            skLineSegment(sketch, "E2375", {"start": v(-19.66, -9.46) * mm, "end": v(-19.64, -9.65) * mm});
            skLineSegment(sketch, "E2376", {"start": v(-9.23, 6.33) * mm, "end": v(-9.09, 6.36) * mm});
            skLineSegment(sketch, "E2377", {"start": v(-30.83, -7.64) * mm, "end": v(-31.1, -8.15) * mm});
            skPoint(sketch, "E2378.visualSharp", {"position": v(59.96, -60.62) * mm});
            skArc(sketch, "E2378.filletArc", {"start": v(59.96, -63.62) * mm, "mid": v(59.08, -61.5) * mm, "end": v(56.96, -60.62) * mm});
            skPoint(sketch, "E2379.visualSharp", {"position": v(59.96, -72.62) * mm});
            skArc(sketch, "E2379.filletArc", {"start": v(56.96, -72.62) * mm, "mid": v(59.08, -71.74) * mm, "end": v(59.96, -69.62) * mm});
            skPoint(sketch, "E2380.visualSharp", {"position": v(59.22, -88.93) * mm});
            skArc(sketch, "E2380.filletArc", {"start": v(59.22, -91.93) * mm, "mid": v(58.34, -89.8) * mm, "end": v(56.22, -88.93) * mm});
            skPoint(sketch, "E2381.visualSharp", {"position": v(59.22, -100.93) * mm});
            skArc(sketch, "E2381.filletArc", {"start": v(56.22, -100.93) * mm, "mid": v(58.34, -100.05) * mm, "end": v(59.22, -97.93) * mm});
            skSolve(sketch);
        }
        {
            var Q0;
            Q0 = qSketchRegion(id + "F0", true);
            extrude(context, id + "F1", {"entities" : qUnion([Q0]), "depth" : 5 * mm, "offsetDistance" : 25 * mm});
        }
    });
